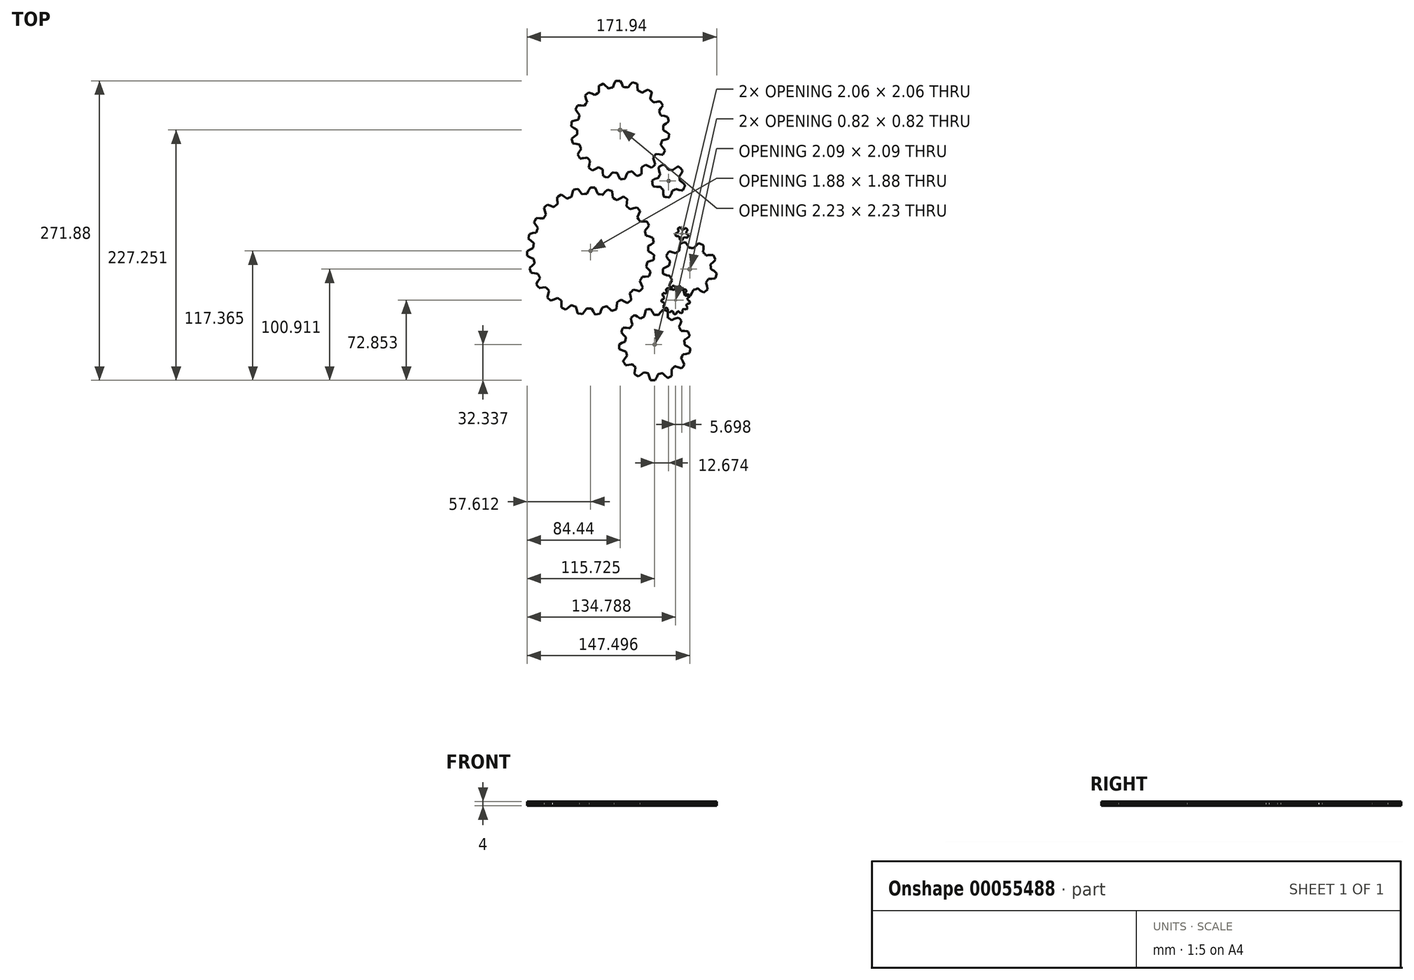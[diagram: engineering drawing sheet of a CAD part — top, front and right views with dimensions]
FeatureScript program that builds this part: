
annotation { "Feature Type Name" : "Feature", "Feature Type Description" : "" }
export const myFeature = defineFeature(function(context is Context, id is Id, definition is map)
    precondition{}
    {
        {
            var Q0;
            Q0=qCreatedBy(makeId("Top.planeOp"),FACE);
            var sketch = newSketch(context, id + "F0", { "sketchPlane" : qUnion([Q0])});
            skLineSegment(sketch, "E0", {"start": v(23.91, -18.64) * mm, "end": v(23.86, -16.49) * mm});
            skLineSegment(sketch, "E1", {"start": v(23.86, -16.49) * mm, "end": v(23.77, -15) * mm});
            skLineSegment(sketch, "E2", {"start": v(23.77, -15) * mm, "end": v(23.72, -14.33) * mm});
            skLineSegment(sketch, "E3", {"start": v(23.72, -14.33) * mm, "end": v(24.54, -13.82) * mm});
            skLineSegment(sketch, "E4", {"start": v(24.54, -13.82) * mm, "end": v(26.32, -12.65) * mm});
            skLineSegment(sketch, "E5", {"start": v(26.32, -12.65) * mm, "end": v(28.84, -10.83) * mm});
            skLineSegment(sketch, "E6", {"start": v(28.84, -10.83) * mm, "end": v(28.51, -8.7) * mm});
            skLineSegment(sketch, "E7", {"start": v(28.51, -8.7) * mm, "end": v(28.25, -7.25) * mm});
            skLineSegment(sketch, "E8", {"start": v(28.25, -7.25) * mm, "end": v(28.15, -6.77) * mm});
            skLineSegment(sketch, "E9", {"start": v(28.15, -6.77) * mm, "end": v(28.11, -6.6) * mm});
            skLineSegment(sketch, "E10", {"start": v(28.11, -6.6) * mm, "end": v(25.07, -5.56) * mm});
            skLineSegment(sketch, "E11", {"start": v(25.07, -5.56) * mm, "end": v(22.97, -4.95) * mm});
            skLineSegment(sketch, "E12", {"start": v(22.97, -4.95) * mm, "end": v(22.02, -4.7) * mm});
            skLineSegment(sketch, "E13", {"start": v(22.02, -4.7) * mm, "end": v(21.8, -3.9) * mm});
            skLineSegment(sketch, "E14", {"start": v(21.8, -3.9) * mm, "end": v(21.36, -2.5) * mm});
            skLineSegment(sketch, "E15", {"start": v(21.36, -2.5) * mm, "end": v(20.88, -1.09) * mm});
            skLineSegment(sketch, "E16", {"start": v(20.88, -1.09) * mm, "end": v(20.65, -0.46) * mm});
            skLineSegment(sketch, "E17", {"start": v(20.65, -0.46) * mm, "end": v(22.68, 1.86) * mm});
            skLineSegment(sketch, "E18", {"start": v(22.68, 1.86) * mm, "end": v(24.04, 3.53) * mm});
            skLineSegment(sketch, "E19", {"start": v(24.04, 3.53) * mm, "end": v(24.62, 4.3) * mm});
            skLineSegment(sketch, "E20", {"start": v(24.62, 4.3) * mm, "end": v(23.74, 6.27) * mm});
            skLineSegment(sketch, "E21", {"start": v(23.74, 6.27) * mm, "end": v(22.76, 8.18) * mm});
            skLineSegment(sketch, "E22", {"start": v(22.76, 8.18) * mm, "end": v(21.77, 8.26) * mm});
            skLineSegment(sketch, "E23", {"start": v(21.77, 8.26) * mm, "end": v(19.56, 8.35) * mm});
            skLineSegment(sketch, "E24", {"start": v(19.56, 8.35) * mm, "end": v(16.4, 8.36) * mm});
            skLineSegment(sketch, "E25", {"start": v(16.4, 8.36) * mm, "end": v(16.32, 8.48) * mm});
            skLineSegment(sketch, "E26", {"start": v(16.32, 8.48) * mm, "end": v(15.16, 10.3) * mm});
            skLineSegment(sketch, "E27", {"start": v(15.16, 10.3) * mm, "end": v(13.92, 12.06) * mm});
            skLineSegment(sketch, "E28", {"start": v(13.92, 12.06) * mm, "end": v(15.25, 14.85) * mm});
            skLineSegment(sketch, "E29", {"start": v(15.25, 14.85) * mm, "end": v(16.46, 17.73) * mm});
            skLineSegment(sketch, "E30", {"start": v(16.46, 17.73) * mm, "end": v(16.35, 17.87) * mm});
            skLineSegment(sketch, "E31", {"start": v(16.35, 17.87) * mm, "end": v(16.04, 18.25) * mm});
            skLineSegment(sketch, "E32", {"start": v(16.04, 18.25) * mm, "end": v(14.09, 20.47) * mm});
            skLineSegment(sketch, "E33", {"start": v(14.09, 20.47) * mm, "end": v(13.63, 20.95) * mm});
            skLineSegment(sketch, "E34", {"start": v(13.63, 20.95) * mm, "end": v(10.5, 20.26) * mm});
            skLineSegment(sketch, "E35", {"start": v(10.5, 20.26) * mm, "end": v(7.44, 19.4) * mm});
            skLineSegment(sketch, "E36", {"start": v(7.44, 19.4) * mm, "end": v(6.84, 19.97) * mm});
            skLineSegment(sketch, "E37", {"start": v(6.84, 19.97) * mm, "end": v(4.6, 21.9) * mm});
            skLineSegment(sketch, "E38", {"start": v(4.6, 21.9) * mm, "end": v(4.06, 22.31) * mm});
            skLineSegment(sketch, "E39", {"start": v(4.06, 22.31) * mm, "end": v(4.6, 25.37) * mm});
            skLineSegment(sketch, "E40", {"start": v(4.6, 25.37) * mm, "end": v(4.99, 28.45) * mm});
            skLineSegment(sketch, "E41", {"start": v(4.99, 28.45) * mm, "end": v(3.88, 29.23) * mm});
            skLineSegment(sketch, "E42", {"start": v(3.88, 29.23) * mm, "end": v(1.97, 30.46) * mm});
            skLineSegment(sketch, "E43", {"start": v(1.97, 30.46) * mm, "end": v(1.4, 30.8) * mm});
            skLineSegment(sketch, "E44", {"start": v(1.4, 30.8) * mm, "end": v(-1.44, 29.29) * mm});
            skLineSegment(sketch, "E45", {"start": v(-1.44, 29.29) * mm, "end": v(-3.31, 28.18) * mm});
            skLineSegment(sketch, "E46", {"start": v(-3.31, 28.18) * mm, "end": v(-4.15, 27.65) * mm});
            skLineSegment(sketch, "E47", {"start": v(-4.15, 27.65) * mm, "end": v(-4.88, 28.02) * mm});
            skLineSegment(sketch, "E48", {"start": v(-4.88, 28.02) * mm, "end": v(-6.21, 28.67) * mm});
            skLineSegment(sketch, "E49", {"start": v(-6.21, 28.67) * mm, "end": v(-8, 29.48) * mm});
            skLineSegment(sketch, "E50", {"start": v(-8, 29.48) * mm, "end": v(-8.18, 29.55) * mm});
            skLineSegment(sketch, "E51", {"start": v(-8.18, 29.55) * mm, "end": v(-8.5, 32.6) * mm});
            skLineSegment(sketch, "E52", {"start": v(-8.5, 32.6) * mm, "end": v(-8.78, 34.74) * mm});
            skLineSegment(sketch, "E53", {"start": v(-8.78, 34.74) * mm, "end": v(-8.95, 35.7) * mm});
            skLineSegment(sketch, "E54", {"start": v(-8.95, 35.7) * mm, "end": v(-10.98, 36.39) * mm});
            skLineSegment(sketch, "E55", {"start": v(-10.98, 36.39) * mm, "end": v(-13.05, 36.98) * mm});
            skLineSegment(sketch, "E56", {"start": v(-13.05, 36.98) * mm, "end": v(-15.36, 34.76) * mm});
            skLineSegment(sketch, "E57", {"start": v(-15.36, 34.76) * mm, "end": v(-17.53, 32.45) * mm});
            skLineSegment(sketch, "E58", {"start": v(-17.53, 32.45) * mm, "end": v(-17.67, 32.48) * mm});
            skLineSegment(sketch, "E59", {"start": v(-17.67, 32.48) * mm, "end": v(-17.85, 32.52) * mm});
            skLineSegment(sketch, "E60", {"start": v(-17.85, 32.52) * mm, "end": v(-19.79, 32.87) * mm});
            skLineSegment(sketch, "E61", {"start": v(-19.79, 32.87) * mm, "end": v(-21.26, 33.08) * mm});
            skLineSegment(sketch, "E62", {"start": v(-21.26, 33.08) * mm, "end": v(-21.92, 33.17) * mm});
            skLineSegment(sketch, "E63", {"start": v(-21.92, 33.17) * mm, "end": v(-22.26, 34.07) * mm});
            skLineSegment(sketch, "E64", {"start": v(-22.26, 34.07) * mm, "end": v(-23.05, 36.05) * mm});
            skLineSegment(sketch, "E65", {"start": v(-23.05, 36.05) * mm, "end": v(-24.33, 38.89) * mm});
            skLineSegment(sketch, "E66", {"start": v(-24.33, 38.89) * mm, "end": v(-26.47, 39) * mm});
            skLineSegment(sketch, "E67", {"start": v(-26.47, 39) * mm, "end": v(-27.95, 39.03) * mm});
            skLineSegment(sketch, "E68", {"start": v(-27.95, 39.03) * mm, "end": v(-28.62, 39.03) * mm});
            skLineSegment(sketch, "E69", {"start": v(-28.62, 39.03) * mm, "end": v(-30.25, 36.25) * mm});
            skLineSegment(sketch, "E70", {"start": v(-30.25, 36.25) * mm, "end": v(-31.72, 33.44) * mm});
            skLineSegment(sketch, "E71", {"start": v(-31.72, 33.44) * mm, "end": v(-34, 33.25) * mm});
            skLineSegment(sketch, "E72", {"start": v(-34, 33.25) * mm, "end": v(-36.15, 32.98) * mm});
            skLineSegment(sketch, "E73", {"start": v(-36.15, 32.98) * mm, "end": v(-36.71, 33.75) * mm});
            skLineSegment(sketch, "E74", {"start": v(-36.71, 33.75) * mm, "end": v(-38, 35.43) * mm});
            skLineSegment(sketch, "E75", {"start": v(-38, 35.43) * mm, "end": v(-39.36, 37.1) * mm});
            skLineSegment(sketch, "E76", {"start": v(-39.36, 37.1) * mm, "end": v(-40, 37.85) * mm});
            skLineSegment(sketch, "E77", {"start": v(-40, 37.85) * mm, "end": v(-42.1, 37.36) * mm});
            skLineSegment(sketch, "E78", {"start": v(-42.1, 37.36) * mm, "end": v(-43.52, 36.99) * mm});
            skLineSegment(sketch, "E79", {"start": v(-43.52, 36.99) * mm, "end": v(-44.17, 36.8) * mm});
            skLineSegment(sketch, "E80", {"start": v(-44.17, 36.8) * mm, "end": v(-44.44, 35.84) * mm});
            skLineSegment(sketch, "E81", {"start": v(-44.44, 35.84) * mm, "end": v(-45, 33.71) * mm});
            skLineSegment(sketch, "E82", {"start": v(-45, 33.71) * mm, "end": v(-45.64, 30.6) * mm});
            skLineSegment(sketch, "E83", {"start": v(-45.64, 30.6) * mm, "end": v(-45.96, 30.5) * mm});
            skLineSegment(sketch, "E84", {"start": v(-45.96, 30.5) * mm, "end": v(-46.42, 30.33) * mm});
            skLineSegment(sketch, "E85", {"start": v(-46.42, 30.33) * mm, "end": v(-48.53, 29.5) * mm});
            skLineSegment(sketch, "E86", {"start": v(-48.53, 29.5) * mm, "end": v(-49.78, 28.94) * mm});
            skLineSegment(sketch, "E87", {"start": v(-49.78, 28.94) * mm, "end": v(-50.53, 29.54) * mm});
            skLineSegment(sketch, "E88", {"start": v(-50.53, 29.54) * mm, "end": v(-52.24, 30.82) * mm});
            skLineSegment(sketch, "E89", {"start": v(-52.24, 30.82) * mm, "end": v(-54.8, 32.58) * mm});
            skLineSegment(sketch, "E90", {"start": v(-54.8, 32.58) * mm, "end": v(-55.4, 32.27) * mm});
            skLineSegment(sketch, "E91", {"start": v(-55.4, 32.27) * mm, "end": v(-57.97, 30.82) * mm});
            skLineSegment(sketch, "E92", {"start": v(-57.97, 30.82) * mm, "end": v(-58.39, 30.57) * mm});
            skLineSegment(sketch, "E93", {"start": v(-58.39, 30.57) * mm, "end": v(-58.54, 30.47) * mm});
            skLineSegment(sketch, "E94", {"start": v(-58.54, 30.47) * mm, "end": v(-58.5, 27.25) * mm});
            skLineSegment(sketch, "E95", {"start": v(-58.5, 27.25) * mm, "end": v(-58.44, 26.1) * mm});
            skLineSegment(sketch, "E96", {"start": v(-58.44, 26.1) * mm, "end": v(-58.28, 24.09) * mm});
            skLineSegment(sketch, "E97", {"start": v(-58.28, 24.09) * mm, "end": v(-59.5, 23.21) * mm});
            skLineSegment(sketch, "E98", {"start": v(-59.5, 23.21) * mm, "end": v(-61.3, 21.8) * mm});
            skLineSegment(sketch, "E99", {"start": v(-61.3, 21.8) * mm, "end": v(-61.67, 21.5) * mm});
            skLineSegment(sketch, "E100", {"start": v(-61.67, 21.5) * mm, "end": v(-61.81, 21.38) * mm});
            skLineSegment(sketch, "E101", {"start": v(-61.81, 21.38) * mm, "end": v(-64.68, 22.51) * mm});
            skLineSegment(sketch, "E102", {"start": v(-64.68, 22.51) * mm, "end": v(-67.63, 23.52) * mm});
            skLineSegment(sketch, "E103", {"start": v(-67.63, 23.52) * mm, "end": v(-69.18, 22.04) * mm});
            skLineSegment(sketch, "E104", {"start": v(-69.18, 22.04) * mm, "end": v(-70.66, 20.48) * mm});
            skLineSegment(sketch, "E105", {"start": v(-70.66, 20.48) * mm, "end": v(-70.4, 19.52) * mm});
            skLineSegment(sketch, "E106", {"start": v(-70.4, 19.52) * mm, "end": v(-69.75, 17.4) * mm});
            skLineSegment(sketch, "E107", {"start": v(-69.75, 17.4) * mm, "end": v(-69.05, 15.34) * mm});
            skLineSegment(sketch, "E108", {"start": v(-69.05, 15.34) * mm, "end": v(-68.7, 14.42) * mm});
            skLineSegment(sketch, "E109", {"start": v(-68.7, 14.42) * mm, "end": v(-70.13, 12.6) * mm});
            skLineSegment(sketch, "E110", {"start": v(-70.13, 12.6) * mm, "end": v(-71.38, 10.85) * mm});
            skLineSegment(sketch, "E111", {"start": v(-71.38, 10.85) * mm, "end": v(-72.34, 10.97) * mm});
            skLineSegment(sketch, "E112", {"start": v(-72.34, 10.97) * mm, "end": v(-74.44, 11.17) * mm});
            skLineSegment(sketch, "E113", {"start": v(-74.44, 11.17) * mm, "end": v(-77.57, 11.36) * mm});
            skLineSegment(sketch, "E114", {"start": v(-77.57, 11.36) * mm, "end": v(-77.66, 11.2) * mm});
            skLineSegment(sketch, "E115", {"start": v(-77.66, 11.2) * mm, "end": v(-79.03, 8.81) * mm});
            skLineSegment(sketch, "E116", {"start": v(-79.03, 8.81) * mm, "end": v(-79.65, 7.6) * mm});
            skLineSegment(sketch, "E117", {"start": v(-79.65, 7.6) * mm, "end": v(-79.13, 6.74) * mm});
            skLineSegment(sketch, "E118", {"start": v(-79.13, 6.74) * mm, "end": v(-77.96, 4.89) * mm});
            skLineSegment(sketch, "E119", {"start": v(-77.96, 4.89) * mm, "end": v(-76.13, 2.29) * mm});
            skLineSegment(sketch, "E120", {"start": v(-76.13, 2.29) * mm, "end": v(-76.46, 1.54) * mm});
            skLineSegment(sketch, "E121", {"start": v(-76.46, 1.54) * mm, "end": v(-77, 0.16) * mm});
            skLineSegment(sketch, "E122", {"start": v(-77, 0.16) * mm, "end": v(-77.52, -1.23) * mm});
            skLineSegment(sketch, "E123", {"start": v(-77.52, -1.23) * mm, "end": v(-77.74, -1.86) * mm});
            skLineSegment(sketch, "E124", {"start": v(-77.74, -1.86) * mm, "end": v(-80.8, -2.38) * mm});
            skLineSegment(sketch, "E125", {"start": v(-80.8, -2.38) * mm, "end": v(-83.83, -3.05) * mm});
            skLineSegment(sketch, "E126", {"start": v(-83.83, -3.05) * mm, "end": v(-84, -3.7) * mm});
            skLineSegment(sketch, "E127", {"start": v(-84, -3.7) * mm, "end": v(-84.37, -5.13) * mm});
            skLineSegment(sketch, "E128", {"start": v(-84.37, -5.13) * mm, "end": v(-84.8, -7.04) * mm});
            skLineSegment(sketch, "E129", {"start": v(-84.8, -7.04) * mm, "end": v(-84.84, -7.23) * mm});
            skLineSegment(sketch, "E130", {"start": v(-84.84, -7.23) * mm, "end": v(-82.45, -9.38) * mm});
            skLineSegment(sketch, "E131", {"start": v(-82.45, -9.38) * mm, "end": v(-80, -11.39) * mm});
            skLineSegment(sketch, "E132", {"start": v(-80, -11.39) * mm, "end": v(-80.27, -13.67) * mm});
            skLineSegment(sketch, "E133", {"start": v(-80.27, -13.67) * mm, "end": v(-80.43, -15.82) * mm});
            skLineSegment(sketch, "E134", {"start": v(-80.43, -15.82) * mm, "end": v(-81.3, -16.22) * mm});
            skLineSegment(sketch, "E135", {"start": v(-81.3, -16.22) * mm, "end": v(-83.2, -17.14) * mm});
            skLineSegment(sketch, "E136", {"start": v(-83.2, -17.14) * mm, "end": v(-85.97, -18.61) * mm});
            skLineSegment(sketch, "E137", {"start": v(-85.97, -18.61) * mm, "end": v(-85.9, -21.54) * mm});
            skLineSegment(sketch, "E138", {"start": v(-85.9, -21.54) * mm, "end": v(-85.8, -22.9) * mm});
            skLineSegment(sketch, "E139", {"start": v(-85.8, -22.9) * mm, "end": v(-82.95, -24.34) * mm});
            skLineSegment(sketch, "E140", {"start": v(-82.95, -24.34) * mm, "end": v(-80.03, -25.61) * mm});
            skLineSegment(sketch, "E141", {"start": v(-80.03, -25.61) * mm, "end": v(-79.93, -26.42) * mm});
            skLineSegment(sketch, "E142", {"start": v(-79.93, -26.42) * mm, "end": v(-79.4, -29.34) * mm});
            skLineSegment(sketch, "E143", {"start": v(-79.4, -29.34) * mm, "end": v(-79.25, -30) * mm});
            skLineSegment(sketch, "E144", {"start": v(-79.25, -30) * mm, "end": v(-81.6, -32.02) * mm});
            skLineSegment(sketch, "E145", {"start": v(-81.6, -32.02) * mm, "end": v(-83.15, -33.49) * mm});
            skLineSegment(sketch, "E146", {"start": v(-83.15, -33.49) * mm, "end": v(-83.84, -34.17) * mm});
            skLineSegment(sketch, "E147", {"start": v(-83.84, -34.17) * mm, "end": v(-83.23, -36.23) * mm});
            skLineSegment(sketch, "E148", {"start": v(-83.23, -36.23) * mm, "end": v(-82.55, -38.27) * mm});
            skLineSegment(sketch, "E149", {"start": v(-82.55, -38.27) * mm, "end": v(-81.56, -38.47) * mm});
            skLineSegment(sketch, "E150", {"start": v(-81.56, -38.47) * mm, "end": v(-79.38, -38.87) * mm});
            skLineSegment(sketch, "E151", {"start": v(-79.38, -38.87) * mm, "end": v(-77.23, -39.2) * mm});
            skLineSegment(sketch, "E152", {"start": v(-77.23, -39.2) * mm, "end": v(-76.25, -39.31) * mm});
            skLineSegment(sketch, "E153", {"start": v(-76.25, -39.31) * mm, "end": v(-75.3, -41.4) * mm});
            skLineSegment(sketch, "E154", {"start": v(-75.3, -41.4) * mm, "end": v(-74.31, -43.32) * mm});
            skLineSegment(sketch, "E155", {"start": v(-74.31, -43.32) * mm, "end": v(-74.85, -44.12) * mm});
            skLineSegment(sketch, "E156", {"start": v(-74.85, -44.12) * mm, "end": v(-76, -45.9) * mm});
            skLineSegment(sketch, "E157", {"start": v(-76, -45.9) * mm, "end": v(-77.6, -48.59) * mm});
            skLineSegment(sketch, "E158", {"start": v(-77.6, -48.59) * mm, "end": v(-76.44, -50.4) * mm});
            skLineSegment(sketch, "E159", {"start": v(-76.44, -50.4) * mm, "end": v(-75.61, -51.62) * mm});
            skLineSegment(sketch, "E160", {"start": v(-75.61, -51.62) * mm, "end": v(-75.22, -52.16) * mm});
            skLineSegment(sketch, "E161", {"start": v(-75.22, -52.16) * mm, "end": v(-74.22, -52.1) * mm});
            skLineSegment(sketch, "E162", {"start": v(-74.22, -52.1) * mm, "end": v(-72.03, -51.9) * mm});
            skLineSegment(sketch, "E163", {"start": v(-72.03, -51.9) * mm, "end": v(-68.88, -51.47) * mm});
            skLineSegment(sketch, "E164", {"start": v(-68.88, -51.47) * mm, "end": v(-68.8, -51.59) * mm});
            skLineSegment(sketch, "E165", {"start": v(-68.8, -51.59) * mm, "end": v(-68.37, -52.1) * mm});
            skLineSegment(sketch, "E166", {"start": v(-68.37, -52.1) * mm, "end": v(-66.87, -53.82) * mm});
            skLineSegment(sketch, "E167", {"start": v(-66.87, -53.82) * mm, "end": v(-65.93, -54.81) * mm});
            skLineSegment(sketch, "E168", {"start": v(-65.93, -54.81) * mm, "end": v(-66.24, -55.72) * mm});
            skLineSegment(sketch, "E169", {"start": v(-66.24, -55.72) * mm, "end": v(-66.88, -57.76) * mm});
            skLineSegment(sketch, "E170", {"start": v(-66.88, -57.76) * mm, "end": v(-67.68, -60.76) * mm});
            skLineSegment(sketch, "E171", {"start": v(-67.68, -60.76) * mm, "end": v(-67.2, -61.23) * mm});
            skLineSegment(sketch, "E172", {"start": v(-67.2, -61.23) * mm, "end": v(-64.97, -63.17) * mm});
            skLineSegment(sketch, "E173", {"start": v(-64.97, -63.17) * mm, "end": v(-64.44, -63.58) * mm});
            skLineSegment(sketch, "E174", {"start": v(-64.44, -63.58) * mm, "end": v(-61.43, -62.47) * mm});
            skLineSegment(sketch, "E175", {"start": v(-61.43, -62.47) * mm, "end": v(-59.41, -61.62) * mm});
            skLineSegment(sketch, "E176", {"start": v(-59.41, -61.62) * mm, "end": v(-58.51, -61.2) * mm});
            skLineSegment(sketch, "E177", {"start": v(-58.51, -61.2) * mm, "end": v(-57.85, -61.68) * mm});
            skLineSegment(sketch, "E178", {"start": v(-57.85, -61.68) * mm, "end": v(-55.36, -63.3) * mm});
            skLineSegment(sketch, "E179", {"start": v(-55.36, -63.3) * mm, "end": v(-54.78, -63.63) * mm});
            skLineSegment(sketch, "E180", {"start": v(-54.78, -63.63) * mm, "end": v(-54.9, -66.72) * mm});
            skLineSegment(sketch, "E181", {"start": v(-54.9, -66.72) * mm, "end": v(-54.89, -68.86) * mm});
            skLineSegment(sketch, "E182", {"start": v(-54.89, -68.86) * mm, "end": v(-54.86, -69.84) * mm});
            skLineSegment(sketch, "E183", {"start": v(-54.86, -69.84) * mm, "end": v(-52.94, -70.8) * mm});
            skLineSegment(sketch, "E184", {"start": v(-52.94, -70.8) * mm, "end": v(-50.98, -71.68) * mm});
            skLineSegment(sketch, "E185", {"start": v(-50.98, -71.68) * mm, "end": v(-50.16, -71.1) * mm});
            skLineSegment(sketch, "E186", {"start": v(-50.16, -71.1) * mm, "end": v(-48.38, -69.78) * mm});
            skLineSegment(sketch, "E187", {"start": v(-48.38, -69.78) * mm, "end": v(-46.68, -68.44) * mm});
            skLineSegment(sketch, "E188", {"start": v(-46.68, -68.44) * mm, "end": v(-45.92, -67.8) * mm});
            skLineSegment(sketch, "E189", {"start": v(-45.92, -67.8) * mm, "end": v(-43.74, -68.53) * mm});
            skLineSegment(sketch, "E190", {"start": v(-43.74, -68.53) * mm, "end": v(-41.67, -69.12) * mm});
            skLineSegment(sketch, "E191", {"start": v(-41.67, -69.12) * mm, "end": v(-41.46, -70.06) * mm});
            skLineSegment(sketch, "E192", {"start": v(-41.46, -70.06) * mm, "end": v(-40.94, -72.11) * mm});
            skLineSegment(sketch, "E193", {"start": v(-40.94, -72.11) * mm, "end": v(-40.06, -75.12) * mm});
            skLineSegment(sketch, "E194", {"start": v(-40.06, -75.12) * mm, "end": v(-39.88, -75.16) * mm});
            skLineSegment(sketch, "E195", {"start": v(-39.88, -75.16) * mm, "end": v(-37.17, -75.64) * mm});
            skLineSegment(sketch, "E196", {"start": v(-37.17, -75.64) * mm, "end": v(-35.83, -75.82) * mm});
            skLineSegment(sketch, "E197", {"start": v(-35.83, -75.82) * mm, "end": v(-33.84, -73.31) * mm});
            skLineSegment(sketch, "E198", {"start": v(-33.84, -73.31) * mm, "end": v(-32, -70.7) * mm});
            skLineSegment(sketch, "E199", {"start": v(-32, -70.7) * mm, "end": v(-31.19, -70.77) * mm});
            skLineSegment(sketch, "E200", {"start": v(-31.19, -70.77) * mm, "end": v(-28.22, -70.85) * mm});
            skLineSegment(sketch, "E201", {"start": v(-28.22, -70.85) * mm, "end": v(-27.55, -70.83) * mm});
            skLineSegment(sketch, "E202", {"start": v(-27.55, -70.83) * mm, "end": v(-26.04, -73.53) * mm});
            skLineSegment(sketch, "E203", {"start": v(-26.04, -73.53) * mm, "end": v(-24.93, -75.36) * mm});
            skLineSegment(sketch, "E204", {"start": v(-24.93, -75.36) * mm, "end": v(-24.4, -76.18) * mm});
            skLineSegment(sketch, "E205", {"start": v(-24.4, -76.18) * mm, "end": v(-22.26, -76) * mm});
            skLineSegment(sketch, "E206", {"start": v(-22.26, -76) * mm, "end": v(-20.13, -75.74) * mm});
            skLineSegment(sketch, "E207", {"start": v(-20.13, -75.74) * mm, "end": v(-19.72, -74.82) * mm});
            skLineSegment(sketch, "E208", {"start": v(-19.72, -74.82) * mm, "end": v(-18.88, -72.77) * mm});
            skLineSegment(sketch, "E209", {"start": v(-18.88, -72.77) * mm, "end": v(-17.81, -69.8) * mm});
            skLineSegment(sketch, "E210", {"start": v(-17.81, -69.8) * mm, "end": v(-15.57, -69.29) * mm});
            skLineSegment(sketch, "E211", {"start": v(-15.57, -69.29) * mm, "end": v(-13.5, -68.71) * mm});
            skLineSegment(sketch, "E212", {"start": v(-13.5, -68.71) * mm, "end": v(-12.82, -69.41) * mm});
            skLineSegment(sketch, "E213", {"start": v(-12.82, -69.41) * mm, "end": v(-11.32, -70.9) * mm});
            skLineSegment(sketch, "E214", {"start": v(-11.32, -70.9) * mm, "end": v(-9.01, -73) * mm});
            skLineSegment(sketch, "E215", {"start": v(-9.01, -73) * mm, "end": v(-8.38, -72.79) * mm});
            skLineSegment(sketch, "E216", {"start": v(-8.38, -72.79) * mm, "end": v(-5.63, -71.7) * mm});
            skLineSegment(sketch, "E217", {"start": v(-5.63, -71.7) * mm, "end": v(-5.02, -71.42) * mm});
            skLineSegment(sketch, "E218", {"start": v(-5.02, -71.42) * mm, "end": v(-4.63, -68.24) * mm});
            skLineSegment(sketch, "E219", {"start": v(-4.63, -68.24) * mm, "end": v(-4.46, -66.05) * mm});
            skLineSegment(sketch, "E220", {"start": v(-4.46, -66.05) * mm, "end": v(-4.4, -65.06) * mm});
            skLineSegment(sketch, "E221", {"start": v(-4.4, -65.06) * mm, "end": v(-4.28, -65) * mm});
            skLineSegment(sketch, "E222", {"start": v(-4.28, -65) * mm, "end": v(-2.39, -63.97) * mm});
            skLineSegment(sketch, "E223", {"start": v(-2.39, -63.97) * mm, "end": v(-1.1, -63.22) * mm});
            skLineSegment(sketch, "E224", {"start": v(-1.1, -63.22) * mm, "end": v(-0.54, -62.86) * mm});
            skLineSegment(sketch, "E225", {"start": v(-0.54, -62.86) * mm, "end": v(2.15, -64.38) * mm});
            skLineSegment(sketch, "E226", {"start": v(2.15, -64.38) * mm, "end": v(4.05, -65.35) * mm});
            skLineSegment(sketch, "E227", {"start": v(4.05, -65.35) * mm, "end": v(4.93, -65.78) * mm});
            skLineSegment(sketch, "E228", {"start": v(4.93, -65.78) * mm, "end": v(5.48, -65.39) * mm});
            skLineSegment(sketch, "E229", {"start": v(5.48, -65.39) * mm, "end": v(6.67, -64.5) * mm});
            skLineSegment(sketch, "E230", {"start": v(6.67, -64.5) * mm, "end": v(8.36, -63.18) * mm});
            skLineSegment(sketch, "E231", {"start": v(8.36, -63.18) * mm, "end": v(8.22, -62.18) * mm});
            skLineSegment(sketch, "E232", {"start": v(8.22, -62.18) * mm, "end": v(7.86, -60) * mm});
            skLineSegment(sketch, "E233", {"start": v(7.86, -60) * mm, "end": v(7.45, -57.86) * mm});
            skLineSegment(sketch, "E234", {"start": v(7.45, -57.86) * mm, "end": v(7.23, -56.9) * mm});
            skLineSegment(sketch, "E235", {"start": v(7.23, -56.9) * mm, "end": v(8.88, -55.3) * mm});
            skLineSegment(sketch, "E236", {"start": v(8.88, -55.3) * mm, "end": v(10.37, -53.73) * mm});
            skLineSegment(sketch, "E237", {"start": v(10.37, -53.73) * mm, "end": v(13.35, -54.46) * mm});
            skLineSegment(sketch, "E238", {"start": v(13.35, -54.46) * mm, "end": v(15.46, -54.9) * mm});
            skLineSegment(sketch, "E239", {"start": v(15.46, -54.9) * mm, "end": v(16.42, -55.07) * mm});
            skLineSegment(sketch, "E240", {"start": v(16.42, -55.07) * mm, "end": v(17.75, -53.38) * mm});
            skLineSegment(sketch, "E241", {"start": v(17.75, -53.38) * mm, "end": v(19, -51.64) * mm});
            skLineSegment(sketch, "E242", {"start": v(19, -51.64) * mm, "end": v(18.61, -50.71) * mm});
            skLineSegment(sketch, "E243", {"start": v(18.61, -50.71) * mm, "end": v(17.68, -48.7) * mm});
            skLineSegment(sketch, "E244", {"start": v(17.68, -48.7) * mm, "end": v(16.24, -45.9) * mm});
            skLineSegment(sketch, "E245", {"start": v(16.24, -45.9) * mm, "end": v(16.32, -45.77) * mm});
            skLineSegment(sketch, "E246", {"start": v(16.32, -45.77) * mm, "end": v(17.4, -43.9) * mm});
            skLineSegment(sketch, "E247", {"start": v(17.4, -43.9) * mm, "end": v(18.4, -42) * mm});
            skLineSegment(sketch, "E248", {"start": v(18.4, -42) * mm, "end": v(19.36, -41.98) * mm});
            skLineSegment(sketch, "E249", {"start": v(19.36, -41.98) * mm, "end": v(21.49, -41.9) * mm});
            skLineSegment(sketch, "E250", {"start": v(21.49, -41.9) * mm, "end": v(24.6, -41.66) * mm});
            skLineSegment(sketch, "E251", {"start": v(24.6, -41.66) * mm, "end": v(24.87, -41.04) * mm});
            skLineSegment(sketch, "E252", {"start": v(24.87, -41.04) * mm, "end": v(25.94, -38.3) * mm});
            skLineSegment(sketch, "E253", {"start": v(25.94, -38.3) * mm, "end": v(26.16, -37.65) * mm});
            skLineSegment(sketch, "E254", {"start": v(26.16, -37.65) * mm, "end": v(24.1, -35.2) * mm});
            skLineSegment(sketch, "E255", {"start": v(24.1, -35.2) * mm, "end": v(22.62, -33.58) * mm});
            skLineSegment(sketch, "E256", {"start": v(22.62, -33.58) * mm, "end": v(21.94, -32.87) * mm});
            skLineSegment(sketch, "E257", {"start": v(21.94, -32.87) * mm, "end": v(22.16, -32.08) * mm});
            skLineSegment(sketch, "E258", {"start": v(22.16, -32.08) * mm, "end": v(22.85, -29.2) * mm});
            skLineSegment(sketch, "E259", {"start": v(22.85, -29.2) * mm, "end": v(22.97, -28.54) * mm});
            skLineSegment(sketch, "E260", {"start": v(22.97, -28.54) * mm, "end": v(25.9, -27.6) * mm});
            skLineSegment(sketch, "E261", {"start": v(25.9, -27.6) * mm, "end": v(27.93, -26.88) * mm});
            skLineSegment(sketch, "E262", {"start": v(27.93, -26.88) * mm, "end": v(28.83, -26.53) * mm});
            skLineSegment(sketch, "E263", {"start": v(28.83, -26.53) * mm, "end": v(29.1, -24.4) * mm});
            skLineSegment(sketch, "E264", {"start": v(29.1, -24.4) * mm, "end": v(29.26, -22.25) * mm});
            skLineSegment(sketch, "E265", {"start": v(29.26, -22.25) * mm, "end": v(28.45, -21.67) * mm});
            skLineSegment(sketch, "E266", {"start": v(28.45, -21.67) * mm, "end": v(26.6, -20.44) * mm});
            skLineSegment(sketch, "E267", {"start": v(26.6, -20.44) * mm, "end": v(23.91, -18.79) * mm});
            skLineSegment(sketch, "E268", {"start": v(23.91, -18.79) * mm, "end": v(23.91, -18.64) * mm});
            skLineSegment(sketch, "E269", {"start": v(-40.68, 91.45) * mm, "end": v(-43.38, 93.06) * mm});
            skLineSegment(sketch, "E270", {"start": v(-43.38, 93.06) * mm, "end": v(-45.2, 94.29) * mm});
            skLineSegment(sketch, "E271", {"start": v(-45.2, 94.29) * mm, "end": v(-46, 94.88) * mm});
            skLineSegment(sketch, "E272", {"start": v(-46, 94.88) * mm, "end": v(-45.78, 96.99) * mm});
            skLineSegment(sketch, "E273", {"start": v(-45.78, 96.99) * mm, "end": v(-45.47, 99.09) * mm});
            skLineSegment(sketch, "E274", {"start": v(-45.47, 99.09) * mm, "end": v(-44.54, 99.4) * mm});
            skLineSegment(sketch, "E275", {"start": v(-44.54, 99.4) * mm, "end": v(-42.5, 100.02) * mm});
            skLineSegment(sketch, "E276", {"start": v(-42.5, 100.02) * mm, "end": v(-39.53, 100.76) * mm});
            skLineSegment(sketch, "E277", {"start": v(-39.53, 100.76) * mm, "end": v(-39.5, 100.93) * mm});
            skLineSegment(sketch, "E278", {"start": v(-39.5, 100.93) * mm, "end": v(-39.37, 101.38) * mm});
            skLineSegment(sketch, "E279", {"start": v(-39.37, 101.38) * mm, "end": v(-38.99, 102.75) * mm});
            skLineSegment(sketch, "E280", {"start": v(-38.99, 102.75) * mm, "end": v(-38.34, 104.7) * mm});
            skLineSegment(sketch, "E281", {"start": v(-38.34, 104.7) * mm, "end": v(-38.29, 104.84) * mm});
            skLineSegment(sketch, "E282", {"start": v(-38.29, 104.84) * mm, "end": v(-40.27, 107.27) * mm});
            skLineSegment(sketch, "E283", {"start": v(-40.27, 107.27) * mm, "end": v(-41.55, 109.05) * mm});
            skLineSegment(sketch, "E284", {"start": v(-41.55, 109.05) * mm, "end": v(-42.1, 109.88) * mm});
            skLineSegment(sketch, "E285", {"start": v(-42.1, 109.88) * mm, "end": v(-41.83, 110.49) * mm});
            skLineSegment(sketch, "E286", {"start": v(-41.83, 110.49) * mm, "end": v(-41.18, 111.79) * mm});
            skLineSegment(sketch, "E287", {"start": v(-41.18, 111.79) * mm, "end": v(-40.49, 113.08) * mm});
            skLineSegment(sketch, "E288", {"start": v(-40.49, 113.08) * mm, "end": v(-40.16, 113.65) * mm});
            skLineSegment(sketch, "E289", {"start": v(-40.16, 113.65) * mm, "end": v(-39.18, 113.63) * mm});
            skLineSegment(sketch, "E290", {"start": v(-39.18, 113.63) * mm, "end": v(-37.05, 113.5) * mm});
            skLineSegment(sketch, "E291", {"start": v(-37.05, 113.5) * mm, "end": v(-34.02, 113.18) * mm});
            skLineSegment(sketch, "E292", {"start": v(-34.02, 113.18) * mm, "end": v(-32.81, 114.86) * mm});
            skLineSegment(sketch, "E293", {"start": v(-32.81, 114.86) * mm, "end": v(-31.64, 116.34) * mm});
            skLineSegment(sketch, "E294", {"start": v(-31.64, 116.34) * mm, "end": v(-31.43, 116.58) * mm});
            skLineSegment(sketch, "E295", {"start": v(-31.43, 116.58) * mm, "end": v(-32.47, 119.56) * mm});
            skLineSegment(sketch, "E296", {"start": v(-32.47, 119.56) * mm, "end": v(-33.3, 122.64) * mm});
            skLineSegment(sketch, "E297", {"start": v(-33.3, 122.64) * mm, "end": v(-32.84, 123.1) * mm});
            skLineSegment(sketch, "E298", {"start": v(-32.84, 123.1) * mm, "end": v(-31.78, 124.11) * mm});
            skLineSegment(sketch, "E299", {"start": v(-31.78, 124.11) * mm, "end": v(-30.19, 125.51) * mm});
            skLineSegment(sketch, "E300", {"start": v(-30.19, 125.51) * mm, "end": v(-29.28, 125.16) * mm});
            skLineSegment(sketch, "E301", {"start": v(-29.28, 125.16) * mm, "end": v(-27.32, 124.31) * mm});
            skLineSegment(sketch, "E302", {"start": v(-27.32, 124.31) * mm, "end": v(-25.42, 123.41) * mm});
            skLineSegment(sketch, "E303", {"start": v(-25.42, 123.41) * mm, "end": v(-24.57, 122.97) * mm});
            skLineSegment(sketch, "E304", {"start": v(-24.57, 122.97) * mm, "end": v(-23.5, 123.73) * mm});
            skLineSegment(sketch, "E305", {"start": v(-23.5, 123.73) * mm, "end": v(-21.66, 124.9) * mm});
            skLineSegment(sketch, "E306", {"start": v(-21.66, 124.9) * mm, "end": v(-20.98, 125.29) * mm});
            skLineSegment(sketch, "E307", {"start": v(-20.98, 125.29) * mm, "end": v(-21, 126.27) * mm});
            skLineSegment(sketch, "E308", {"start": v(-21, 126.27) * mm, "end": v(-20.98, 127.28) * mm});
            skLineSegment(sketch, "E309", {"start": v(-20.98, 127.28) * mm, "end": v(-20.94, 128.43) * mm});
            skLineSegment(sketch, "E310", {"start": v(-20.94, 128.43) * mm, "end": v(-20.79, 130.62) * mm});
            skLineSegment(sketch, "E311", {"start": v(-20.79, 130.62) * mm, "end": v(-20.68, 131.62) * mm});
            skLineSegment(sketch, "E312", {"start": v(-20.68, 131.62) * mm, "end": v(-18.74, 132.5) * mm});
            skLineSegment(sketch, "E313", {"start": v(-18.74, 132.5) * mm, "end": v(-16.94, 133.2) * mm});
            skLineSegment(sketch, "E314", {"start": v(-16.94, 133.2) * mm, "end": v(-16.76, 133.27) * mm});
            skLineSegment(sketch, "E315", {"start": v(-16.76, 133.27) * mm, "end": v(-14.48, 131.15) * mm});
            skLineSegment(sketch, "E316", {"start": v(-14.48, 131.15) * mm, "end": v(-13.68, 130.36) * mm});
            skLineSegment(sketch, "E317", {"start": v(-13.68, 130.36) * mm, "end": v(-12.35, 128.94) * mm});
            skLineSegment(sketch, "E318", {"start": v(-12.35, 128.94) * mm, "end": v(-11.73, 129.12) * mm});
            skLineSegment(sketch, "E319", {"start": v(-11.73, 129.12) * mm, "end": v(-10.36, 129.46) * mm});
            skLineSegment(sketch, "E320", {"start": v(-10.36, 129.46) * mm, "end": v(-8.97, 129.75) * mm});
            skLineSegment(sketch, "E321", {"start": v(-8.97, 129.75) * mm, "end": v(-8.2, 129.9) * mm});
            skLineSegment(sketch, "E322", {"start": v(-8.2, 129.9) * mm, "end": v(-7.07, 132.83) * mm});
            skLineSegment(sketch, "E323", {"start": v(-7.07, 132.83) * mm, "end": v(-6.18, 134.83) * mm});
            skLineSegment(sketch, "E324", {"start": v(-6.18, 134.83) * mm, "end": v(-5.73, 135.73) * mm});
            skLineSegment(sketch, "E325", {"start": v(-5.73, 135.73) * mm, "end": v(-3.62, 135.88) * mm});
            skLineSegment(sketch, "E326", {"start": v(-3.62, 135.88) * mm, "end": v(-1.5, 135.94) * mm});
            skLineSegment(sketch, "E327", {"start": v(-1.5, 135.94) * mm, "end": v(-0.07, 133.17) * mm});
            skLineSegment(sketch, "E328", {"start": v(-0.07, 133.17) * mm, "end": v(0.8, 131.25) * mm});
            skLineSegment(sketch, "E329", {"start": v(0.8, 131.25) * mm, "end": v(1.17, 130.37) * mm});
            skLineSegment(sketch, "E330", {"start": v(1.17, 130.37) * mm, "end": v(2.48, 130.27) * mm});
            skLineSegment(sketch, "E331", {"start": v(2.48, 130.27) * mm, "end": v(4.64, 129.98) * mm});
            skLineSegment(sketch, "E332", {"start": v(4.64, 129.98) * mm, "end": v(5.4, 129.84) * mm});
            skLineSegment(sketch, "E333", {"start": v(5.4, 129.84) * mm, "end": v(6.03, 130.6) * mm});
            skLineSegment(sketch, "E334", {"start": v(6.03, 130.6) * mm, "end": v(6.69, 131.37) * mm});
            skLineSegment(sketch, "E335", {"start": v(6.69, 131.37) * mm, "end": v(7.46, 132.22) * mm});
            skLineSegment(sketch, "E336", {"start": v(7.46, 132.22) * mm, "end": v(8.99, 133.8) * mm});
            skLineSegment(sketch, "E337", {"start": v(8.99, 133.8) * mm, "end": v(9.71, 134.5) * mm});
            skLineSegment(sketch, "E338", {"start": v(9.71, 134.5) * mm, "end": v(11.76, 133.93) * mm});
            skLineSegment(sketch, "E339", {"start": v(11.76, 133.93) * mm, "end": v(13.77, 133.24) * mm});
            skLineSegment(sketch, "E340", {"start": v(13.77, 133.24) * mm, "end": v(13.91, 132.27) * mm});
            skLineSegment(sketch, "E341", {"start": v(13.91, 132.27) * mm, "end": v(14.16, 130.15) * mm});
            skLineSegment(sketch, "E342", {"start": v(14.16, 130.15) * mm, "end": v(14.33, 128.05) * mm});
            skLineSegment(sketch, "E343", {"start": v(14.33, 128.05) * mm, "end": v(14.37, 127.1) * mm});
            skLineSegment(sketch, "E344", {"start": v(14.37, 127.1) * mm, "end": v(14.95, 126.83) * mm});
            skLineSegment(sketch, "E345", {"start": v(14.95, 126.83) * mm, "end": v(16.23, 126.2) * mm});
            skLineSegment(sketch, "E346", {"start": v(16.23, 126.2) * mm, "end": v(17.48, 125.54) * mm});
            skLineSegment(sketch, "E347", {"start": v(17.48, 125.54) * mm, "end": v(18.16, 125.15) * mm});
            skLineSegment(sketch, "E348", {"start": v(18.16, 125.15) * mm, "end": v(20.91, 126.68) * mm});
            skLineSegment(sketch, "E349", {"start": v(20.91, 126.68) * mm, "end": v(22.89, 127.64) * mm});
            skLineSegment(sketch, "E350", {"start": v(22.89, 127.64) * mm, "end": v(23.8, 128.04) * mm});
            skLineSegment(sketch, "E351", {"start": v(23.8, 128.04) * mm, "end": v(25.52, 126.8) * mm});
            skLineSegment(sketch, "E352", {"start": v(25.52, 126.8) * mm, "end": v(26.67, 125.9) * mm});
            skLineSegment(sketch, "E353", {"start": v(26.67, 125.9) * mm, "end": v(27.04, 125.59) * mm});
            skLineSegment(sketch, "E354", {"start": v(27.04, 125.59) * mm, "end": v(27.18, 125.47) * mm});
            skLineSegment(sketch, "E355", {"start": v(27.18, 125.47) * mm, "end": v(26.5, 122.44) * mm});
            skLineSegment(sketch, "E356", {"start": v(26.5, 122.44) * mm, "end": v(25.93, 120.4) * mm});
            skLineSegment(sketch, "E357", {"start": v(25.93, 120.4) * mm, "end": v(25.64, 119.5) * mm});
            skLineSegment(sketch, "E358", {"start": v(25.64, 119.5) * mm, "end": v(26.1, 119.05) * mm});
            skLineSegment(sketch, "E359", {"start": v(26.1, 119.05) * mm, "end": v(27.1, 118.02) * mm});
            skLineSegment(sketch, "E360", {"start": v(27.1, 118.02) * mm, "end": v(28.56, 116.37) * mm});
            skLineSegment(sketch, "E361", {"start": v(28.56, 116.37) * mm, "end": v(29.51, 116.55) * mm});
            skLineSegment(sketch, "E362", {"start": v(29.51, 116.55) * mm, "end": v(31.65, 116.87) * mm});
            skLineSegment(sketch, "E363", {"start": v(31.65, 116.87) * mm, "end": v(32.82, 117) * mm});
            skLineSegment(sketch, "E364", {"start": v(32.82, 117) * mm, "end": v(33.83, 117.1) * mm});
            skLineSegment(sketch, "E365", {"start": v(33.83, 117.1) * mm, "end": v(34.83, 117.16) * mm});
            skLineSegment(sketch, "E366", {"start": v(34.83, 117.16) * mm, "end": v(35.22, 116.62) * mm});
            skLineSegment(sketch, "E367", {"start": v(35.22, 116.62) * mm, "end": v(36.02, 115.4) * mm});
            skLineSegment(sketch, "E368", {"start": v(36.02, 115.4) * mm, "end": v(37.13, 113.6) * mm});
            skLineSegment(sketch, "E369", {"start": v(37.13, 113.6) * mm, "end": v(36.62, 112.76) * mm});
            skLineSegment(sketch, "E370", {"start": v(36.62, 112.76) * mm, "end": v(35.46, 110.98) * mm});
            skLineSegment(sketch, "E371", {"start": v(35.46, 110.98) * mm, "end": v(33.66, 108.5) * mm});
            skLineSegment(sketch, "E372", {"start": v(33.66, 108.5) * mm, "end": v(33.93, 107.92) * mm});
            skLineSegment(sketch, "E373", {"start": v(33.93, 107.92) * mm, "end": v(34.52, 106.63) * mm});
            skLineSegment(sketch, "E374", {"start": v(34.52, 106.63) * mm, "end": v(35.21, 104.87) * mm});
            skLineSegment(sketch, "E375", {"start": v(35.21, 104.87) * mm, "end": v(35.28, 104.7) * mm});
            skLineSegment(sketch, "E376", {"start": v(35.28, 104.7) * mm, "end": v(35.32, 104.57) * mm});
            skLineSegment(sketch, "E377", {"start": v(35.32, 104.57) * mm, "end": v(38.4, 103.98) * mm});
            skLineSegment(sketch, "E378", {"start": v(38.4, 103.98) * mm, "end": v(40.52, 103.45) * mm});
            skLineSegment(sketch, "E379", {"start": v(40.52, 103.45) * mm, "end": v(41.5, 103.17) * mm});
            skLineSegment(sketch, "E380", {"start": v(41.5, 103.17) * mm, "end": v(41.67, 102.53) * mm});
            skLineSegment(sketch, "E381", {"start": v(41.67, 102.53) * mm, "end": v(42.18, 100.35) * mm});
            skLineSegment(sketch, "E382", {"start": v(42.18, 100.35) * mm, "end": v(42.42, 99.02) * mm});
            skLineSegment(sketch, "E383", {"start": v(42.42, 99.02) * mm, "end": v(41.66, 98.42) * mm});
            skLineSegment(sketch, "E384", {"start": v(41.66, 98.42) * mm, "end": v(39.95, 97.14) * mm});
            skLineSegment(sketch, "E385", {"start": v(39.95, 97.14) * mm, "end": v(37.41, 95.44) * mm});
            skLineSegment(sketch, "E386", {"start": v(37.41, 95.44) * mm, "end": v(37.43, 95.26) * mm});
            skLineSegment(sketch, "E387", {"start": v(37.43, 95.26) * mm, "end": v(37.57, 93.38) * mm});
            skLineSegment(sketch, "E388", {"start": v(37.57, 93.38) * mm, "end": v(37.63, 91.31) * mm});
            skLineSegment(sketch, "E389", {"start": v(37.63, 91.31) * mm, "end": v(37.62, 91.17) * mm});
            skLineSegment(sketch, "E390", {"start": v(37.62, 91.17) * mm, "end": v(40.32, 89.56) * mm});
            skLineSegment(sketch, "E391", {"start": v(40.32, 89.56) * mm, "end": v(42.13, 88.33) * mm});
            skLineSegment(sketch, "E392", {"start": v(42.13, 88.33) * mm, "end": v(42.94, 87.74) * mm});
            skLineSegment(sketch, "E393", {"start": v(42.94, 87.74) * mm, "end": v(42.73, 85.63) * mm});
            skLineSegment(sketch, "E394", {"start": v(42.73, 85.63) * mm, "end": v(42.4, 83.53) * mm});
            skLineSegment(sketch, "E395", {"start": v(42.4, 83.53) * mm, "end": v(41.48, 83.22) * mm});
            skLineSegment(sketch, "E396", {"start": v(41.48, 83.22) * mm, "end": v(39.45, 82.6) * mm});
            skLineSegment(sketch, "E397", {"start": v(39.45, 82.6) * mm, "end": v(36.47, 81.86) * mm});
            skLineSegment(sketch, "E398", {"start": v(36.47, 81.86) * mm, "end": v(36.43, 81.7) * mm});
            skLineSegment(sketch, "E399", {"start": v(36.43, 81.7) * mm, "end": v(36.32, 81.24) * mm});
            skLineSegment(sketch, "E400", {"start": v(36.32, 81.24) * mm, "end": v(35.93, 79.87) * mm});
            skLineSegment(sketch, "E401", {"start": v(35.93, 79.87) * mm, "end": v(35.28, 77.91) * mm});
            skLineSegment(sketch, "E402", {"start": v(35.28, 77.91) * mm, "end": v(35.23, 77.78) * mm});
            skLineSegment(sketch, "E403", {"start": v(35.23, 77.78) * mm, "end": v(37.2, 75.35) * mm});
            skLineSegment(sketch, "E404", {"start": v(37.2, 75.35) * mm, "end": v(38.49, 73.57) * mm});
            skLineSegment(sketch, "E405", {"start": v(38.49, 73.57) * mm, "end": v(39.05, 72.74) * mm});
            skLineSegment(sketch, "E406", {"start": v(39.05, 72.74) * mm, "end": v(38.77, 72.14) * mm});
            skLineSegment(sketch, "E407", {"start": v(38.77, 72.14) * mm, "end": v(38.12, 70.83) * mm});
            skLineSegment(sketch, "E408", {"start": v(38.12, 70.83) * mm, "end": v(37.43, 69.55) * mm});
            skLineSegment(sketch, "E409", {"start": v(37.43, 69.55) * mm, "end": v(37.1, 68.97) * mm});
            skLineSegment(sketch, "E410", {"start": v(37.1, 68.97) * mm, "end": v(36.12, 69) * mm});
            skLineSegment(sketch, "E411", {"start": v(36.12, 69) * mm, "end": v(34, 69.12) * mm});
            skLineSegment(sketch, "E412", {"start": v(34, 69.12) * mm, "end": v(30.96, 69.44) * mm});
            skLineSegment(sketch, "E413", {"start": v(30.96, 69.44) * mm, "end": v(29.75, 67.76) * mm});
            skLineSegment(sketch, "E414", {"start": v(29.75, 67.76) * mm, "end": v(28.58, 66.28) * mm});
            skLineSegment(sketch, "E415", {"start": v(28.58, 66.28) * mm, "end": v(28.37, 66.04) * mm});
            skLineSegment(sketch, "E416", {"start": v(28.37, 66.04) * mm, "end": v(29.4, 63.07) * mm});
            skLineSegment(sketch, "E417", {"start": v(29.4, 63.07) * mm, "end": v(30.25, 59.99) * mm});
            skLineSegment(sketch, "E418", {"start": v(30.25, 59.99) * mm, "end": v(29.78, 59.52) * mm});
            skLineSegment(sketch, "E419", {"start": v(29.78, 59.52) * mm, "end": v(28.72, 58.51) * mm});
            skLineSegment(sketch, "E420", {"start": v(28.72, 58.51) * mm, "end": v(27.13, 57.1) * mm});
            skLineSegment(sketch, "E421", {"start": v(27.13, 57.1) * mm, "end": v(26.22, 57.46) * mm});
            skLineSegment(sketch, "E422", {"start": v(26.22, 57.46) * mm, "end": v(24.26, 58.3) * mm});
            skLineSegment(sketch, "E423", {"start": v(24.26, 58.3) * mm, "end": v(22.36, 59.2) * mm});
            skLineSegment(sketch, "E424", {"start": v(22.36, 59.2) * mm, "end": v(21.5, 59.65) * mm});
            skLineSegment(sketch, "E425", {"start": v(21.5, 59.65) * mm, "end": v(20.44, 58.9) * mm});
            skLineSegment(sketch, "E426", {"start": v(20.44, 58.9) * mm, "end": v(18.6, 57.72) * mm});
            skLineSegment(sketch, "E427", {"start": v(18.6, 57.72) * mm, "end": v(17.92, 57.33) * mm});
            skLineSegment(sketch, "E428", {"start": v(17.92, 57.33) * mm, "end": v(17.93, 56.35) * mm});
            skLineSegment(sketch, "E429", {"start": v(17.93, 56.35) * mm, "end": v(17.93, 55.34) * mm});
            skLineSegment(sketch, "E430", {"start": v(17.93, 55.34) * mm, "end": v(17.88, 54.19) * mm});
            skLineSegment(sketch, "E431", {"start": v(17.88, 54.19) * mm, "end": v(17.73, 52) * mm});
            skLineSegment(sketch, "E432", {"start": v(17.73, 52) * mm, "end": v(17.62, 51) * mm});
            skLineSegment(sketch, "E433", {"start": v(17.62, 51) * mm, "end": v(15.68, 50.13) * mm});
            skLineSegment(sketch, "E434", {"start": v(15.68, 50.13) * mm, "end": v(13.88, 49.42) * mm});
            skLineSegment(sketch, "E435", {"start": v(13.88, 49.42) * mm, "end": v(13.7, 49.36) * mm});
            skLineSegment(sketch, "E436", {"start": v(13.7, 49.36) * mm, "end": v(11.42, 51.47) * mm});
            skLineSegment(sketch, "E437", {"start": v(11.42, 51.47) * mm, "end": v(10.62, 52.26) * mm});
            skLineSegment(sketch, "E438", {"start": v(10.62, 52.26) * mm, "end": v(9.3, 53.68) * mm});
            skLineSegment(sketch, "E439", {"start": v(9.3, 53.68) * mm, "end": v(8.67, 53.5) * mm});
            skLineSegment(sketch, "E440", {"start": v(8.67, 53.5) * mm, "end": v(7.3, 53.16) * mm});
            skLineSegment(sketch, "E441", {"start": v(7.3, 53.16) * mm, "end": v(5.9, 52.87) * mm});
            skLineSegment(sketch, "E442", {"start": v(5.9, 52.87) * mm, "end": v(5.14, 52.73) * mm});
            skLineSegment(sketch, "E443", {"start": v(5.14, 52.73) * mm, "end": v(4.01, 49.8) * mm});
            skLineSegment(sketch, "E444", {"start": v(4.01, 49.8) * mm, "end": v(3.12, 47.79) * mm});
            skLineSegment(sketch, "E445", {"start": v(3.12, 47.79) * mm, "end": v(2.68, 46.89) * mm});
            skLineSegment(sketch, "E446", {"start": v(2.68, 46.89) * mm, "end": v(0.56, 46.74) * mm});
            skLineSegment(sketch, "E447", {"start": v(0.56, 46.74) * mm, "end": v(-1.56, 46.69) * mm});
            skLineSegment(sketch, "E448", {"start": v(-1.56, 46.69) * mm, "end": v(-3, 49.46) * mm});
            skLineSegment(sketch, "E449", {"start": v(-3, 49.46) * mm, "end": v(-3.86, 51.37) * mm});
            skLineSegment(sketch, "E450", {"start": v(-3.86, 51.37) * mm, "end": v(-4.23, 52.26) * mm});
            skLineSegment(sketch, "E451", {"start": v(-4.23, 52.26) * mm, "end": v(-5.54, 52.35) * mm});
            skLineSegment(sketch, "E452", {"start": v(-5.54, 52.35) * mm, "end": v(-7.7, 52.64) * mm});
            skLineSegment(sketch, "E453", {"start": v(-7.7, 52.64) * mm, "end": v(-8.47, 52.78) * mm});
            skLineSegment(sketch, "E454", {"start": v(-8.47, 52.78) * mm, "end": v(-9.1, 52.02) * mm});
            skLineSegment(sketch, "E455", {"start": v(-9.1, 52.02) * mm, "end": v(-9.75, 51.25) * mm});
            skLineSegment(sketch, "E456", {"start": v(-9.75, 51.25) * mm, "end": v(-10.52, 50.4) * mm});
            skLineSegment(sketch, "E457", {"start": v(-10.52, 50.4) * mm, "end": v(-12.05, 48.82) * mm});
            skLineSegment(sketch, "E458", {"start": v(-12.05, 48.82) * mm, "end": v(-12.77, 48.12) * mm});
            skLineSegment(sketch, "E459", {"start": v(-12.77, 48.12) * mm, "end": v(-14.81, 48.7) * mm});
            skLineSegment(sketch, "E460", {"start": v(-14.81, 48.7) * mm, "end": v(-16.83, 49.38) * mm});
            skLineSegment(sketch, "E461", {"start": v(-16.83, 49.38) * mm, "end": v(-16.97, 50.35) * mm});
            skLineSegment(sketch, "E462", {"start": v(-16.97, 50.35) * mm, "end": v(-17.22, 52.47) * mm});
            skLineSegment(sketch, "E463", {"start": v(-17.22, 52.47) * mm, "end": v(-17.38, 54.57) * mm});
            skLineSegment(sketch, "E464", {"start": v(-17.38, 54.57) * mm, "end": v(-17.43, 55.53) * mm});
            skLineSegment(sketch, "E465", {"start": v(-17.43, 55.53) * mm, "end": v(-18.01, 55.8) * mm});
            skLineSegment(sketch, "E466", {"start": v(-18.01, 55.8) * mm, "end": v(-19.29, 56.42) * mm});
            skLineSegment(sketch, "E467", {"start": v(-19.29, 56.42) * mm, "end": v(-20.54, 57.08) * mm});
            skLineSegment(sketch, "E468", {"start": v(-20.54, 57.08) * mm, "end": v(-21.22, 57.47) * mm});
            skLineSegment(sketch, "E469", {"start": v(-21.22, 57.47) * mm, "end": v(-23.97, 55.94) * mm});
            skLineSegment(sketch, "E470", {"start": v(-23.97, 55.94) * mm, "end": v(-25.95, 54.98) * mm});
            skLineSegment(sketch, "E471", {"start": v(-25.95, 54.98) * mm, "end": v(-26.86, 54.58) * mm});
            skLineSegment(sketch, "E472", {"start": v(-26.86, 54.58) * mm, "end": v(-28.58, 55.82) * mm});
            skLineSegment(sketch, "E473", {"start": v(-28.58, 55.82) * mm, "end": v(-29.73, 56.73) * mm});
            skLineSegment(sketch, "E474", {"start": v(-29.73, 56.73) * mm, "end": v(-30.1, 57.03) * mm});
            skLineSegment(sketch, "E475", {"start": v(-30.1, 57.03) * mm, "end": v(-30.24, 57.15) * mm});
            skLineSegment(sketch, "E476", {"start": v(-30.24, 57.15) * mm, "end": v(-29.56, 60.18) * mm});
            skLineSegment(sketch, "E477", {"start": v(-29.56, 60.18) * mm, "end": v(-28.98, 62.22) * mm});
            skLineSegment(sketch, "E478", {"start": v(-28.98, 62.22) * mm, "end": v(-28.7, 63.13) * mm});
            skLineSegment(sketch, "E479", {"start": v(-28.7, 63.13) * mm, "end": v(-29.17, 63.57) * mm});
            skLineSegment(sketch, "E480", {"start": v(-29.17, 63.57) * mm, "end": v(-30.15, 64.6) * mm});
            skLineSegment(sketch, "E481", {"start": v(-30.15, 64.6) * mm, "end": v(-31.61, 66.25) * mm});
            skLineSegment(sketch, "E482", {"start": v(-31.61, 66.25) * mm, "end": v(-32.57, 66.07) * mm});
            skLineSegment(sketch, "E483", {"start": v(-32.57, 66.07) * mm, "end": v(-34.71, 65.75) * mm});
            skLineSegment(sketch, "E484", {"start": v(-34.71, 65.75) * mm, "end": v(-35.88, 65.61) * mm});
            skLineSegment(sketch, "E485", {"start": v(-35.88, 65.61) * mm, "end": v(-36.9, 65.53) * mm});
            skLineSegment(sketch, "E486", {"start": v(-36.9, 65.53) * mm, "end": v(-37.9, 65.46) * mm});
            skLineSegment(sketch, "E487", {"start": v(-37.9, 65.46) * mm, "end": v(-38.28, 66) * mm});
            skLineSegment(sketch, "E488", {"start": v(-38.28, 66) * mm, "end": v(-39.08, 67.21) * mm});
            skLineSegment(sketch, "E489", {"start": v(-39.08, 67.21) * mm, "end": v(-40.19, 69.03) * mm});
            skLineSegment(sketch, "E490", {"start": v(-40.19, 69.03) * mm, "end": v(-39.68, 69.86) * mm});
            skLineSegment(sketch, "E491", {"start": v(-39.68, 69.86) * mm, "end": v(-38.52, 71.64) * mm});
            skLineSegment(sketch, "E492", {"start": v(-38.52, 71.64) * mm, "end": v(-36.72, 74.12) * mm});
            skLineSegment(sketch, "E493", {"start": v(-36.72, 74.12) * mm, "end": v(-37, 74.7) * mm});
            skLineSegment(sketch, "E494", {"start": v(-37, 74.7) * mm, "end": v(-37.58, 76) * mm});
            skLineSegment(sketch, "E495", {"start": v(-37.58, 76) * mm, "end": v(-38.27, 77.75) * mm});
            skLineSegment(sketch, "E496", {"start": v(-38.27, 77.75) * mm, "end": v(-38.34, 77.91) * mm});
            skLineSegment(sketch, "E497", {"start": v(-38.34, 77.91) * mm, "end": v(-38.38, 78.05) * mm});
            skLineSegment(sketch, "E498", {"start": v(-38.38, 78.05) * mm, "end": v(-41.47, 78.64) * mm});
            skLineSegment(sketch, "E499", {"start": v(-41.47, 78.64) * mm, "end": v(-43.58, 79.18) * mm});
            skLineSegment(sketch, "E500", {"start": v(-43.58, 79.18) * mm, "end": v(-44.55, 79.45) * mm});
            skLineSegment(sketch, "E501", {"start": v(-44.55, 79.45) * mm, "end": v(-44.73, 80.1) * mm});
            skLineSegment(sketch, "E502", {"start": v(-44.73, 80.1) * mm, "end": v(-45.24, 82.27) * mm});
            skLineSegment(sketch, "E503", {"start": v(-45.24, 82.27) * mm, "end": v(-45.48, 83.6) * mm});
            skLineSegment(sketch, "E504", {"start": v(-45.48, 83.6) * mm, "end": v(-44.72, 84.2) * mm});
            skLineSegment(sketch, "E505", {"start": v(-44.72, 84.2) * mm, "end": v(-43, 85.48) * mm});
            skLineSegment(sketch, "E506", {"start": v(-43, 85.48) * mm, "end": v(-40.47, 87.18) * mm});
            skLineSegment(sketch, "E507", {"start": v(-40.47, 87.18) * mm, "end": v(-40.49, 87.36) * mm});
            skLineSegment(sketch, "E508", {"start": v(-40.49, 87.36) * mm, "end": v(-40.63, 89.24) * mm});
            skLineSegment(sketch, "E509", {"start": v(-40.63, 89.24) * mm, "end": v(-40.69, 91.31) * mm});
            skLineSegment(sketch, "E510", {"start": v(-40.69, 91.31) * mm, "end": v(-40.68, 91.45) * mm});
            skLineSegment(sketch, "E511", {"start": v(56.84, -103.49) * mm, "end": v(56.83, -102.87) * mm});
            skLineSegment(sketch, "E512", {"start": v(56.83, -102.87) * mm, "end": v(56.76, -101.52) * mm});
            skLineSegment(sketch, "E513", {"start": v(56.76, -101.52) * mm, "end": v(56.7, -100.8) * mm});
            skLineSegment(sketch, "E514", {"start": v(56.7, -100.8) * mm, "end": v(56.55, -99.56) * mm});
            skLineSegment(sketch, "E515", {"start": v(56.55, -99.56) * mm, "end": v(57.34, -99.03) * mm});
            skLineSegment(sketch, "E516", {"start": v(57.34, -99.03) * mm, "end": v(59.02, -97.78) * mm});
            skLineSegment(sketch, "E517", {"start": v(59.02, -97.78) * mm, "end": v(60.65, -96.41) * mm});
            skLineSegment(sketch, "E518", {"start": v(60.65, -96.41) * mm, "end": v(61.38, -95.76) * mm});
            skLineSegment(sketch, "E519", {"start": v(61.38, -95.76) * mm, "end": v(61.34, -95.58) * mm});
            skLineSegment(sketch, "E520", {"start": v(61.34, -95.58) * mm, "end": v(61.21, -95.1) * mm});
            skLineSegment(sketch, "E521", {"start": v(61.21, -95.1) * mm, "end": v(60.8, -93.7) * mm});
            skLineSegment(sketch, "E522", {"start": v(60.8, -93.7) * mm, "end": v(60.33, -92.3) * mm});
            skLineSegment(sketch, "E523", {"start": v(60.33, -92.3) * mm, "end": v(60.09, -91.68) * mm});
            skLineSegment(sketch, "E524", {"start": v(60.09, -91.68) * mm, "end": v(59.1, -91.5) * mm});
            skLineSegment(sketch, "E525", {"start": v(59.1, -91.5) * mm, "end": v(56.93, -91.22) * mm});
            skLineSegment(sketch, "E526", {"start": v(56.93, -91.22) * mm, "end": v(54.78, -91.08) * mm});
            skLineSegment(sketch, "E527", {"start": v(54.78, -91.08) * mm, "end": v(53.81, -91.07) * mm});
            skLineSegment(sketch, "E528", {"start": v(53.81, -91.07) * mm, "end": v(53.68, -90.8) * mm});
            skLineSegment(sketch, "E529", {"start": v(53.68, -90.8) * mm, "end": v(53.46, -90.4) * mm});
            skLineSegment(sketch, "E530", {"start": v(53.46, -90.4) * mm, "end": v(52.77, -89.24) * mm});
            skLineSegment(sketch, "E531", {"start": v(52.77, -89.24) * mm, "end": v(52.03, -88.1) * mm});
            skLineSegment(sketch, "E532", {"start": v(52.03, -88.1) * mm, "end": v(51.67, -87.6) * mm});
            skLineSegment(sketch, "E533", {"start": v(51.67, -87.6) * mm, "end": v(52.12, -86.77) * mm});
            skLineSegment(sketch, "E534", {"start": v(52.12, -86.77) * mm, "end": v(53.02, -84.88) * mm});
            skLineSegment(sketch, "E535", {"start": v(53.02, -84.88) * mm, "end": v(53.83, -82.91) * mm});
            skLineSegment(sketch, "E536", {"start": v(53.83, -82.91) * mm, "end": v(54.17, -82) * mm});
            skLineSegment(sketch, "E537", {"start": v(54.17, -82) * mm, "end": v(54.05, -81.86) * mm});
            skLineSegment(sketch, "E538", {"start": v(54.05, -81.86) * mm, "end": v(53.72, -81.5) * mm});
            skLineSegment(sketch, "E539", {"start": v(53.72, -81.5) * mm, "end": v(52.7, -80.44) * mm});
            skLineSegment(sketch, "E540", {"start": v(52.7, -80.44) * mm, "end": v(51.64, -79.43) * mm});
            skLineSegment(sketch, "E541", {"start": v(51.64, -79.43) * mm, "end": v(51.13, -78.99) * mm});
            skLineSegment(sketch, "E542", {"start": v(51.13, -78.99) * mm, "end": v(48.12, -80.05) * mm});
            skLineSegment(sketch, "E543", {"start": v(48.12, -80.05) * mm, "end": v(47.07, -80.5) * mm});
            skLineSegment(sketch, "E544", {"start": v(47.07, -80.5) * mm, "end": v(46.16, -80.92) * mm});
            skLineSegment(sketch, "E545", {"start": v(46.16, -80.92) * mm, "end": v(45.3, -81.36) * mm});
            skLineSegment(sketch, "E546", {"start": v(45.3, -81.36) * mm, "end": v(45.18, -81.28) * mm});
            skLineSegment(sketch, "E547", {"start": v(45.18, -81.28) * mm, "end": v(44.67, -80.93) * mm});
            skLineSegment(sketch, "E548", {"start": v(44.67, -80.93) * mm, "end": v(43.52, -80.22) * mm});
            skLineSegment(sketch, "E549", {"start": v(43.52, -80.22) * mm, "end": v(42.34, -79.56) * mm});
            skLineSegment(sketch, "E550", {"start": v(42.34, -79.56) * mm, "end": v(41.79, -79.28) * mm});
            skLineSegment(sketch, "E551", {"start": v(41.79, -79.28) * mm, "end": v(41.8, -78.33) * mm});
            skLineSegment(sketch, "E552", {"start": v(41.8, -78.33) * mm, "end": v(41.72, -76.24) * mm});
            skLineSegment(sketch, "E553", {"start": v(41.72, -76.24) * mm, "end": v(41.53, -74.12) * mm});
            skLineSegment(sketch, "E554", {"start": v(41.53, -74.12) * mm, "end": v(41.4, -73.15) * mm});
            skLineSegment(sketch, "E555", {"start": v(41.4, -73.15) * mm, "end": v(41.23, -73.09) * mm});
            skLineSegment(sketch, "E556", {"start": v(41.23, -73.09) * mm, "end": v(40.77, -72.92) * mm});
            skLineSegment(sketch, "E557", {"start": v(40.77, -72.92) * mm, "end": v(39.37, -72.45) * mm});
            skLineSegment(sketch, "E558", {"start": v(39.37, -72.45) * mm, "end": v(37.96, -72.05) * mm});
            skLineSegment(sketch, "E559", {"start": v(37.96, -72.05) * mm, "end": v(37.3, -71.9) * mm});
            skLineSegment(sketch, "E560", {"start": v(37.3, -71.9) * mm, "end": v(36.6, -72.62) * mm});
            skLineSegment(sketch, "E561", {"start": v(36.6, -72.62) * mm, "end": v(35.14, -74.24) * mm});
            skLineSegment(sketch, "E562", {"start": v(35.14, -74.24) * mm, "end": v(33.8, -75.93) * mm});
            skLineSegment(sketch, "E563", {"start": v(33.8, -75.93) * mm, "end": v(33.24, -76.72) * mm});
            skLineSegment(sketch, "E564", {"start": v(33.24, -76.72) * mm, "end": v(32.5, -76.63) * mm});
            skLineSegment(sketch, "E565", {"start": v(32.5, -76.63) * mm, "end": v(31.15, -76.53) * mm});
            skLineSegment(sketch, "E566", {"start": v(31.15, -76.53) * mm, "end": v(29.8, -76.5) * mm});
            skLineSegment(sketch, "E567", {"start": v(29.8, -76.5) * mm, "end": v(29.17, -76.52) * mm});
            skLineSegment(sketch, "E568", {"start": v(29.17, -76.52) * mm, "end": v(28.74, -75.68) * mm});
            skLineSegment(sketch, "E569", {"start": v(28.74, -75.68) * mm, "end": v(27.7, -73.85) * mm});
            skLineSegment(sketch, "E570", {"start": v(27.7, -73.85) * mm, "end": v(26.54, -72.06) * mm});
            skLineSegment(sketch, "E571", {"start": v(26.54, -72.06) * mm, "end": v(25.98, -71.27) * mm});
            skLineSegment(sketch, "E572", {"start": v(25.98, -71.27) * mm, "end": v(25.32, -71.35) * mm});
            skLineSegment(sketch, "E573", {"start": v(25.32, -71.35) * mm, "end": v(23.87, -71.6) * mm});
            skLineSegment(sketch, "E574", {"start": v(23.87, -71.6) * mm, "end": v(22.43, -71.9) * mm});
            skLineSegment(sketch, "E575", {"start": v(22.43, -71.9) * mm, "end": v(21.78, -72.05) * mm});
            skLineSegment(sketch, "E576", {"start": v(21.78, -72.05) * mm, "end": v(20.94, -75.13) * mm});
            skLineSegment(sketch, "E577", {"start": v(20.94, -75.13) * mm, "end": v(20.54, -77.25) * mm});
            skLineSegment(sketch, "E578", {"start": v(20.54, -77.25) * mm, "end": v(20.4, -78.2) * mm});
            skLineSegment(sketch, "E579", {"start": v(20.4, -78.2) * mm, "end": v(19.71, -78.48) * mm});
            skLineSegment(sketch, "E580", {"start": v(19.71, -78.48) * mm, "end": v(18.47, -79.02) * mm});
            skLineSegment(sketch, "E581", {"start": v(18.47, -79.02) * mm, "end": v(17.26, -79.62) * mm});
            skLineSegment(sketch, "E582", {"start": v(17.26, -79.62) * mm, "end": v(16.86, -79.83) * mm});
            skLineSegment(sketch, "E583", {"start": v(16.86, -79.83) * mm, "end": v(16.72, -79.92) * mm});
            skLineSegment(sketch, "E584", {"start": v(16.72, -79.92) * mm, "end": v(15.94, -79.38) * mm});
            skLineSegment(sketch, "E585", {"start": v(15.94, -79.38) * mm, "end": v(14.17, -78.24) * mm});
            skLineSegment(sketch, "E586", {"start": v(14.17, -78.24) * mm, "end": v(12.32, -77.2) * mm});
            skLineSegment(sketch, "E587", {"start": v(12.32, -77.2) * mm, "end": v(11.45, -76.76) * mm});
            skLineSegment(sketch, "E588", {"start": v(11.45, -76.76) * mm, "end": v(10.9, -77.15) * mm});
            skLineSegment(sketch, "E589", {"start": v(10.9, -77.15) * mm, "end": v(9.73, -78.04) * mm});
            skLineSegment(sketch, "E590", {"start": v(9.73, -78.04) * mm, "end": v(8.6, -78.97) * mm});
            skLineSegment(sketch, "E591", {"start": v(8.6, -78.97) * mm, "end": v(8.1, -79.41) * mm});
            skLineSegment(sketch, "E592", {"start": v(8.1, -79.41) * mm, "end": v(8.29, -80.4) * mm});
            skLineSegment(sketch, "E593", {"start": v(8.29, -80.4) * mm, "end": v(8.79, -82.53) * mm});
            skLineSegment(sketch, "E594", {"start": v(8.79, -82.53) * mm, "end": v(9.42, -84.59) * mm});
            skLineSegment(sketch, "E595", {"start": v(9.42, -84.59) * mm, "end": v(9.75, -85.5) * mm});
            skLineSegment(sketch, "E596", {"start": v(9.75, -85.5) * mm, "end": v(9.26, -86.06) * mm});
            skLineSegment(sketch, "E597", {"start": v(9.26, -86.06) * mm, "end": v(8.4, -87.12) * mm});
            skLineSegment(sketch, "E598", {"start": v(8.4, -87.12) * mm, "end": v(7.6, -88.22) * mm});
            skLineSegment(sketch, "E599", {"start": v(7.6, -88.22) * mm, "end": v(7.36, -88.59) * mm});
            skLineSegment(sketch, "E600", {"start": v(7.36, -88.59) * mm, "end": v(7.27, -88.73) * mm});
            skLineSegment(sketch, "E601", {"start": v(7.27, -88.73) * mm, "end": v(6.33, -88.6) * mm});
            skLineSegment(sketch, "E602", {"start": v(6.33, -88.6) * mm, "end": v(4.24, -88.42) * mm});
            skLineSegment(sketch, "E603", {"start": v(4.24, -88.42) * mm, "end": v(2.1, -88.36) * mm});
            skLineSegment(sketch, "E604", {"start": v(2.1, -88.36) * mm, "end": v(1.13, -88.37) * mm});
            skLineSegment(sketch, "E605", {"start": v(1.13, -88.37) * mm, "end": v(0.83, -88.97) * mm});
            skLineSegment(sketch, "E606", {"start": v(0.83, -88.97) * mm, "end": v(0.2, -90.3) * mm});
            skLineSegment(sketch, "E607", {"start": v(0.2, -90.3) * mm, "end": v(-0.37, -91.66) * mm});
            skLineSegment(sketch, "E608", {"start": v(-0.37, -91.66) * mm, "end": v(-0.6, -92.28) * mm});
            skLineSegment(sketch, "E609", {"start": v(-0.6, -92.28) * mm, "end": v(0.02, -93.07) * mm});
            skLineSegment(sketch, "E610", {"start": v(0.02, -93.07) * mm, "end": v(1.45, -94.72) * mm});
            skLineSegment(sketch, "E611", {"start": v(1.45, -94.72) * mm, "end": v(2.97, -96.24) * mm});
            skLineSegment(sketch, "E612", {"start": v(2.97, -96.24) * mm, "end": v(3.68, -96.9) * mm});
            skLineSegment(sketch, "E613", {"start": v(3.68, -96.9) * mm, "end": v(3.51, -97.63) * mm});
            skLineSegment(sketch, "E614", {"start": v(3.51, -97.63) * mm, "end": v(3.26, -98.96) * mm});
            skLineSegment(sketch, "E615", {"start": v(3.26, -98.96) * mm, "end": v(3, -100.74) * mm});
            skLineSegment(sketch, "E616", {"start": v(3, -100.74) * mm, "end": v(3, -100.9) * mm});
            skLineSegment(sketch, "E617", {"start": v(3, -100.9) * mm, "end": v(0.17, -102.05) * mm});
            skLineSegment(sketch, "E618", {"start": v(0.17, -102.05) * mm, "end": v(-2.6, -103.46) * mm});
            skLineSegment(sketch, "E619", {"start": v(-2.6, -103.46) * mm, "end": v(-2.58, -104.12) * mm});
            skLineSegment(sketch, "E620", {"start": v(-2.58, -104.12) * mm, "end": v(-2.53, -105.59) * mm});
            skLineSegment(sketch, "E621", {"start": v(-2.53, -105.59) * mm, "end": v(-2.4, -107.05) * mm});
            skLineSegment(sketch, "E622", {"start": v(-2.4, -107.05) * mm, "end": v(-2.32, -107.72) * mm});
            skLineSegment(sketch, "E623", {"start": v(-2.32, -107.72) * mm, "end": v(-1.4, -108.12) * mm});
            skLineSegment(sketch, "E624", {"start": v(-1.4, -108.12) * mm, "end": v(0.64, -108.92) * mm});
            skLineSegment(sketch, "E625", {"start": v(0.64, -108.92) * mm, "end": v(1.72, -109.29) * mm});
            skLineSegment(sketch, "E626", {"start": v(1.72, -109.29) * mm, "end": v(2.69, -109.57) * mm});
            skLineSegment(sketch, "E627", {"start": v(2.69, -109.57) * mm, "end": v(3.62, -109.82) * mm});
            skLineSegment(sketch, "E628", {"start": v(3.62, -109.82) * mm, "end": v(3.65, -109.95) * mm});
            skLineSegment(sketch, "E629", {"start": v(3.65, -109.95) * mm, "end": v(3.8, -110.55) * mm});
            skLineSegment(sketch, "E630", {"start": v(3.8, -110.55) * mm, "end": v(4.2, -111.84) * mm});
            skLineSegment(sketch, "E631", {"start": v(4.2, -111.84) * mm, "end": v(4.64, -113.12) * mm});
            skLineSegment(sketch, "E632", {"start": v(4.64, -113.12) * mm, "end": v(4.87, -113.7) * mm});
            skLineSegment(sketch, "E633", {"start": v(4.87, -113.7) * mm, "end": v(4.23, -114.4) * mm});
            skLineSegment(sketch, "E634", {"start": v(4.23, -114.4) * mm, "end": v(2.9, -116.01) * mm});
            skLineSegment(sketch, "E635", {"start": v(2.9, -116.01) * mm, "end": v(1.65, -117.73) * mm});
            skLineSegment(sketch, "E636", {"start": v(1.65, -117.73) * mm, "end": v(1.1, -118.54) * mm});
            skLineSegment(sketch, "E637", {"start": v(1.1, -118.54) * mm, "end": v(1.19, -118.7) * mm});
            skLineSegment(sketch, "E638", {"start": v(1.19, -118.7) * mm, "end": v(1.42, -119.13) * mm});
            skLineSegment(sketch, "E639", {"start": v(1.42, -119.13) * mm, "end": v(2.16, -120.4) * mm});
            skLineSegment(sketch, "E640", {"start": v(2.16, -120.4) * mm, "end": v(2.95, -121.64) * mm});
            skLineSegment(sketch, "E641", {"start": v(2.95, -121.64) * mm, "end": v(3.34, -122.19) * mm});
            skLineSegment(sketch, "E642", {"start": v(3.34, -122.19) * mm, "end": v(4.34, -122.12) * mm});
            skLineSegment(sketch, "E643", {"start": v(4.34, -122.12) * mm, "end": v(6.51, -121.87) * mm});
            skLineSegment(sketch, "E644", {"start": v(6.51, -121.87) * mm, "end": v(8.63, -121.5) * mm});
            skLineSegment(sketch, "E645", {"start": v(8.63, -121.5) * mm, "end": v(9.57, -121.28) * mm});
            skLineSegment(sketch, "E646", {"start": v(9.57, -121.28) * mm, "end": v(9.77, -121.5) * mm});
            skLineSegment(sketch, "E647", {"start": v(9.77, -121.5) * mm, "end": v(10.07, -121.84) * mm});
            skLineSegment(sketch, "E648", {"start": v(10.07, -121.84) * mm, "end": v(11.02, -122.8) * mm});
            skLineSegment(sketch, "E649", {"start": v(11.02, -122.8) * mm, "end": v(12.01, -123.73) * mm});
            skLineSegment(sketch, "E650", {"start": v(12.01, -123.73) * mm, "end": v(12.48, -124.13) * mm});
            skLineSegment(sketch, "E651", {"start": v(12.48, -124.13) * mm, "end": v(12.24, -125.05) * mm});
            skLineSegment(sketch, "E652", {"start": v(12.24, -125.05) * mm, "end": v(11.81, -127.1) * mm});
            skLineSegment(sketch, "E653", {"start": v(11.81, -127.1) * mm, "end": v(11.5, -129.2) * mm});
            skLineSegment(sketch, "E654", {"start": v(11.5, -129.2) * mm, "end": v(11.4, -130.18) * mm});
            skLineSegment(sketch, "E655", {"start": v(11.4, -130.18) * mm, "end": v(11.54, -130.28) * mm});
            skLineSegment(sketch, "E656", {"start": v(11.54, -130.28) * mm, "end": v(11.94, -130.55) * mm});
            skLineSegment(sketch, "E657", {"start": v(11.94, -130.55) * mm, "end": v(13.19, -131.34) * mm});
            skLineSegment(sketch, "E658", {"start": v(13.19, -131.34) * mm, "end": v(14.46, -132.07) * mm});
            skLineSegment(sketch, "E659", {"start": v(14.46, -132.07) * mm, "end": v(15.06, -132.37) * mm});
            skLineSegment(sketch, "E660", {"start": v(15.06, -132.37) * mm, "end": v(17.73, -130.62) * mm});
            skLineSegment(sketch, "E661", {"start": v(17.73, -130.62) * mm, "end": v(18.65, -129.93) * mm});
            skLineSegment(sketch, "E662", {"start": v(18.65, -129.93) * mm, "end": v(19.43, -129.3) * mm});
            skLineSegment(sketch, "E663", {"start": v(19.43, -129.3) * mm, "end": v(20.16, -128.67) * mm});
            skLineSegment(sketch, "E664", {"start": v(20.16, -128.67) * mm, "end": v(20.44, -128.79) * mm});
            skLineSegment(sketch, "E665", {"start": v(20.44, -128.79) * mm, "end": v(20.86, -128.94) * mm});
            skLineSegment(sketch, "E666", {"start": v(20.86, -128.94) * mm, "end": v(22.15, -129.35) * mm});
            skLineSegment(sketch, "E667", {"start": v(22.15, -129.35) * mm, "end": v(23.46, -129.7) * mm});
            skLineSegment(sketch, "E668", {"start": v(23.46, -129.7) * mm, "end": v(24.06, -129.84) * mm});
            skLineSegment(sketch, "E669", {"start": v(24.06, -129.84) * mm, "end": v(24.28, -130.77) * mm});
            skLineSegment(sketch, "E670", {"start": v(24.28, -130.77) * mm, "end": v(24.85, -132.78) * mm});
            skLineSegment(sketch, "E671", {"start": v(24.85, -132.78) * mm, "end": v(25.55, -134.8) * mm});
            skLineSegment(sketch, "E672", {"start": v(25.55, -134.8) * mm, "end": v(25.91, -135.7) * mm});
            skLineSegment(sketch, "E673", {"start": v(25.91, -135.7) * mm, "end": v(26.58, -135.78) * mm});
            skLineSegment(sketch, "E674", {"start": v(26.58, -135.78) * mm, "end": v(28.04, -135.9) * mm});
            skLineSegment(sketch, "E675", {"start": v(28.04, -135.9) * mm, "end": v(29.51, -135.94) * mm});
            skLineSegment(sketch, "E676", {"start": v(29.51, -135.94) * mm, "end": v(30.18, -135.94) * mm});
            skLineSegment(sketch, "E677", {"start": v(30.18, -135.94) * mm, "end": v(30.7, -135.07) * mm});
            skLineSegment(sketch, "E678", {"start": v(30.7, -135.07) * mm, "end": v(31.72, -133.15) * mm});
            skLineSegment(sketch, "E679", {"start": v(31.72, -133.15) * mm, "end": v(32.62, -131.2) * mm});
            skLineSegment(sketch, "E680", {"start": v(32.62, -131.2) * mm, "end": v(32.98, -130.29) * mm});
            skLineSegment(sketch, "E681", {"start": v(32.98, -130.29) * mm, "end": v(33.72, -130.2) * mm});
            skLineSegment(sketch, "E682", {"start": v(33.72, -130.2) * mm, "end": v(35.06, -129.97) * mm});
            skLineSegment(sketch, "E683", {"start": v(35.06, -129.97) * mm, "end": v(36.38, -129.68) * mm});
            skLineSegment(sketch, "E684", {"start": v(36.38, -129.68) * mm, "end": v(36.81, -129.57) * mm});
            skLineSegment(sketch, "E685", {"start": v(36.81, -129.57) * mm, "end": v(36.98, -129.52) * mm});
            skLineSegment(sketch, "E686", {"start": v(36.98, -129.52) * mm, "end": v(37.6, -130.23) * mm});
            skLineSegment(sketch, "E687", {"start": v(37.6, -130.23) * mm, "end": v(39.04, -131.76) * mm});
            skLineSegment(sketch, "E688", {"start": v(39.04, -131.76) * mm, "end": v(40.6, -133.21) * mm});
            skLineSegment(sketch, "E689", {"start": v(40.6, -133.21) * mm, "end": v(41.33, -133.85) * mm});
            skLineSegment(sketch, "E690", {"start": v(41.33, -133.85) * mm, "end": v(41.96, -133.6) * mm});
            skLineSegment(sketch, "E691", {"start": v(41.96, -133.6) * mm, "end": v(43.3, -133.02) * mm});
            skLineSegment(sketch, "E692", {"start": v(43.3, -133.02) * mm, "end": v(44.63, -132.38) * mm});
            skLineSegment(sketch, "E693", {"start": v(44.63, -132.38) * mm, "end": v(45.23, -132.08) * mm});
            skLineSegment(sketch, "E694", {"start": v(45.23, -132.08) * mm, "end": v(45.24, -131.8) * mm});
            skLineSegment(sketch, "E695", {"start": v(45.24, -131.8) * mm, "end": v(45.28, -131.07) * mm});
            skLineSegment(sketch, "E696", {"start": v(45.28, -131.07) * mm, "end": v(45.3, -128.89) * mm});
            skLineSegment(sketch, "E697", {"start": v(45.3, -128.89) * mm, "end": v(45.17, -126.74) * mm});
            skLineSegment(sketch, "E698", {"start": v(45.17, -126.74) * mm, "end": v(45.07, -125.77) * mm});
            skLineSegment(sketch, "E699", {"start": v(45.07, -125.77) * mm, "end": v(45.68, -125.34) * mm});
            skLineSegment(sketch, "E700", {"start": v(45.68, -125.34) * mm, "end": v(46.76, -124.52) * mm});
            skLineSegment(sketch, "E701", {"start": v(46.76, -124.52) * mm, "end": v(47.8, -123.64) * mm});
            skLineSegment(sketch, "E702", {"start": v(47.8, -123.64) * mm, "end": v(48.13, -123.34) * mm});
            skLineSegment(sketch, "E703", {"start": v(48.13, -123.34) * mm, "end": v(48.25, -123.23) * mm});
            skLineSegment(sketch, "E704", {"start": v(48.25, -123.23) * mm, "end": v(49.13, -123.57) * mm});
            skLineSegment(sketch, "E705", {"start": v(49.13, -123.57) * mm, "end": v(51.12, -124.24) * mm});
            skLineSegment(sketch, "E706", {"start": v(51.12, -124.24) * mm, "end": v(53.17, -124.81) * mm});
            skLineSegment(sketch, "E707", {"start": v(53.17, -124.81) * mm, "end": v(54.12, -125.03) * mm});
            skLineSegment(sketch, "E708", {"start": v(54.12, -125.03) * mm, "end": v(54.56, -124.53) * mm});
            skLineSegment(sketch, "E709", {"start": v(54.56, -124.53) * mm, "end": v(55.49, -123.39) * mm});
            skLineSegment(sketch, "E710", {"start": v(55.49, -123.39) * mm, "end": v(56.36, -122.2) * mm});
            skLineSegment(sketch, "E711", {"start": v(56.36, -122.2) * mm, "end": v(56.75, -121.66) * mm});
            skLineSegment(sketch, "E712", {"start": v(56.75, -121.66) * mm, "end": v(55.33, -118.8) * mm});
            skLineSegment(sketch, "E713", {"start": v(55.33, -118.8) * mm, "end": v(54.23, -116.95) * mm});
            skLineSegment(sketch, "E714", {"start": v(54.23, -116.95) * mm, "end": v(53.7, -116.15) * mm});
            skLineSegment(sketch, "E715", {"start": v(53.7, -116.15) * mm, "end": v(53.75, -116.03) * mm});
            skLineSegment(sketch, "E716", {"start": v(53.75, -116.03) * mm, "end": v(54.6, -114.25) * mm});
            skLineSegment(sketch, "E717", {"start": v(54.6, -114.25) * mm, "end": v(55.12, -113) * mm});
            skLineSegment(sketch, "E718", {"start": v(55.12, -113) * mm, "end": v(55.27, -112.58) * mm});
            skLineSegment(sketch, "E719", {"start": v(55.27, -112.58) * mm, "end": v(55.32, -112.42) * mm});
            skLineSegment(sketch, "E720", {"start": v(55.32, -112.42) * mm, "end": v(56.26, -112.31) * mm});
            skLineSegment(sketch, "E721", {"start": v(56.26, -112.31) * mm, "end": v(58.34, -111.99) * mm});
            skLineSegment(sketch, "E722", {"start": v(58.34, -111.99) * mm, "end": v(60.42, -111.53) * mm});
            skLineSegment(sketch, "E723", {"start": v(60.42, -111.53) * mm, "end": v(61.36, -111.29) * mm});
            skLineSegment(sketch, "E724", {"start": v(61.36, -111.29) * mm, "end": v(61.66, -109.97) * mm});
            skLineSegment(sketch, "E725", {"start": v(61.66, -109.97) * mm, "end": v(61.94, -108.42) * mm});
            skLineSegment(sketch, "E726", {"start": v(61.94, -108.42) * mm, "end": v(62.1, -107.08) * mm});
            skLineSegment(sketch, "E727", {"start": v(62.1, -107.08) * mm, "end": v(61.31, -106.46) * mm});
            skLineSegment(sketch, "E728", {"start": v(61.31, -106.46) * mm, "end": v(59.52, -105.2) * mm});
            skLineSegment(sketch, "E729", {"start": v(59.52, -105.2) * mm, "end": v(57.68, -104.09) * mm});
            skLineSegment(sketch, "E730", {"start": v(57.68, -104.09) * mm, "end": v(56.84, -103.62) * mm});
            skLineSegment(sketch, "E731", {"start": v(56.84, -103.62) * mm, "end": v(56.84, -103.49) * mm});
            skLineSegment(sketch, "E732", {"start": v(43.7, -41.4) * mm, "end": v(44.49, -43.25) * mm});
            skLineSegment(sketch, "E733", {"start": v(44.49, -43.25) * mm, "end": v(44.82, -43.9) * mm});
            skLineSegment(sketch, "E734", {"start": v(44.82, -43.9) * mm, "end": v(45.14, -44.47) * mm});
            skLineSegment(sketch, "E735", {"start": v(45.14, -44.47) * mm, "end": v(45.47, -45.01) * mm});
            skLineSegment(sketch, "E736", {"start": v(45.47, -45.01) * mm, "end": v(44, -47.7) * mm});
            skLineSegment(sketch, "E737", {"start": v(44, -47.7) * mm, "end": v(43.15, -49.7) * mm});
            skLineSegment(sketch, "E738", {"start": v(43.15, -49.7) * mm, "end": v(42.81, -50.64) * mm});
            skLineSegment(sketch, "E739", {"start": v(42.81, -50.64) * mm, "end": v(44.4, -52.36) * mm});
            skLineSegment(sketch, "E740", {"start": v(44.4, -52.36) * mm, "end": v(45.58, -53.45) * mm});
            skLineSegment(sketch, "E741", {"start": v(45.58, -53.45) * mm, "end": v(45.98, -53.8) * mm});
            skLineSegment(sketch, "E742", {"start": v(45.98, -53.8) * mm, "end": v(46.14, -53.92) * mm});
            skLineSegment(sketch, "E743", {"start": v(46.14, -53.92) * mm, "end": v(47.13, -53.6) * mm});
            skLineSegment(sketch, "E744", {"start": v(47.13, -53.6) * mm, "end": v(49.2, -52.8) * mm});
            skLineSegment(sketch, "E745", {"start": v(49.2, -52.8) * mm, "end": v(51.16, -51.84) * mm});
            skLineSegment(sketch, "E746", {"start": v(51.16, -51.84) * mm, "end": v(51.77, -51.5) * mm});
            skLineSegment(sketch, "E747", {"start": v(51.77, -51.5) * mm, "end": v(52, -51.35) * mm});
            skLineSegment(sketch, "E748", {"start": v(52, -51.35) * mm, "end": v(52.12, -51.42) * mm});
            skLineSegment(sketch, "E749", {"start": v(52.12, -51.42) * mm, "end": v(53.91, -52.34) * mm});
            skLineSegment(sketch, "E750", {"start": v(53.91, -52.34) * mm, "end": v(54.6, -52.63) * mm});
            skLineSegment(sketch, "E751", {"start": v(54.6, -52.63) * mm, "end": v(55.2, -52.86) * mm});
            skLineSegment(sketch, "E752", {"start": v(55.2, -52.86) * mm, "end": v(55.8, -53.06) * mm});
            skLineSegment(sketch, "E753", {"start": v(55.8, -53.06) * mm, "end": v(55.94, -54) * mm});
            skLineSegment(sketch, "E754", {"start": v(55.94, -54) * mm, "end": v(56.4, -56.07) * mm});
            skLineSegment(sketch, "E755", {"start": v(56.4, -56.07) * mm, "end": v(57.03, -58.14) * mm});
            skLineSegment(sketch, "E756", {"start": v(57.03, -58.14) * mm, "end": v(57.38, -59.07) * mm});
            skLineSegment(sketch, "E757", {"start": v(57.38, -59.07) * mm, "end": v(58.1, -59.2) * mm});
            skLineSegment(sketch, "E758", {"start": v(58.1, -59.2) * mm, "end": v(59.7, -59.37) * mm});
            skLineSegment(sketch, "E759", {"start": v(59.7, -59.37) * mm, "end": v(61.3, -59.45) * mm});
            skLineSegment(sketch, "E760", {"start": v(61.3, -59.45) * mm, "end": v(62.04, -59.45) * mm});
            skLineSegment(sketch, "E761", {"start": v(62.04, -59.45) * mm, "end": v(63.67, -56.63) * mm});
            skLineSegment(sketch, "E762", {"start": v(63.67, -56.63) * mm, "end": v(64.54, -54.63) * mm});
            skLineSegment(sketch, "E763", {"start": v(64.54, -54.63) * mm, "end": v(64.79, -53.97) * mm});
            skLineSegment(sketch, "E764", {"start": v(64.79, -53.97) * mm, "end": v(64.88, -53.72) * mm});
            skLineSegment(sketch, "E765", {"start": v(64.88, -53.72) * mm, "end": v(65.63, -53.58) * mm});
            skLineSegment(sketch, "E766", {"start": v(65.63, -53.58) * mm, "end": v(66.97, -53.24) * mm});
            skLineSegment(sketch, "E767", {"start": v(66.97, -53.24) * mm, "end": v(68.3, -52.81) * mm});
            skLineSegment(sketch, "E768", {"start": v(68.3, -52.81) * mm, "end": v(68.88, -52.58) * mm});
            skLineSegment(sketch, "E769", {"start": v(68.88, -52.58) * mm, "end": v(69.07, -52.76) * mm});
            skLineSegment(sketch, "E770", {"start": v(69.07, -52.76) * mm, "end": v(69.6, -53.21) * mm});
            skLineSegment(sketch, "E771", {"start": v(69.6, -53.21) * mm, "end": v(71.27, -54.5) * mm});
            skLineSegment(sketch, "E772", {"start": v(71.27, -54.5) * mm, "end": v(73.09, -55.68) * mm});
            skLineSegment(sketch, "E773", {"start": v(73.09, -55.68) * mm, "end": v(73.96, -56.17) * mm});
            skLineSegment(sketch, "E774", {"start": v(73.96, -56.17) * mm, "end": v(74.59, -55.8) * mm});
            skLineSegment(sketch, "E775", {"start": v(74.59, -55.8) * mm, "end": v(75.92, -54.9) * mm});
            skLineSegment(sketch, "E776", {"start": v(75.92, -54.9) * mm, "end": v(77.2, -53.94) * mm});
            skLineSegment(sketch, "E777", {"start": v(77.2, -53.94) * mm, "end": v(77.77, -53.46) * mm});
            skLineSegment(sketch, "E778", {"start": v(77.77, -53.46) * mm, "end": v(77.64, -52.45) * mm});
            skLineSegment(sketch, "E779", {"start": v(77.64, -52.45) * mm, "end": v(77.2, -50.26) * mm});
            skLineSegment(sketch, "E780", {"start": v(77.2, -50.26) * mm, "end": v(76.6, -48.16) * mm});
            skLineSegment(sketch, "E781", {"start": v(76.6, -48.16) * mm, "end": v(76.25, -47.25) * mm});
            skLineSegment(sketch, "E782", {"start": v(76.25, -47.25) * mm, "end": v(76.46, -47.02) * mm});
            skLineSegment(sketch, "E783", {"start": v(76.46, -47.02) * mm, "end": v(76.74, -46.65) * mm});
            skLineSegment(sketch, "E784", {"start": v(76.74, -46.65) * mm, "end": v(77.56, -45.54) * mm});
            skLineSegment(sketch, "E785", {"start": v(77.56, -45.54) * mm, "end": v(78.3, -44.35) * mm});
            skLineSegment(sketch, "E786", {"start": v(78.3, -44.35) * mm, "end": v(78.52, -43.96) * mm});
            skLineSegment(sketch, "E787", {"start": v(78.52, -43.96) * mm, "end": v(78.6, -43.8) * mm});
            skLineSegment(sketch, "E788", {"start": v(78.6, -43.8) * mm, "end": v(79.55, -43.82) * mm});
            skLineSegment(sketch, "E789", {"start": v(79.55, -43.82) * mm, "end": v(81.66, -43.74) * mm});
            skLineSegment(sketch, "E790", {"start": v(81.66, -43.74) * mm, "end": v(83.81, -43.48) * mm});
            skLineSegment(sketch, "E791", {"start": v(83.81, -43.48) * mm, "end": v(84.8, -43.3) * mm});
            skLineSegment(sketch, "E792", {"start": v(84.8, -43.3) * mm, "end": v(85.03, -42.6) * mm});
            skLineSegment(sketch, "E793", {"start": v(85.03, -42.6) * mm, "end": v(85.5, -41.06) * mm});
            skLineSegment(sketch, "E794", {"start": v(85.5, -41.06) * mm, "end": v(85.97, -38.77) * mm});
            skLineSegment(sketch, "E795", {"start": v(85.97, -38.77) * mm, "end": v(85.21, -38.07) * mm});
            skLineSegment(sketch, "E796", {"start": v(85.21, -38.07) * mm, "end": v(83.47, -36.68) * mm});
            skLineSegment(sketch, "E797", {"start": v(83.47, -36.68) * mm, "end": v(81.66, -35.47) * mm});
            skLineSegment(sketch, "E798", {"start": v(81.66, -35.47) * mm, "end": v(80.82, -34.98) * mm});
            skLineSegment(sketch, "E799", {"start": v(80.82, -34.98) * mm, "end": v(80.82, -34.85) * mm});
            skLineSegment(sketch, "E800", {"start": v(80.82, -34.85) * mm, "end": v(80.8, -34.22) * mm});
            skLineSegment(sketch, "E801", {"start": v(80.8, -34.22) * mm, "end": v(80.71, -32.83) * mm});
            skLineSegment(sketch, "E802", {"start": v(80.71, -32.83) * mm, "end": v(80.52, -31.46) * mm});
            skLineSegment(sketch, "E803", {"start": v(80.52, -31.46) * mm, "end": v(80.44, -31) * mm});
            skLineSegment(sketch, "E804", {"start": v(80.44, -31) * mm, "end": v(80.4, -30.84) * mm});
            skLineSegment(sketch, "E805", {"start": v(80.4, -30.84) * mm, "end": v(81.14, -30.24) * mm});
            skLineSegment(sketch, "E806", {"start": v(81.14, -30.24) * mm, "end": v(82.7, -28.82) * mm});
            skLineSegment(sketch, "E807", {"start": v(82.7, -28.82) * mm, "end": v(84.18, -27.24) * mm});
            skLineSegment(sketch, "E808", {"start": v(84.18, -27.24) * mm, "end": v(84.82, -26.46) * mm});
            skLineSegment(sketch, "E809", {"start": v(84.82, -26.46) * mm, "end": v(84.56, -25.78) * mm});
            skLineSegment(sketch, "E810", {"start": v(84.56, -25.78) * mm, "end": v(83.92, -24.3) * mm});
            skLineSegment(sketch, "E811", {"start": v(83.92, -24.3) * mm, "end": v(82.81, -22.24) * mm});
            skLineSegment(sketch, "E812", {"start": v(82.81, -22.24) * mm, "end": v(82.53, -22.22) * mm});
            skLineSegment(sketch, "E813", {"start": v(82.53, -22.22) * mm, "end": v(81.78, -22.2) * mm});
            skLineSegment(sketch, "E814", {"start": v(81.78, -22.2) * mm, "end": v(79.55, -22.24) * mm});
            skLineSegment(sketch, "E815", {"start": v(79.55, -22.24) * mm, "end": v(78.4, -22.34) * mm});
            skLineSegment(sketch, "E816", {"start": v(78.4, -22.34) * mm, "end": v(77.39, -22.48) * mm});
            skLineSegment(sketch, "E817", {"start": v(77.39, -22.48) * mm, "end": v(76.43, -22.65) * mm});
            skLineSegment(sketch, "E818", {"start": v(76.43, -22.65) * mm, "end": v(75.93, -22.07) * mm});
            skLineSegment(sketch, "E819", {"start": v(75.93, -22.07) * mm, "end": v(75.49, -21.6) * mm});
            skLineSegment(sketch, "E820", {"start": v(75.49, -21.6) * mm, "end": v(74.96, -21.07) * mm});
            skLineSegment(sketch, "E821", {"start": v(74.96, -21.07) * mm, "end": v(73.93, -20.14) * mm});
            skLineSegment(sketch, "E822", {"start": v(73.93, -20.14) * mm, "end": v(73.44, -19.75) * mm});
            skLineSegment(sketch, "E823", {"start": v(73.44, -19.75) * mm, "end": v(73.63, -18.81) * mm});
            skLineSegment(sketch, "E824", {"start": v(73.63, -18.81) * mm, "end": v(73.91, -16.71) * mm});
            skLineSegment(sketch, "E825", {"start": v(73.91, -16.71) * mm, "end": v(74.03, -14.55) * mm});
            skLineSegment(sketch, "E826", {"start": v(74.03, -14.55) * mm, "end": v(74.02, -13.56) * mm});
            skLineSegment(sketch, "E827", {"start": v(74.02, -13.56) * mm, "end": v(73.38, -13.2) * mm});
            skLineSegment(sketch, "E828", {"start": v(73.38, -13.2) * mm, "end": v(71.94, -12.48) * mm});
            skLineSegment(sketch, "E829", {"start": v(71.94, -12.48) * mm, "end": v(69.77, -11.6) * mm});
            skLineSegment(sketch, "E830", {"start": v(69.77, -11.6) * mm, "end": v(68.95, -12.23) * mm});
            skLineSegment(sketch, "E831", {"start": v(68.95, -12.23) * mm, "end": v(67.27, -13.7) * mm});
            skLineSegment(sketch, "E832", {"start": v(67.27, -13.7) * mm, "end": v(65.77, -15.27) * mm});
            skLineSegment(sketch, "E833", {"start": v(65.77, -15.27) * mm, "end": v(65.14, -16.03) * mm});
            skLineSegment(sketch, "E834", {"start": v(65.14, -16.03) * mm, "end": v(65, -16) * mm});
            skLineSegment(sketch, "E835", {"start": v(65, -16) * mm, "end": v(63, -15.76) * mm});
            skLineSegment(sketch, "E836", {"start": v(63, -15.76) * mm, "end": v(62.26, -15.73) * mm});
            skLineSegment(sketch, "E837", {"start": v(62.26, -15.73) * mm, "end": v(61.62, -15.71) * mm});
            skLineSegment(sketch, "E838", {"start": v(61.62, -15.71) * mm, "end": v(60.98, -15.73) * mm});
            skLineSegment(sketch, "E839", {"start": v(60.98, -15.73) * mm, "end": v(60.86, -15.5) * mm});
            skLineSegment(sketch, "E840", {"start": v(60.86, -15.5) * mm, "end": v(60.53, -14.9) * mm});
            skLineSegment(sketch, "E841", {"start": v(60.53, -14.9) * mm, "end": v(59.4, -13.1) * mm});
            skLineSegment(sketch, "E842", {"start": v(59.4, -13.1) * mm, "end": v(58.1, -11.37) * mm});
            skLineSegment(sketch, "E843", {"start": v(58.1, -11.37) * mm, "end": v(57.45, -10.61) * mm});
            skLineSegment(sketch, "E844", {"start": v(57.45, -10.61) * mm, "end": v(56.73, -10.74) * mm});
            skLineSegment(sketch, "E845", {"start": v(56.73, -10.74) * mm, "end": v(55.16, -11.12) * mm});
            skLineSegment(sketch, "E846", {"start": v(55.16, -11.12) * mm, "end": v(54.34, -11.36) * mm});
            skLineSegment(sketch, "E847", {"start": v(54.34, -11.36) * mm, "end": v(53.62, -11.6) * mm});
            skLineSegment(sketch, "E848", {"start": v(53.62, -11.6) * mm, "end": v(52.94, -11.85) * mm});
            skLineSegment(sketch, "E849", {"start": v(52.94, -11.85) * mm, "end": v(52.37, -15.06) * mm});
            skLineSegment(sketch, "E850", {"start": v(52.37, -15.06) * mm, "end": v(52.23, -17.23) * mm});
            skLineSegment(sketch, "E851", {"start": v(52.23, -17.23) * mm, "end": v(52.24, -18.2) * mm});
            skLineSegment(sketch, "E852", {"start": v(52.24, -18.2) * mm, "end": v(52.12, -18.27) * mm});
            skLineSegment(sketch, "E853", {"start": v(52.12, -18.27) * mm, "end": v(50.43, -19.37) * mm});
            skLineSegment(sketch, "E854", {"start": v(50.43, -19.37) * mm, "end": v(49.84, -19.82) * mm});
            skLineSegment(sketch, "E855", {"start": v(49.84, -19.82) * mm, "end": v(49.33, -20.23) * mm});
            skLineSegment(sketch, "E856", {"start": v(49.33, -20.23) * mm, "end": v(48.86, -20.65) * mm});
            skLineSegment(sketch, "E857", {"start": v(48.86, -20.65) * mm, "end": v(47.97, -20.3) * mm});
            skLineSegment(sketch, "E858", {"start": v(47.97, -20.3) * mm, "end": v(45.95, -19.66) * mm});
            skLineSegment(sketch, "E859", {"start": v(45.95, -19.66) * mm, "end": v(43.85, -19.17) * mm});
            skLineSegment(sketch, "E860", {"start": v(43.85, -19.17) * mm, "end": v(42.86, -19) * mm});
            skLineSegment(sketch, "E861", {"start": v(42.86, -19) * mm, "end": v(42.4, -19.57) * mm});
            skLineSegment(sketch, "E862", {"start": v(42.4, -19.57) * mm, "end": v(41.94, -20.16) * mm});
            skLineSegment(sketch, "E863", {"start": v(41.94, -20.16) * mm, "end": v(41.44, -20.86) * mm});
            skLineSegment(sketch, "E864", {"start": v(41.44, -20.86) * mm, "end": v(40.57, -22.22) * mm});
            skLineSegment(sketch, "E865", {"start": v(40.57, -22.22) * mm, "end": v(40.2, -22.85) * mm});
            skLineSegment(sketch, "E866", {"start": v(40.2, -22.85) * mm, "end": v(40.68, -23.77) * mm});
            skLineSegment(sketch, "E867", {"start": v(40.68, -23.77) * mm, "end": v(41.83, -25.68) * mm});
            skLineSegment(sketch, "E868", {"start": v(41.83, -25.68) * mm, "end": v(43.12, -27.43) * mm});
            skLineSegment(sketch, "E869", {"start": v(43.12, -27.43) * mm, "end": v(43.74, -28.17) * mm});
            skLineSegment(sketch, "E870", {"start": v(43.74, -28.17) * mm, "end": v(43.7, -28.3) * mm});
            skLineSegment(sketch, "E871", {"start": v(43.7, -28.3) * mm, "end": v(43.5, -28.9) * mm});
            skLineSegment(sketch, "E872", {"start": v(43.5, -28.9) * mm, "end": v(43.3, -29.52) * mm});
            skLineSegment(sketch, "E873", {"start": v(43.3, -29.52) * mm, "end": v(43.1, -30.23) * mm});
            skLineSegment(sketch, "E874", {"start": v(43.1, -30.23) * mm, "end": v(42.94, -30.95) * mm});
            skLineSegment(sketch, "E875", {"start": v(42.94, -30.95) * mm, "end": v(42.83, -31.59) * mm});
            skLineSegment(sketch, "E876", {"start": v(42.83, -31.59) * mm, "end": v(42.73, -32.21) * mm});
            skLineSegment(sketch, "E877", {"start": v(42.73, -32.21) * mm, "end": v(41.83, -32.52) * mm});
            skLineSegment(sketch, "E878", {"start": v(41.83, -32.52) * mm, "end": v(39.87, -33.32) * mm});
            skLineSegment(sketch, "E879", {"start": v(39.87, -33.32) * mm, "end": v(37.94, -34.3) * mm});
            skLineSegment(sketch, "E880", {"start": v(37.94, -34.3) * mm, "end": v(37.08, -34.81) * mm});
            skLineSegment(sketch, "E881", {"start": v(37.08, -34.81) * mm, "end": v(37.1, -35.54) * mm});
            skLineSegment(sketch, "E882", {"start": v(37.1, -35.54) * mm, "end": v(37.19, -37.15) * mm});
            skLineSegment(sketch, "E883", {"start": v(37.19, -37.15) * mm, "end": v(37.39, -38.74) * mm});
            skLineSegment(sketch, "E884", {"start": v(37.39, -38.74) * mm, "end": v(37.52, -39.46) * mm});
            skLineSegment(sketch, "E885", {"start": v(37.52, -39.46) * mm, "end": v(37.77, -39.58) * mm});
            skLineSegment(sketch, "E886", {"start": v(37.77, -39.58) * mm, "end": v(38.47, -39.86) * mm});
            skLineSegment(sketch, "E887", {"start": v(38.47, -39.86) * mm, "end": v(40.58, -40.59) * mm});
            skLineSegment(sketch, "E888", {"start": v(40.58, -40.59) * mm, "end": v(42.7, -41.1) * mm});
            skLineSegment(sketch, "E889", {"start": v(42.7, -41.1) * mm, "end": v(43.65, -41.27) * mm});
            skLineSegment(sketch, "E890", {"start": v(43.65, -41.27) * mm, "end": v(43.7, -41.4) * mm});
            skLineSegment(sketch, "E891", {"start": v(52.54, 45.44) * mm, "end": v(52.5, 46.02) * mm});
            skLineSegment(sketch, "E892", {"start": v(52.5, 46.02) * mm, "end": v(52.35, 47.29) * mm});
            skLineSegment(sketch, "E893", {"start": v(52.35, 47.29) * mm, "end": v(52.2, 47.95) * mm});
            skLineSegment(sketch, "E894", {"start": v(52.2, 47.95) * mm, "end": v(52.03, 48.52) * mm});
            skLineSegment(sketch, "E895", {"start": v(52.03, 48.52) * mm, "end": v(51.83, 49.06) * mm});
            skLineSegment(sketch, "E896", {"start": v(51.83, 49.06) * mm, "end": v(52.01, 49.25) * mm});
            skLineSegment(sketch, "E897", {"start": v(52.01, 49.25) * mm, "end": v(52.47, 49.76) * mm});
            skLineSegment(sketch, "E898", {"start": v(52.47, 49.76) * mm, "end": v(53.72, 51.47) * mm});
            skLineSegment(sketch, "E899", {"start": v(53.72, 51.47) * mm, "end": v(54.73, 53.42) * mm});
            skLineSegment(sketch, "E900", {"start": v(54.73, 53.42) * mm, "end": v(55, 54.1) * mm});
            skLineSegment(sketch, "E901", {"start": v(55, 54.1) * mm, "end": v(55.1, 54.37) * mm});
            skLineSegment(sketch, "E902", {"start": v(55.1, 54.37) * mm, "end": v(54.61, 55.02) * mm});
            skLineSegment(sketch, "E903", {"start": v(54.61, 55.02) * mm, "end": v(54.06, 55.65) * mm});
            skLineSegment(sketch, "E904", {"start": v(54.06, 55.65) * mm, "end": v(53.4, 56.34) * mm});
            skLineSegment(sketch, "E905", {"start": v(53.4, 56.34) * mm, "end": v(52.05, 57.51) * mm});
            skLineSegment(sketch, "E906", {"start": v(52.05, 57.51) * mm, "end": v(51.4, 58) * mm});
            skLineSegment(sketch, "E907", {"start": v(51.4, 58) * mm, "end": v(51.11, 57.91) * mm});
            skLineSegment(sketch, "E908", {"start": v(51.11, 57.91) * mm, "end": v(50.39, 57.63) * mm});
            skLineSegment(sketch, "E909", {"start": v(50.39, 57.63) * mm, "end": v(48.35, 56.62) * mm});
            skLineSegment(sketch, "E910", {"start": v(48.35, 56.62) * mm, "end": v(46.6, 55.35) * mm});
            skLineSegment(sketch, "E911", {"start": v(46.6, 55.35) * mm, "end": v(45.89, 54.7) * mm});
            skLineSegment(sketch, "E912", {"start": v(45.89, 54.7) * mm, "end": v(45.77, 54.74) * mm});
            skLineSegment(sketch, "E913", {"start": v(45.77, 54.74) * mm, "end": v(45.62, 54.8) * mm});
            skLineSegment(sketch, "E914", {"start": v(45.62, 54.8) * mm, "end": v(44.64, 55.04) * mm});
            skLineSegment(sketch, "E915", {"start": v(44.64, 55.04) * mm, "end": v(43.96, 55.14) * mm});
            skLineSegment(sketch, "E916", {"start": v(43.96, 55.14) * mm, "end": v(43.28, 55.2) * mm});
            skLineSegment(sketch, "E917", {"start": v(43.28, 55.2) * mm, "end": v(42.68, 55.22) * mm});
            skLineSegment(sketch, "E918", {"start": v(42.68, 55.22) * mm, "end": v(42.1, 55.19) * mm});
            skLineSegment(sketch, "E919", {"start": v(42.1, 55.19) * mm, "end": v(41.64, 56.02) * mm});
            skLineSegment(sketch, "E920", {"start": v(41.64, 56.02) * mm, "end": v(40.4, 57.73) * mm});
            skLineSegment(sketch, "E921", {"start": v(40.4, 57.73) * mm, "end": v(38.86, 59.3) * mm});
            skLineSegment(sketch, "E922", {"start": v(38.86, 59.3) * mm, "end": v(38.3, 59.79) * mm});
            skLineSegment(sketch, "E923", {"start": v(38.3, 59.79) * mm, "end": v(38.07, 59.96) * mm});
            skLineSegment(sketch, "E924", {"start": v(38.07, 59.96) * mm, "end": v(37.3, 59.68) * mm});
            skLineSegment(sketch, "E925", {"start": v(37.3, 59.68) * mm, "end": v(35.66, 58.94) * mm});
            skLineSegment(sketch, "E926", {"start": v(35.66, 58.94) * mm, "end": v(34.83, 58.47) * mm});
            skLineSegment(sketch, "E927", {"start": v(34.83, 58.47) * mm, "end": v(34.12, 58.02) * mm});
            skLineSegment(sketch, "E928", {"start": v(34.12, 58.02) * mm, "end": v(33.47, 57.53) * mm});
            skLineSegment(sketch, "E929", {"start": v(33.47, 57.53) * mm, "end": v(33.47, 57.24) * mm});
            skLineSegment(sketch, "E930", {"start": v(33.47, 57.24) * mm, "end": v(33.5, 56.47) * mm});
            skLineSegment(sketch, "E931", {"start": v(33.5, 56.47) * mm, "end": v(33.84, 54.23) * mm});
            skLineSegment(sketch, "E932", {"start": v(33.84, 54.23) * mm, "end": v(34.5, 52.16) * mm});
            skLineSegment(sketch, "E933", {"start": v(34.5, 52.16) * mm, "end": v(34.9, 51.28) * mm});
            skLineSegment(sketch, "E934", {"start": v(34.9, 51.28) * mm, "end": v(34.63, 50.9) * mm});
            skLineSegment(sketch, "E935", {"start": v(34.63, 50.9) * mm, "end": v(34.2, 50.2) * mm});
            skLineSegment(sketch, "E936", {"start": v(34.2, 50.2) * mm, "end": v(33.74, 49.27) * mm});
            skLineSegment(sketch, "E937", {"start": v(33.74, 49.27) * mm, "end": v(33.42, 48.4) * mm});
            skLineSegment(sketch, "E938", {"start": v(33.42, 48.4) * mm, "end": v(33.27, 47.84) * mm});
            skLineSegment(sketch, "E939", {"start": v(33.27, 47.84) * mm, "end": v(32.34, 47.66) * mm});
            skLineSegment(sketch, "E940", {"start": v(32.34, 47.66) * mm, "end": v(30.33, 47) * mm});
            skLineSegment(sketch, "E941", {"start": v(30.33, 47) * mm, "end": v(29.78, 46.77) * mm});
            skLineSegment(sketch, "E942", {"start": v(29.78, 46.77) * mm, "end": v(29.27, 46.52) * mm});
            skLineSegment(sketch, "E943", {"start": v(29.27, 46.52) * mm, "end": v(28.37, 46.03) * mm});
            skLineSegment(sketch, "E944", {"start": v(28.37, 46.03) * mm, "end": v(27.49, 45.48) * mm});
            skLineSegment(sketch, "E945", {"start": v(27.49, 45.48) * mm, "end": v(27.5, 45.25) * mm});
            skLineSegment(sketch, "E946", {"start": v(27.5, 45.25) * mm, "end": v(27.57, 43.83) * mm});
            skLineSegment(sketch, "E947", {"start": v(27.57, 43.83) * mm, "end": v(27.8, 42.4) * mm});
            skLineSegment(sketch, "E948", {"start": v(27.8, 42.4) * mm, "end": v(28.11, 41.13) * mm});
            skLineSegment(sketch, "E949", {"start": v(28.11, 41.13) * mm, "end": v(28.3, 40.56) * mm});
            skLineSegment(sketch, "E950", {"start": v(28.3, 40.56) * mm, "end": v(28.37, 40.35) * mm});
            skLineSegment(sketch, "E951", {"start": v(28.37, 40.35) * mm, "end": v(29.4, 40.05) * mm});
            skLineSegment(sketch, "E952", {"start": v(29.4, 40.05) * mm, "end": v(31.63, 39.68) * mm});
            skLineSegment(sketch, "E953", {"start": v(31.63, 39.68) * mm, "end": v(32.8, 39.64) * mm});
            skLineSegment(sketch, "E954", {"start": v(32.8, 39.64) * mm, "end": v(33.8, 39.68) * mm});
            skLineSegment(sketch, "E955", {"start": v(33.8, 39.68) * mm, "end": v(34.5, 39.75) * mm});
            skLineSegment(sketch, "E956", {"start": v(34.5, 39.75) * mm, "end": v(34.76, 39.8) * mm});
            skLineSegment(sketch, "E957", {"start": v(34.76, 39.8) * mm, "end": v(35.18, 39.22) * mm});
            skLineSegment(sketch, "E958", {"start": v(35.18, 39.22) * mm, "end": v(35.8, 38.53) * mm});
            skLineSegment(sketch, "E959", {"start": v(35.8, 38.53) * mm, "end": v(36.57, 37.84) * mm});
            skLineSegment(sketch, "E960", {"start": v(36.57, 37.84) * mm, "end": v(37.05, 37.49) * mm});
            skLineSegment(sketch, "E961", {"start": v(37.05, 37.49) * mm, "end": v(37.4, 37.25) * mm});
            skLineSegment(sketch, "E962", {"start": v(37.4, 37.25) * mm, "end": v(37.53, 37.16) * mm});
            skLineSegment(sketch, "E963", {"start": v(37.53, 37.16) * mm, "end": v(37.42, 36.23) * mm});
            skLineSegment(sketch, "E964", {"start": v(37.42, 36.23) * mm, "end": v(37.42, 34.11) * mm});
            skLineSegment(sketch, "E965", {"start": v(37.42, 34.11) * mm, "end": v(37.54, 32.95) * mm});
            skLineSegment(sketch, "E966", {"start": v(37.54, 32.95) * mm, "end": v(37.74, 31.94) * mm});
            skLineSegment(sketch, "E967", {"start": v(37.74, 31.94) * mm, "end": v(38, 30.94) * mm});
            skLineSegment(sketch, "E968", {"start": v(38, 30.94) * mm, "end": v(38.2, 30.87) * mm});
            skLineSegment(sketch, "E969", {"start": v(38.2, 30.87) * mm, "end": v(39.6, 30.5) * mm});
            skLineSegment(sketch, "E970", {"start": v(39.6, 30.5) * mm, "end": v(40.54, 30.35) * mm});
            skLineSegment(sketch, "E971", {"start": v(40.54, 30.35) * mm, "end": v(42.32, 30.2) * mm});
            skLineSegment(sketch, "E972", {"start": v(42.32, 30.2) * mm, "end": v(42.91, 30.19) * mm});
            skLineSegment(sketch, "E973", {"start": v(42.91, 30.19) * mm, "end": v(43.14, 30.2) * mm});
            skLineSegment(sketch, "E974", {"start": v(43.14, 30.2) * mm, "end": v(43.73, 31.08) * mm});
            skLineSegment(sketch, "E975", {"start": v(43.73, 31.08) * mm, "end": v(44.27, 32) * mm});
            skLineSegment(sketch, "E976", {"start": v(44.27, 32) * mm, "end": v(44.78, 33.1) * mm});
            skLineSegment(sketch, "E977", {"start": v(44.78, 33.1) * mm, "end": v(45.46, 35.16) * mm});
            skLineSegment(sketch, "E978", {"start": v(45.46, 35.16) * mm, "end": v(45.65, 36.08) * mm});
            skLineSegment(sketch, "E979", {"start": v(45.65, 36.08) * mm, "end": v(46.58, 36.43) * mm});
            skLineSegment(sketch, "E980", {"start": v(46.58, 36.43) * mm, "end": v(47.47, 36.86) * mm});
            skLineSegment(sketch, "E981", {"start": v(47.47, 36.86) * mm, "end": v(48.54, 37.56) * mm});
            skLineSegment(sketch, "E982", {"start": v(48.54, 37.56) * mm, "end": v(48.88, 37.81) * mm});
            skLineSegment(sketch, "E983", {"start": v(48.88, 37.81) * mm, "end": v(49, 37.91) * mm});
            skLineSegment(sketch, "E984", {"start": v(49, 37.91) * mm, "end": v(49.85, 37.53) * mm});
            skLineSegment(sketch, "E985", {"start": v(49.85, 37.53) * mm, "end": v(51.87, 36.87) * mm});
            skLineSegment(sketch, "E986", {"start": v(51.87, 36.87) * mm, "end": v(54.03, 36.5) * mm});
            skLineSegment(sketch, "E987", {"start": v(54.03, 36.5) * mm, "end": v(55.05, 36.44) * mm});
            skLineSegment(sketch, "E988", {"start": v(55.05, 36.44) * mm, "end": v(55.19, 36.62) * mm});
            skLineSegment(sketch, "E989", {"start": v(55.19, 36.62) * mm, "end": v(55.52, 37.1) * mm});
            skLineSegment(sketch, "E990", {"start": v(55.52, 37.1) * mm, "end": v(56.4, 38.67) * mm});
            skLineSegment(sketch, "E991", {"start": v(56.4, 38.67) * mm, "end": v(56.82, 39.54) * mm});
            skLineSegment(sketch, "E992", {"start": v(56.82, 39.54) * mm, "end": v(57.31, 40.88) * mm});
            skLineSegment(sketch, "E993", {"start": v(57.31, 40.88) * mm, "end": v(57.37, 41.1) * mm});
            skLineSegment(sketch, "E994", {"start": v(57.37, 41.1) * mm, "end": v(56.7, 41.94) * mm});
            skLineSegment(sketch, "E995", {"start": v(56.7, 41.94) * mm, "end": v(56, 42.73) * mm});
            skLineSegment(sketch, "E996", {"start": v(56, 42.73) * mm, "end": v(55.11, 43.56) * mm});
            skLineSegment(sketch, "E997", {"start": v(55.11, 43.56) * mm, "end": v(54.2, 44.28) * mm});
            skLineSegment(sketch, "E998", {"start": v(54.2, 44.28) * mm, "end": v(53.36, 44.84) * mm});
            skLineSegment(sketch, "E999", {"start": v(53.36, 44.84) * mm, "end": v(52.53, 45.31) * mm});
            skLineSegment(sketch, "E1000", {"start": v(52.53, 45.31) * mm, "end": v(52.54, 45.44) * mm});
            skSolve(sketch);
        }
        {
            var Q0;
            Q0=makeQuery(id+"F0.imprint","IMPRINT",FACE,{"disambiguationData":[TD([[makeQuery(id+"F0.imprint","IMPRINT",EDGE,{"derivedFrom":sQuery(id+"F0.wireOp",EDGE,"E0")}),1.0]])]});
            extrude(context, id + "F1", {"entities" : qUnion([Q0]), "depth" : 4 * mm});
        }
        {
            var Q0;
            Q0=qCreatedBy(makeId("Top.planeOp"),FACE);
            var sketch = newSketch(context, id + "F2", { "sketchPlane" : qUnion([Q0])});
            skLineSegment(sketch, "E1001", {"start": v(23.91, -18.79) * mm, "end": v(26.6, -20.44) * mm});
            skLineSegment(sketch, "E1002", {"start": v(26.6, -20.44) * mm, "end": v(28.45, -21.67) * mm});
            skLineSegment(sketch, "E1003", {"start": v(28.45, -21.67) * mm, "end": v(29.26, -22.25) * mm});
            skLineSegment(sketch, "E1004", {"start": v(29.26, -22.25) * mm, "end": v(29.1, -24.4) * mm});
            skLineSegment(sketch, "E1005", {"start": v(29.1, -24.4) * mm, "end": v(28.83, -26.53) * mm});
            skLineSegment(sketch, "E1006", {"start": v(28.83, -26.53) * mm, "end": v(27.93, -26.88) * mm});
            skLineSegment(sketch, "E1007", {"start": v(27.93, -26.88) * mm, "end": v(25.9, -27.6) * mm});
            skLineSegment(sketch, "E1008", {"start": v(25.9, -27.6) * mm, "end": v(22.97, -28.54) * mm});
            skLineSegment(sketch, "E1009", {"start": v(22.97, -28.54) * mm, "end": v(22.85, -29.2) * mm});
            skLineSegment(sketch, "E1010", {"start": v(22.85, -29.2) * mm, "end": v(22.16, -32.08) * mm});
            skLineSegment(sketch, "E1011", {"start": v(22.16, -32.08) * mm, "end": v(21.94, -32.87) * mm});
            skLineSegment(sketch, "E1012", {"start": v(21.94, -32.87) * mm, "end": v(22.62, -33.58) * mm});
            skLineSegment(sketch, "E1013", {"start": v(22.62, -33.58) * mm, "end": v(24.1, -35.2) * mm});
            skLineSegment(sketch, "E1014", {"start": v(24.1, -35.2) * mm, "end": v(26.16, -37.65) * mm});
            skLineSegment(sketch, "E1015", {"start": v(26.16, -37.65) * mm, "end": v(25.94, -38.3) * mm});
            skLineSegment(sketch, "E1016", {"start": v(25.94, -38.3) * mm, "end": v(24.87, -41.04) * mm});
            skLineSegment(sketch, "E1017", {"start": v(24.87, -41.04) * mm, "end": v(24.6, -41.66) * mm});
            skLineSegment(sketch, "E1018", {"start": v(24.6, -41.66) * mm, "end": v(21.49, -41.9) * mm});
            skLineSegment(sketch, "E1019", {"start": v(21.49, -41.9) * mm, "end": v(19.36, -41.98) * mm});
            skLineSegment(sketch, "E1020", {"start": v(19.36, -41.98) * mm, "end": v(18.4, -42) * mm});
            skLineSegment(sketch, "E1021", {"start": v(18.4, -42) * mm, "end": v(17.4, -43.9) * mm});
            skLineSegment(sketch, "E1022", {"start": v(17.4, -43.9) * mm, "end": v(16.32, -45.77) * mm});
            skLineSegment(sketch, "E1023", {"start": v(16.32, -45.77) * mm, "end": v(16.24, -45.9) * mm});
            skLineSegment(sketch, "E1024", {"start": v(16.24, -45.9) * mm, "end": v(17.68, -48.7) * mm});
            skLineSegment(sketch, "E1025", {"start": v(17.68, -48.7) * mm, "end": v(18.61, -50.71) * mm});
            skLineSegment(sketch, "E1026", {"start": v(18.61, -50.71) * mm, "end": v(19, -51.64) * mm});
            skLineSegment(sketch, "E1027", {"start": v(19, -51.64) * mm, "end": v(17.75, -53.38) * mm});
            skLineSegment(sketch, "E1028", {"start": v(17.75, -53.38) * mm, "end": v(16.42, -55.07) * mm});
            skLineSegment(sketch, "E1029", {"start": v(16.42, -55.07) * mm, "end": v(15.46, -54.9) * mm});
            skLineSegment(sketch, "E1030", {"start": v(15.46, -54.9) * mm, "end": v(13.35, -54.46) * mm});
            skLineSegment(sketch, "E1031", {"start": v(13.35, -54.46) * mm, "end": v(10.37, -53.73) * mm});
            skLineSegment(sketch, "E1032", {"start": v(10.37, -53.73) * mm, "end": v(8.88, -55.3) * mm});
            skLineSegment(sketch, "E1033", {"start": v(8.88, -55.3) * mm, "end": v(7.23, -56.9) * mm});
            skLineSegment(sketch, "E1034", {"start": v(7.23, -56.9) * mm, "end": v(7.45, -57.86) * mm});
            skLineSegment(sketch, "E1035", {"start": v(7.45, -57.86) * mm, "end": v(7.86, -60) * mm});
            skLineSegment(sketch, "E1036", {"start": v(7.86, -60) * mm, "end": v(8.22, -62.18) * mm});
            skLineSegment(sketch, "E1037", {"start": v(8.22, -62.18) * mm, "end": v(8.36, -63.18) * mm});
            skLineSegment(sketch, "E1038", {"start": v(8.36, -63.18) * mm, "end": v(6.67, -64.5) * mm});
            skLineSegment(sketch, "E1039", {"start": v(6.67, -64.5) * mm, "end": v(5.48, -65.39) * mm});
            skLineSegment(sketch, "E1040", {"start": v(5.48, -65.39) * mm, "end": v(4.93, -65.78) * mm});
            skLineSegment(sketch, "E1041", {"start": v(4.93, -65.78) * mm, "end": v(4.05, -65.35) * mm});
            skLineSegment(sketch, "E1042", {"start": v(4.05, -65.35) * mm, "end": v(2.15, -64.38) * mm});
            skLineSegment(sketch, "E1043", {"start": v(2.15, -64.38) * mm, "end": v(-0.54, -62.86) * mm});
            skLineSegment(sketch, "E1044", {"start": v(-0.54, -62.86) * mm, "end": v(-1.1, -63.22) * mm});
            skLineSegment(sketch, "E1045", {"start": v(-1.1, -63.22) * mm, "end": v(-2.39, -63.97) * mm});
            skLineSegment(sketch, "E1046", {"start": v(-2.39, -63.97) * mm, "end": v(-4.28, -65) * mm});
            skLineSegment(sketch, "E1047", {"start": v(-4.28, -65) * mm, "end": v(-4.4, -65.06) * mm});
            skLineSegment(sketch, "E1048", {"start": v(-4.4, -65.06) * mm, "end": v(-4.46, -66.05) * mm});
            skLineSegment(sketch, "E1049", {"start": v(-4.46, -66.05) * mm, "end": v(-4.63, -68.24) * mm});
            skLineSegment(sketch, "E1050", {"start": v(-4.63, -68.24) * mm, "end": v(-5.02, -71.42) * mm});
            skLineSegment(sketch, "E1051", {"start": v(-5.02, -71.42) * mm, "end": v(-5.63, -71.7) * mm});
            skLineSegment(sketch, "E1052", {"start": v(-5.63, -71.7) * mm, "end": v(-8.38, -72.79) * mm});
            skLineSegment(sketch, "E1053", {"start": v(-8.38, -72.79) * mm, "end": v(-9.01, -73) * mm});
            skLineSegment(sketch, "E1054", {"start": v(-9.01, -73) * mm, "end": v(-11.32, -70.9) * mm});
            skLineSegment(sketch, "E1055", {"start": v(-11.32, -70.9) * mm, "end": v(-12.82, -69.41) * mm});
            skLineSegment(sketch, "E1056", {"start": v(-12.82, -69.41) * mm, "end": v(-13.5, -68.71) * mm});
            skLineSegment(sketch, "E1057", {"start": v(-13.5, -68.71) * mm, "end": v(-15.57, -69.29) * mm});
            skLineSegment(sketch, "E1058", {"start": v(-15.57, -69.29) * mm, "end": v(-17.81, -69.8) * mm});
            skLineSegment(sketch, "E1059", {"start": v(-17.81, -69.8) * mm, "end": v(-18.88, -72.77) * mm});
            skLineSegment(sketch, "E1060", {"start": v(-18.88, -72.77) * mm, "end": v(-19.72, -74.82) * mm});
            skLineSegment(sketch, "E1061", {"start": v(-19.72, -74.82) * mm, "end": v(-20.13, -75.74) * mm});
            skLineSegment(sketch, "E1062", {"start": v(-20.13, -75.74) * mm, "end": v(-22.26, -76) * mm});
            skLineSegment(sketch, "E1063", {"start": v(-22.26, -76) * mm, "end": v(-24.4, -76.18) * mm});
            skLineSegment(sketch, "E1064", {"start": v(-24.4, -76.18) * mm, "end": v(-24.93, -75.36) * mm});
            skLineSegment(sketch, "E1065", {"start": v(-24.93, -75.36) * mm, "end": v(-26.04, -73.53) * mm});
            skLineSegment(sketch, "E1066", {"start": v(-26.04, -73.53) * mm, "end": v(-27.55, -70.83) * mm});
            skLineSegment(sketch, "E1067", {"start": v(-27.55, -70.83) * mm, "end": v(-28.22, -70.85) * mm});
            skLineSegment(sketch, "E1068", {"start": v(-28.22, -70.85) * mm, "end": v(-31.19, -70.77) * mm});
            skLineSegment(sketch, "E1069", {"start": v(-31.19, -70.77) * mm, "end": v(-32, -70.7) * mm});
            skLineSegment(sketch, "E1070", {"start": v(-32, -70.7) * mm, "end": v(-33.84, -73.31) * mm});
            skLineSegment(sketch, "E1071", {"start": v(-33.84, -73.31) * mm, "end": v(-35.83, -75.82) * mm});
            skLineSegment(sketch, "E1072", {"start": v(-35.83, -75.82) * mm, "end": v(-37.17, -75.64) * mm});
            skLineSegment(sketch, "E1073", {"start": v(-37.17, -75.64) * mm, "end": v(-39.88, -75.16) * mm});
            skLineSegment(sketch, "E1074", {"start": v(-39.88, -75.16) * mm, "end": v(-40.06, -75.12) * mm});
            skLineSegment(sketch, "E1075", {"start": v(-40.06, -75.12) * mm, "end": v(-40.94, -72.11) * mm});
            skLineSegment(sketch, "E1076", {"start": v(-40.94, -72.11) * mm, "end": v(-41.46, -70.06) * mm});
            skLineSegment(sketch, "E1077", {"start": v(-41.46, -70.06) * mm, "end": v(-41.67, -69.12) * mm});
            skLineSegment(sketch, "E1078", {"start": v(-41.67, -69.12) * mm, "end": v(-43.74, -68.53) * mm});
            skLineSegment(sketch, "E1079", {"start": v(-43.74, -68.53) * mm, "end": v(-45.92, -67.8) * mm});
            skLineSegment(sketch, "E1080", {"start": v(-45.92, -67.8) * mm, "end": v(-46.68, -68.44) * mm});
            skLineSegment(sketch, "E1081", {"start": v(-46.68, -68.44) * mm, "end": v(-48.38, -69.78) * mm});
            skLineSegment(sketch, "E1082", {"start": v(-48.38, -69.78) * mm, "end": v(-50.16, -71.1) * mm});
            skLineSegment(sketch, "E1083", {"start": v(-50.16, -71.1) * mm, "end": v(-50.98, -71.68) * mm});
            skLineSegment(sketch, "E1084", {"start": v(-50.98, -71.68) * mm, "end": v(-52.94, -70.8) * mm});
            skLineSegment(sketch, "E1085", {"start": v(-52.94, -70.8) * mm, "end": v(-54.86, -69.84) * mm});
            skLineSegment(sketch, "E1086", {"start": v(-54.86, -69.84) * mm, "end": v(-54.89, -68.86) * mm});
            skLineSegment(sketch, "E1087", {"start": v(-54.89, -68.86) * mm, "end": v(-54.9, -66.72) * mm});
            skLineSegment(sketch, "E1088", {"start": v(-54.9, -66.72) * mm, "end": v(-54.78, -63.63) * mm});
            skLineSegment(sketch, "E1089", {"start": v(-54.78, -63.63) * mm, "end": v(-55.36, -63.3) * mm});
            skLineSegment(sketch, "E1090", {"start": v(-55.36, -63.3) * mm, "end": v(-57.85, -61.68) * mm});
            skLineSegment(sketch, "E1091", {"start": v(-57.85, -61.68) * mm, "end": v(-58.51, -61.2) * mm});
            skLineSegment(sketch, "E1092", {"start": v(-58.51, -61.2) * mm, "end": v(-59.41, -61.62) * mm});
            skLineSegment(sketch, "E1093", {"start": v(-59.41, -61.62) * mm, "end": v(-61.43, -62.47) * mm});
            skLineSegment(sketch, "E1094", {"start": v(-61.43, -62.47) * mm, "end": v(-64.44, -63.58) * mm});
            skLineSegment(sketch, "E1095", {"start": v(-64.44, -63.58) * mm, "end": v(-64.97, -63.17) * mm});
            skLineSegment(sketch, "E1096", {"start": v(-64.97, -63.17) * mm, "end": v(-67.2, -61.23) * mm});
            skLineSegment(sketch, "E1097", {"start": v(-67.2, -61.23) * mm, "end": v(-67.68, -60.76) * mm});
            skLineSegment(sketch, "E1098", {"start": v(-67.68, -60.76) * mm, "end": v(-66.88, -57.76) * mm});
            skLineSegment(sketch, "E1099", {"start": v(-66.88, -57.76) * mm, "end": v(-66.24, -55.72) * mm});
            skLineSegment(sketch, "E1100", {"start": v(-66.24, -55.72) * mm, "end": v(-65.93, -54.81) * mm});
            skLineSegment(sketch, "E1101", {"start": v(-65.93, -54.81) * mm, "end": v(-66.87, -53.82) * mm});
            skLineSegment(sketch, "E1102", {"start": v(-66.87, -53.82) * mm, "end": v(-68.37, -52.1) * mm});
            skLineSegment(sketch, "E1103", {"start": v(-68.37, -52.1) * mm, "end": v(-68.8, -51.59) * mm});
            skLineSegment(sketch, "E1104", {"start": v(-68.8, -51.59) * mm, "end": v(-68.88, -51.47) * mm});
            skLineSegment(sketch, "E1105", {"start": v(-68.88, -51.47) * mm, "end": v(-72.03, -51.9) * mm});
            skLineSegment(sketch, "E1106", {"start": v(-72.03, -51.9) * mm, "end": v(-74.22, -52.1) * mm});
            skLineSegment(sketch, "E1107", {"start": v(-74.22, -52.1) * mm, "end": v(-75.22, -52.16) * mm});
            skLineSegment(sketch, "E1108", {"start": v(-75.22, -52.16) * mm, "end": v(-75.61, -51.62) * mm});
            skLineSegment(sketch, "E1109", {"start": v(-75.61, -51.62) * mm, "end": v(-76.44, -50.4) * mm});
            skLineSegment(sketch, "E1110", {"start": v(-76.44, -50.4) * mm, "end": v(-77.6, -48.59) * mm});
            skLineSegment(sketch, "E1111", {"start": v(-77.6, -48.59) * mm, "end": v(-76, -45.9) * mm});
            skLineSegment(sketch, "E1112", {"start": v(-76, -45.9) * mm, "end": v(-74.85, -44.12) * mm});
            skLineSegment(sketch, "E1113", {"start": v(-74.85, -44.12) * mm, "end": v(-74.31, -43.32) * mm});
            skLineSegment(sketch, "E1114", {"start": v(-74.31, -43.32) * mm, "end": v(-75.3, -41.4) * mm});
            skLineSegment(sketch, "E1115", {"start": v(-75.3, -41.4) * mm, "end": v(-76.25, -39.31) * mm});
            skLineSegment(sketch, "E1116", {"start": v(-76.25, -39.31) * mm, "end": v(-77.23, -39.2) * mm});
            skLineSegment(sketch, "E1117", {"start": v(-77.23, -39.2) * mm, "end": v(-79.38, -38.87) * mm});
            skLineSegment(sketch, "E1118", {"start": v(-79.38, -38.87) * mm, "end": v(-81.56, -38.47) * mm});
            skLineSegment(sketch, "E1119", {"start": v(-81.56, -38.47) * mm, "end": v(-82.55, -38.27) * mm});
            skLineSegment(sketch, "E1120", {"start": v(-82.55, -38.27) * mm, "end": v(-83.23, -36.23) * mm});
            skLineSegment(sketch, "E1121", {"start": v(-83.23, -36.23) * mm, "end": v(-83.84, -34.17) * mm});
            skLineSegment(sketch, "E1122", {"start": v(-83.84, -34.17) * mm, "end": v(-83.15, -33.49) * mm});
            skLineSegment(sketch, "E1123", {"start": v(-83.15, -33.49) * mm, "end": v(-81.6, -32.02) * mm});
            skLineSegment(sketch, "E1124", {"start": v(-81.6, -32.02) * mm, "end": v(-79.25, -30) * mm});
            skLineSegment(sketch, "E1125", {"start": v(-79.25, -30) * mm, "end": v(-79.4, -29.34) * mm});
            skLineSegment(sketch, "E1126", {"start": v(-79.4, -29.34) * mm, "end": v(-79.93, -26.42) * mm});
            skLineSegment(sketch, "E1127", {"start": v(-79.93, -26.42) * mm, "end": v(-80.03, -25.61) * mm});
            skLineSegment(sketch, "E1128", {"start": v(-80.03, -25.61) * mm, "end": v(-82.95, -24.34) * mm});
            skLineSegment(sketch, "E1129", {"start": v(-82.95, -24.34) * mm, "end": v(-85.8, -22.9) * mm});
            skLineSegment(sketch, "E1130", {"start": v(-85.8, -22.9) * mm, "end": v(-85.9, -21.54) * mm});
            skLineSegment(sketch, "E1131", {"start": v(-85.9, -21.54) * mm, "end": v(-85.97, -18.61) * mm});
            skLineSegment(sketch, "E1132", {"start": v(-85.97, -18.61) * mm, "end": v(-83.2, -17.14) * mm});
            skLineSegment(sketch, "E1133", {"start": v(-83.2, -17.14) * mm, "end": v(-81.3, -16.22) * mm});
            skLineSegment(sketch, "E1134", {"start": v(-81.3, -16.22) * mm, "end": v(-80.43, -15.82) * mm});
            skLineSegment(sketch, "E1135", {"start": v(-80.43, -15.82) * mm, "end": v(-80.27, -13.67) * mm});
            skLineSegment(sketch, "E1136", {"start": v(-80.27, -13.67) * mm, "end": v(-80, -11.39) * mm});
            skLineSegment(sketch, "E1137", {"start": v(-80, -11.39) * mm, "end": v(-82.45, -9.38) * mm});
            skLineSegment(sketch, "E1138", {"start": v(-82.45, -9.38) * mm, "end": v(-84.84, -7.23) * mm});
            skLineSegment(sketch, "E1139", {"start": v(-84.84, -7.23) * mm, "end": v(-84.8, -7.04) * mm});
            skLineSegment(sketch, "E1140", {"start": v(-84.8, -7.04) * mm, "end": v(-84.37, -5.13) * mm});
            skLineSegment(sketch, "E1141", {"start": v(-84.37, -5.13) * mm, "end": v(-84, -3.7) * mm});
            skLineSegment(sketch, "E1142", {"start": v(-84, -3.7) * mm, "end": v(-83.83, -3.05) * mm});
            skLineSegment(sketch, "E1143", {"start": v(-83.83, -3.05) * mm, "end": v(-80.8, -2.38) * mm});
            skLineSegment(sketch, "E1144", {"start": v(-80.8, -2.38) * mm, "end": v(-77.74, -1.86) * mm});
            skLineSegment(sketch, "E1145", {"start": v(-77.74, -1.86) * mm, "end": v(-77.52, -1.23) * mm});
            skLineSegment(sketch, "E1146", {"start": v(-77.52, -1.23) * mm, "end": v(-77, 0.16) * mm});
            skLineSegment(sketch, "E1147", {"start": v(-77, 0.16) * mm, "end": v(-76.46, 1.54) * mm});
            skLineSegment(sketch, "E1148", {"start": v(-76.46, 1.54) * mm, "end": v(-76.13, 2.29) * mm});
            skLineSegment(sketch, "E1149", {"start": v(-76.13, 2.29) * mm, "end": v(-77.96, 4.89) * mm});
            skLineSegment(sketch, "E1150", {"start": v(-77.96, 4.89) * mm, "end": v(-79.13, 6.74) * mm});
            skLineSegment(sketch, "E1151", {"start": v(-79.13, 6.74) * mm, "end": v(-79.65, 7.6) * mm});
            skLineSegment(sketch, "E1152", {"start": v(-79.65, 7.6) * mm, "end": v(-79.03, 8.81) * mm});
            skLineSegment(sketch, "E1153", {"start": v(-79.03, 8.81) * mm, "end": v(-77.66, 11.2) * mm});
            skLineSegment(sketch, "E1154", {"start": v(-77.66, 11.2) * mm, "end": v(-77.57, 11.36) * mm});
            skLineSegment(sketch, "E1155", {"start": v(-77.57, 11.36) * mm, "end": v(-74.44, 11.17) * mm});
            skLineSegment(sketch, "E1156", {"start": v(-74.44, 11.17) * mm, "end": v(-72.34, 10.97) * mm});
            skLineSegment(sketch, "E1157", {"start": v(-72.34, 10.97) * mm, "end": v(-71.38, 10.85) * mm});
            skLineSegment(sketch, "E1158", {"start": v(-71.38, 10.85) * mm, "end": v(-70.13, 12.6) * mm});
            skLineSegment(sketch, "E1159", {"start": v(-70.13, 12.6) * mm, "end": v(-68.7, 14.42) * mm});
            skLineSegment(sketch, "E1160", {"start": v(-68.7, 14.42) * mm, "end": v(-69.05, 15.34) * mm});
            skLineSegment(sketch, "E1161", {"start": v(-69.05, 15.34) * mm, "end": v(-69.75, 17.4) * mm});
            skLineSegment(sketch, "E1162", {"start": v(-69.75, 17.4) * mm, "end": v(-70.4, 19.52) * mm});
            skLineSegment(sketch, "E1163", {"start": v(-70.4, 19.52) * mm, "end": v(-70.66, 20.48) * mm});
            skLineSegment(sketch, "E1164", {"start": v(-70.66, 20.48) * mm, "end": v(-69.18, 22.04) * mm});
            skLineSegment(sketch, "E1165", {"start": v(-69.18, 22.04) * mm, "end": v(-67.63, 23.52) * mm});
            skLineSegment(sketch, "E1166", {"start": v(-67.63, 23.52) * mm, "end": v(-64.68, 22.51) * mm});
            skLineSegment(sketch, "E1167", {"start": v(-64.68, 22.51) * mm, "end": v(-61.81, 21.38) * mm});
            skLineSegment(sketch, "E1168", {"start": v(-61.81, 21.38) * mm, "end": v(-61.67, 21.5) * mm});
            skLineSegment(sketch, "E1169", {"start": v(-61.67, 21.5) * mm, "end": v(-61.3, 21.8) * mm});
            skLineSegment(sketch, "E1170", {"start": v(-61.3, 21.8) * mm, "end": v(-59.5, 23.21) * mm});
            skLineSegment(sketch, "E1171", {"start": v(-59.5, 23.21) * mm, "end": v(-58.28, 24.09) * mm});
            skLineSegment(sketch, "E1172", {"start": v(-58.28, 24.09) * mm, "end": v(-58.44, 26.1) * mm});
            skLineSegment(sketch, "E1173", {"start": v(-58.44, 26.1) * mm, "end": v(-58.5, 27.25) * mm});
            skLineSegment(sketch, "E1174", {"start": v(-58.5, 27.25) * mm, "end": v(-58.54, 30.47) * mm});
            skLineSegment(sketch, "E1175", {"start": v(-58.54, 30.47) * mm, "end": v(-58.39, 30.57) * mm});
            skLineSegment(sketch, "E1176", {"start": v(-58.39, 30.57) * mm, "end": v(-57.97, 30.82) * mm});
            skLineSegment(sketch, "E1177", {"start": v(-57.97, 30.82) * mm, "end": v(-55.4, 32.27) * mm});
            skLineSegment(sketch, "E1178", {"start": v(-55.4, 32.27) * mm, "end": v(-54.8, 32.58) * mm});
            skLineSegment(sketch, "E1179", {"start": v(-54.8, 32.58) * mm, "end": v(-52.24, 30.82) * mm});
            skLineSegment(sketch, "E1180", {"start": v(-52.24, 30.82) * mm, "end": v(-50.53, 29.54) * mm});
            skLineSegment(sketch, "E1181", {"start": v(-50.53, 29.54) * mm, "end": v(-49.78, 28.94) * mm});
            skLineSegment(sketch, "E1182", {"start": v(-49.78, 28.94) * mm, "end": v(-48.53, 29.5) * mm});
            skLineSegment(sketch, "E1183", {"start": v(-48.53, 29.5) * mm, "end": v(-46.42, 30.33) * mm});
            skLineSegment(sketch, "E1184", {"start": v(-46.42, 30.33) * mm, "end": v(-45.96, 30.5) * mm});
            skLineSegment(sketch, "E1185", {"start": v(-45.96, 30.5) * mm, "end": v(-45.64, 30.6) * mm});
            skLineSegment(sketch, "E1186", {"start": v(-45.64, 30.6) * mm, "end": v(-45, 33.71) * mm});
            skLineSegment(sketch, "E1187", {"start": v(-45, 33.71) * mm, "end": v(-44.44, 35.84) * mm});
            skLineSegment(sketch, "E1188", {"start": v(-44.44, 35.84) * mm, "end": v(-44.17, 36.8) * mm});
            skLineSegment(sketch, "E1189", {"start": v(-44.17, 36.8) * mm, "end": v(-43.52, 36.99) * mm});
            skLineSegment(sketch, "E1190", {"start": v(-43.52, 36.99) * mm, "end": v(-42.1, 37.36) * mm});
            skLineSegment(sketch, "E1191", {"start": v(-42.1, 37.36) * mm, "end": v(-40, 37.85) * mm});
            skLineSegment(sketch, "E1192", {"start": v(-40, 37.85) * mm, "end": v(-39.36, 37.1) * mm});
            skLineSegment(sketch, "E1193", {"start": v(-39.36, 37.1) * mm, "end": v(-38, 35.43) * mm});
            skLineSegment(sketch, "E1194", {"start": v(-38, 35.43) * mm, "end": v(-36.71, 33.75) * mm});
            skLineSegment(sketch, "E1195", {"start": v(-36.71, 33.75) * mm, "end": v(-36.15, 32.98) * mm});
            skLineSegment(sketch, "E1196", {"start": v(-36.15, 32.98) * mm, "end": v(-34, 33.25) * mm});
            skLineSegment(sketch, "E1197", {"start": v(-34, 33.25) * mm, "end": v(-31.72, 33.44) * mm});
            skLineSegment(sketch, "E1198", {"start": v(-31.72, 33.44) * mm, "end": v(-30.25, 36.25) * mm});
            skLineSegment(sketch, "E1199", {"start": v(-30.25, 36.25) * mm, "end": v(-28.62, 39.03) * mm});
            skLineSegment(sketch, "E1200", {"start": v(-28.62, 39.03) * mm, "end": v(-27.95, 39.03) * mm});
            skLineSegment(sketch, "E1201", {"start": v(-27.95, 39.03) * mm, "end": v(-26.47, 39) * mm});
            skLineSegment(sketch, "E1202", {"start": v(-26.47, 39) * mm, "end": v(-24.33, 38.89) * mm});
            skLineSegment(sketch, "E1203", {"start": v(-24.33, 38.89) * mm, "end": v(-23.05, 36.05) * mm});
            skLineSegment(sketch, "E1204", {"start": v(-23.05, 36.05) * mm, "end": v(-22.26, 34.07) * mm});
            skLineSegment(sketch, "E1205", {"start": v(-22.26, 34.07) * mm, "end": v(-21.92, 33.17) * mm});
            skLineSegment(sketch, "E1206", {"start": v(-21.92, 33.17) * mm, "end": v(-21.26, 33.08) * mm});
            skLineSegment(sketch, "E1207", {"start": v(-21.26, 33.08) * mm, "end": v(-19.79, 32.87) * mm});
            skLineSegment(sketch, "E1208", {"start": v(-19.79, 32.87) * mm, "end": v(-17.85, 32.52) * mm});
            skLineSegment(sketch, "E1209", {"start": v(-17.85, 32.52) * mm, "end": v(-17.67, 32.48) * mm});
            skLineSegment(sketch, "E1210", {"start": v(-17.67, 32.48) * mm, "end": v(-17.53, 32.45) * mm});
            skLineSegment(sketch, "E1211", {"start": v(-17.53, 32.45) * mm, "end": v(-15.36, 34.76) * mm});
            skLineSegment(sketch, "E1212", {"start": v(-15.36, 34.76) * mm, "end": v(-13.05, 36.98) * mm});
            skLineSegment(sketch, "E1213", {"start": v(-13.05, 36.98) * mm, "end": v(-10.98, 36.39) * mm});
            skLineSegment(sketch, "E1214", {"start": v(-10.98, 36.39) * mm, "end": v(-8.95, 35.7) * mm});
            skLineSegment(sketch, "E1215", {"start": v(-8.95, 35.7) * mm, "end": v(-8.78, 34.74) * mm});
            skLineSegment(sketch, "E1216", {"start": v(-8.78, 34.74) * mm, "end": v(-8.5, 32.6) * mm});
            skLineSegment(sketch, "E1217", {"start": v(-8.5, 32.6) * mm, "end": v(-8.18, 29.55) * mm});
            skLineSegment(sketch, "E1218", {"start": v(-8.18, 29.55) * mm, "end": v(-8, 29.48) * mm});
            skLineSegment(sketch, "E1219", {"start": v(-8, 29.48) * mm, "end": v(-6.21, 28.67) * mm});
            skLineSegment(sketch, "E1220", {"start": v(-6.21, 28.67) * mm, "end": v(-4.88, 28.02) * mm});
            skLineSegment(sketch, "E1221", {"start": v(-4.88, 28.02) * mm, "end": v(-4.15, 27.65) * mm});
            skLineSegment(sketch, "E1222", {"start": v(-4.15, 27.65) * mm, "end": v(-3.31, 28.18) * mm});
            skLineSegment(sketch, "E1223", {"start": v(-3.31, 28.18) * mm, "end": v(-1.44, 29.29) * mm});
            skLineSegment(sketch, "E1224", {"start": v(-1.44, 29.29) * mm, "end": v(1.4, 30.8) * mm});
            skLineSegment(sketch, "E1225", {"start": v(1.4, 30.8) * mm, "end": v(1.97, 30.46) * mm});
            skLineSegment(sketch, "E1226", {"start": v(1.97, 30.46) * mm, "end": v(3.88, 29.23) * mm});
            skLineSegment(sketch, "E1227", {"start": v(3.88, 29.23) * mm, "end": v(4.99, 28.45) * mm});
            skLineSegment(sketch, "E1228", {"start": v(4.99, 28.45) * mm, "end": v(4.6, 25.37) * mm});
            skLineSegment(sketch, "E1229", {"start": v(4.6, 25.37) * mm, "end": v(4.06, 22.31) * mm});
            skLineSegment(sketch, "E1230", {"start": v(4.06, 22.31) * mm, "end": v(4.6, 21.9) * mm});
            skLineSegment(sketch, "E1231", {"start": v(4.6, 21.9) * mm, "end": v(6.84, 19.97) * mm});
            skLineSegment(sketch, "E1232", {"start": v(6.84, 19.97) * mm, "end": v(7.44, 19.4) * mm});
            skLineSegment(sketch, "E1233", {"start": v(7.44, 19.4) * mm, "end": v(10.5, 20.26) * mm});
            skLineSegment(sketch, "E1234", {"start": v(10.5, 20.26) * mm, "end": v(13.63, 20.95) * mm});
            skLineSegment(sketch, "E1235", {"start": v(13.63, 20.95) * mm, "end": v(14.09, 20.47) * mm});
            skLineSegment(sketch, "E1236", {"start": v(14.09, 20.47) * mm, "end": v(16.04, 18.25) * mm});
            skLineSegment(sketch, "E1237", {"start": v(16.04, 18.25) * mm, "end": v(16.35, 17.87) * mm});
            skLineSegment(sketch, "E1238", {"start": v(16.35, 17.87) * mm, "end": v(16.46, 17.73) * mm});
            skLineSegment(sketch, "E1239", {"start": v(16.46, 17.73) * mm, "end": v(15.25, 14.85) * mm});
            skLineSegment(sketch, "E1240", {"start": v(15.25, 14.85) * mm, "end": v(13.92, 12.06) * mm});
            skLineSegment(sketch, "E1241", {"start": v(13.92, 12.06) * mm, "end": v(15.16, 10.3) * mm});
            skLineSegment(sketch, "E1242", {"start": v(15.16, 10.3) * mm, "end": v(16.32, 8.48) * mm});
            skLineSegment(sketch, "E1243", {"start": v(16.32, 8.48) * mm, "end": v(16.4, 8.36) * mm});
            skLineSegment(sketch, "E1244", {"start": v(16.4, 8.36) * mm, "end": v(19.56, 8.35) * mm});
            skLineSegment(sketch, "E1245", {"start": v(19.56, 8.35) * mm, "end": v(21.77, 8.26) * mm});
            skLineSegment(sketch, "E1246", {"start": v(21.77, 8.26) * mm, "end": v(22.76, 8.18) * mm});
            skLineSegment(sketch, "E1247", {"start": v(22.76, 8.18) * mm, "end": v(23.74, 6.27) * mm});
            skLineSegment(sketch, "E1248", {"start": v(23.74, 6.27) * mm, "end": v(24.62, 4.3) * mm});
            skLineSegment(sketch, "E1249", {"start": v(24.62, 4.3) * mm, "end": v(24.04, 3.53) * mm});
            skLineSegment(sketch, "E1250", {"start": v(24.04, 3.53) * mm, "end": v(22.68, 1.86) * mm});
            skLineSegment(sketch, "E1251", {"start": v(22.68, 1.86) * mm, "end": v(20.65, -0.46) * mm});
            skLineSegment(sketch, "E1252", {"start": v(20.65, -0.46) * mm, "end": v(20.88, -1.09) * mm});
            skLineSegment(sketch, "E1253", {"start": v(20.88, -1.09) * mm, "end": v(21.36, -2.5) * mm});
            skLineSegment(sketch, "E1254", {"start": v(21.36, -2.5) * mm, "end": v(21.8, -3.9) * mm});
            skLineSegment(sketch, "E1255", {"start": v(21.8, -3.9) * mm, "end": v(22.02, -4.7) * mm});
            skLineSegment(sketch, "E1256", {"start": v(22.02, -4.7) * mm, "end": v(22.97, -4.95) * mm});
            skLineSegment(sketch, "E1257", {"start": v(22.97, -4.95) * mm, "end": v(25.07, -5.56) * mm});
            skLineSegment(sketch, "E1258", {"start": v(25.07, -5.56) * mm, "end": v(28.11, -6.6) * mm});
            skLineSegment(sketch, "E1259", {"start": v(28.11, -6.6) * mm, "end": v(28.15, -6.77) * mm});
            skLineSegment(sketch, "E1260", {"start": v(28.15, -6.77) * mm, "end": v(28.25, -7.25) * mm});
            skLineSegment(sketch, "E1261", {"start": v(28.25, -7.25) * mm, "end": v(28.51, -8.7) * mm});
            skLineSegment(sketch, "E1262", {"start": v(28.51, -8.7) * mm, "end": v(28.84, -10.83) * mm});
            skLineSegment(sketch, "E1263", {"start": v(28.84, -10.83) * mm, "end": v(26.32, -12.65) * mm});
            skLineSegment(sketch, "E1264", {"start": v(26.32, -12.65) * mm, "end": v(24.54, -13.82) * mm});
            skLineSegment(sketch, "E1265", {"start": v(24.54, -13.82) * mm, "end": v(23.72, -14.33) * mm});
            skLineSegment(sketch, "E1266", {"start": v(23.72, -14.33) * mm, "end": v(23.77, -15) * mm});
            skLineSegment(sketch, "E1267", {"start": v(23.77, -15) * mm, "end": v(23.86, -16.49) * mm});
            skLineSegment(sketch, "E1268", {"start": v(23.86, -16.49) * mm, "end": v(23.91, -18.64) * mm});
            skLineSegment(sketch, "E1269", {"start": v(23.91, -18.64) * mm, "end": v(23.91, -18.79) * mm});
            skLineSegment(sketch, "E1270", {"start": v(-28.36, -17.63) * mm, "end": v(-29.02, -17.9) * mm});
            skLineSegment(sketch, "E1271", {"start": v(-29.02, -17.9) * mm, "end": v(-29.3, -18.57) * mm});
            skLineSegment(sketch, "E1272", {"start": v(-29.3, -18.57) * mm, "end": v(-29.02, -19.24) * mm});
            skLineSegment(sketch, "E1273", {"start": v(-29.02, -19.24) * mm, "end": v(-28.36, -19.52) * mm});
            skLineSegment(sketch, "E1274", {"start": v(-28.36, -19.52) * mm, "end": v(-27.7, -19.24) * mm});
            skLineSegment(sketch, "E1275", {"start": v(-27.7, -19.24) * mm, "end": v(-27.42, -18.57) * mm});
            skLineSegment(sketch, "E1276", {"start": v(-27.42, -18.57) * mm, "end": v(-27.7, -17.9) * mm});
            skLineSegment(sketch, "E1277", {"start": v(-27.7, -17.9) * mm, "end": v(-28.36, -17.63) * mm});
            skLineSegment(sketch, "E1278", {"start": v(-40.68, 91.45) * mm, "end": v(-43.38, 93.06) * mm});
            skLineSegment(sketch, "E1279", {"start": v(-43.38, 93.06) * mm, "end": v(-45.2, 94.29) * mm});
            skLineSegment(sketch, "E1280", {"start": v(-45.2, 94.29) * mm, "end": v(-46, 94.88) * mm});
            skLineSegment(sketch, "E1281", {"start": v(-46, 94.88) * mm, "end": v(-45.78, 96.99) * mm});
            skLineSegment(sketch, "E1282", {"start": v(-45.78, 96.99) * mm, "end": v(-45.47, 99.09) * mm});
            skLineSegment(sketch, "E1283", {"start": v(-45.47, 99.09) * mm, "end": v(-44.54, 99.4) * mm});
            skLineSegment(sketch, "E1284", {"start": v(-44.54, 99.4) * mm, "end": v(-42.5, 100.02) * mm});
            skLineSegment(sketch, "E1285", {"start": v(-42.5, 100.02) * mm, "end": v(-39.53, 100.76) * mm});
            skLineSegment(sketch, "E1286", {"start": v(-39.53, 100.76) * mm, "end": v(-39.5, 100.93) * mm});
            skLineSegment(sketch, "E1287", {"start": v(-39.5, 100.93) * mm, "end": v(-39.37, 101.38) * mm});
            skLineSegment(sketch, "E1288", {"start": v(-39.37, 101.38) * mm, "end": v(-38.99, 102.75) * mm});
            skLineSegment(sketch, "E1289", {"start": v(-38.99, 102.75) * mm, "end": v(-38.34, 104.7) * mm});
            skLineSegment(sketch, "E1290", {"start": v(-38.34, 104.7) * mm, "end": v(-38.29, 104.84) * mm});
            skLineSegment(sketch, "E1291", {"start": v(-38.29, 104.84) * mm, "end": v(-40.27, 107.27) * mm});
            skLineSegment(sketch, "E1292", {"start": v(-40.27, 107.27) * mm, "end": v(-41.55, 109.05) * mm});
            skLineSegment(sketch, "E1293", {"start": v(-41.55, 109.05) * mm, "end": v(-42.1, 109.88) * mm});
            skLineSegment(sketch, "E1294", {"start": v(-42.1, 109.88) * mm, "end": v(-41.83, 110.49) * mm});
            skLineSegment(sketch, "E1295", {"start": v(-41.83, 110.49) * mm, "end": v(-41.18, 111.79) * mm});
            skLineSegment(sketch, "E1296", {"start": v(-41.18, 111.79) * mm, "end": v(-40.49, 113.08) * mm});
            skLineSegment(sketch, "E1297", {"start": v(-40.49, 113.08) * mm, "end": v(-40.16, 113.65) * mm});
            skLineSegment(sketch, "E1298", {"start": v(-40.16, 113.65) * mm, "end": v(-39.18, 113.63) * mm});
            skLineSegment(sketch, "E1299", {"start": v(-39.18, 113.63) * mm, "end": v(-37.05, 113.5) * mm});
            skLineSegment(sketch, "E1300", {"start": v(-37.05, 113.5) * mm, "end": v(-34.02, 113.18) * mm});
            skLineSegment(sketch, "E1301", {"start": v(-34.02, 113.18) * mm, "end": v(-32.81, 114.86) * mm});
            skLineSegment(sketch, "E1302", {"start": v(-32.81, 114.86) * mm, "end": v(-31.64, 116.34) * mm});
            skLineSegment(sketch, "E1303", {"start": v(-31.64, 116.34) * mm, "end": v(-31.43, 116.58) * mm});
            skLineSegment(sketch, "E1304", {"start": v(-31.43, 116.58) * mm, "end": v(-32.47, 119.56) * mm});
            skLineSegment(sketch, "E1305", {"start": v(-32.47, 119.56) * mm, "end": v(-33.3, 122.64) * mm});
            skLineSegment(sketch, "E1306", {"start": v(-33.3, 122.64) * mm, "end": v(-32.84, 123.1) * mm});
            skLineSegment(sketch, "E1307", {"start": v(-32.84, 123.1) * mm, "end": v(-31.78, 124.11) * mm});
            skLineSegment(sketch, "E1308", {"start": v(-31.78, 124.11) * mm, "end": v(-30.19, 125.51) * mm});
            skLineSegment(sketch, "E1309", {"start": v(-30.19, 125.51) * mm, "end": v(-29.28, 125.16) * mm});
            skLineSegment(sketch, "E1310", {"start": v(-29.28, 125.16) * mm, "end": v(-27.32, 124.31) * mm});
            skLineSegment(sketch, "E1311", {"start": v(-27.32, 124.31) * mm, "end": v(-25.42, 123.41) * mm});
            skLineSegment(sketch, "E1312", {"start": v(-25.42, 123.41) * mm, "end": v(-24.57, 122.97) * mm});
            skLineSegment(sketch, "E1313", {"start": v(-24.57, 122.97) * mm, "end": v(-23.5, 123.73) * mm});
            skLineSegment(sketch, "E1314", {"start": v(-23.5, 123.73) * mm, "end": v(-21.66, 124.9) * mm});
            skLineSegment(sketch, "E1315", {"start": v(-21.66, 124.9) * mm, "end": v(-20.98, 125.29) * mm});
            skLineSegment(sketch, "E1316", {"start": v(-20.98, 125.29) * mm, "end": v(-21, 126.27) * mm});
            skLineSegment(sketch, "E1317", {"start": v(-21, 126.27) * mm, "end": v(-20.98, 127.28) * mm});
            skLineSegment(sketch, "E1318", {"start": v(-20.98, 127.28) * mm, "end": v(-20.94, 128.43) * mm});
            skLineSegment(sketch, "E1319", {"start": v(-20.94, 128.43) * mm, "end": v(-20.79, 130.62) * mm});
            skLineSegment(sketch, "E1320", {"start": v(-20.79, 130.62) * mm, "end": v(-20.68, 131.62) * mm});
            skLineSegment(sketch, "E1321", {"start": v(-20.68, 131.62) * mm, "end": v(-18.74, 132.5) * mm});
            skLineSegment(sketch, "E1322", {"start": v(-18.74, 132.5) * mm, "end": v(-16.94, 133.2) * mm});
            skLineSegment(sketch, "E1323", {"start": v(-16.94, 133.2) * mm, "end": v(-16.76, 133.27) * mm});
            skLineSegment(sketch, "E1324", {"start": v(-16.76, 133.27) * mm, "end": v(-14.48, 131.15) * mm});
            skLineSegment(sketch, "E1325", {"start": v(-14.48, 131.15) * mm, "end": v(-13.68, 130.36) * mm});
            skLineSegment(sketch, "E1326", {"start": v(-13.68, 130.36) * mm, "end": v(-12.35, 128.94) * mm});
            skLineSegment(sketch, "E1327", {"start": v(-12.35, 128.94) * mm, "end": v(-11.73, 129.12) * mm});
            skLineSegment(sketch, "E1328", {"start": v(-11.73, 129.12) * mm, "end": v(-10.36, 129.46) * mm});
            skLineSegment(sketch, "E1329", {"start": v(-10.36, 129.46) * mm, "end": v(-8.97, 129.75) * mm});
            skLineSegment(sketch, "E1330", {"start": v(-8.97, 129.75) * mm, "end": v(-8.2, 129.9) * mm});
            skLineSegment(sketch, "E1331", {"start": v(-8.2, 129.9) * mm, "end": v(-7.07, 132.83) * mm});
            skLineSegment(sketch, "E1332", {"start": v(-7.07, 132.83) * mm, "end": v(-6.18, 134.83) * mm});
            skLineSegment(sketch, "E1333", {"start": v(-6.18, 134.83) * mm, "end": v(-5.73, 135.73) * mm});
            skLineSegment(sketch, "E1334", {"start": v(-5.73, 135.73) * mm, "end": v(-3.62, 135.88) * mm});
            skLineSegment(sketch, "E1335", {"start": v(-3.62, 135.88) * mm, "end": v(-1.5, 135.94) * mm});
            skLineSegment(sketch, "E1336", {"start": v(-1.5, 135.94) * mm, "end": v(-0.07, 133.17) * mm});
            skLineSegment(sketch, "E1337", {"start": v(-0.07, 133.17) * mm, "end": v(0.8, 131.25) * mm});
            skLineSegment(sketch, "E1338", {"start": v(0.8, 131.25) * mm, "end": v(1.17, 130.37) * mm});
            skLineSegment(sketch, "E1339", {"start": v(1.17, 130.37) * mm, "end": v(2.48, 130.27) * mm});
            skLineSegment(sketch, "E1340", {"start": v(2.48, 130.27) * mm, "end": v(4.64, 129.98) * mm});
            skLineSegment(sketch, "E1341", {"start": v(4.64, 129.98) * mm, "end": v(5.4, 129.84) * mm});
            skLineSegment(sketch, "E1342", {"start": v(5.4, 129.84) * mm, "end": v(6.03, 130.6) * mm});
            skLineSegment(sketch, "E1343", {"start": v(6.03, 130.6) * mm, "end": v(6.69, 131.37) * mm});
            skLineSegment(sketch, "E1344", {"start": v(6.69, 131.37) * mm, "end": v(7.46, 132.22) * mm});
            skLineSegment(sketch, "E1345", {"start": v(7.46, 132.22) * mm, "end": v(8.99, 133.8) * mm});
            skLineSegment(sketch, "E1346", {"start": v(8.99, 133.8) * mm, "end": v(9.71, 134.5) * mm});
            skLineSegment(sketch, "E1347", {"start": v(9.71, 134.5) * mm, "end": v(11.76, 133.93) * mm});
            skLineSegment(sketch, "E1348", {"start": v(11.76, 133.93) * mm, "end": v(13.77, 133.24) * mm});
            skLineSegment(sketch, "E1349", {"start": v(13.77, 133.24) * mm, "end": v(13.91, 132.27) * mm});
            skLineSegment(sketch, "E1350", {"start": v(13.91, 132.27) * mm, "end": v(14.16, 130.15) * mm});
            skLineSegment(sketch, "E1351", {"start": v(14.16, 130.15) * mm, "end": v(14.33, 128.05) * mm});
            skLineSegment(sketch, "E1352", {"start": v(14.33, 128.05) * mm, "end": v(14.37, 127.1) * mm});
            skLineSegment(sketch, "E1353", {"start": v(14.37, 127.1) * mm, "end": v(14.95, 126.83) * mm});
            skLineSegment(sketch, "E1354", {"start": v(14.95, 126.83) * mm, "end": v(16.23, 126.2) * mm});
            skLineSegment(sketch, "E1355", {"start": v(16.23, 126.2) * mm, "end": v(17.48, 125.54) * mm});
            skLineSegment(sketch, "E1356", {"start": v(17.48, 125.54) * mm, "end": v(18.16, 125.15) * mm});
            skLineSegment(sketch, "E1357", {"start": v(18.16, 125.15) * mm, "end": v(20.91, 126.68) * mm});
            skLineSegment(sketch, "E1358", {"start": v(20.91, 126.68) * mm, "end": v(22.89, 127.64) * mm});
            skLineSegment(sketch, "E1359", {"start": v(22.89, 127.64) * mm, "end": v(23.8, 128.04) * mm});
            skLineSegment(sketch, "E1360", {"start": v(23.8, 128.04) * mm, "end": v(25.52, 126.8) * mm});
            skLineSegment(sketch, "E1361", {"start": v(25.52, 126.8) * mm, "end": v(26.67, 125.9) * mm});
            skLineSegment(sketch, "E1362", {"start": v(26.67, 125.9) * mm, "end": v(27.04, 125.59) * mm});
            skLineSegment(sketch, "E1363", {"start": v(27.04, 125.59) * mm, "end": v(27.18, 125.47) * mm});
            skLineSegment(sketch, "E1364", {"start": v(27.18, 125.47) * mm, "end": v(26.5, 122.44) * mm});
            skLineSegment(sketch, "E1365", {"start": v(26.5, 122.44) * mm, "end": v(25.93, 120.4) * mm});
            skLineSegment(sketch, "E1366", {"start": v(25.93, 120.4) * mm, "end": v(25.64, 119.5) * mm});
            skLineSegment(sketch, "E1367", {"start": v(25.64, 119.5) * mm, "end": v(26.1, 119.05) * mm});
            skLineSegment(sketch, "E1368", {"start": v(26.1, 119.05) * mm, "end": v(27.1, 118.02) * mm});
            skLineSegment(sketch, "E1369", {"start": v(27.1, 118.02) * mm, "end": v(28.56, 116.37) * mm});
            skLineSegment(sketch, "E1370", {"start": v(28.56, 116.37) * mm, "end": v(29.51, 116.55) * mm});
            skLineSegment(sketch, "E1371", {"start": v(29.51, 116.55) * mm, "end": v(31.65, 116.87) * mm});
            skLineSegment(sketch, "E1372", {"start": v(31.65, 116.87) * mm, "end": v(32.82, 117) * mm});
            skLineSegment(sketch, "E1373", {"start": v(32.82, 117) * mm, "end": v(33.83, 117.1) * mm});
            skLineSegment(sketch, "E1374", {"start": v(33.83, 117.1) * mm, "end": v(34.83, 117.16) * mm});
            skLineSegment(sketch, "E1375", {"start": v(34.83, 117.16) * mm, "end": v(35.22, 116.62) * mm});
            skLineSegment(sketch, "E1376", {"start": v(35.22, 116.62) * mm, "end": v(36.02, 115.4) * mm});
            skLineSegment(sketch, "E1377", {"start": v(36.02, 115.4) * mm, "end": v(37.13, 113.6) * mm});
            skLineSegment(sketch, "E1378", {"start": v(37.13, 113.6) * mm, "end": v(36.62, 112.76) * mm});
            skLineSegment(sketch, "E1379", {"start": v(36.62, 112.76) * mm, "end": v(35.46, 110.98) * mm});
            skLineSegment(sketch, "E1380", {"start": v(35.46, 110.98) * mm, "end": v(33.66, 108.5) * mm});
            skLineSegment(sketch, "E1381", {"start": v(33.66, 108.5) * mm, "end": v(33.93, 107.92) * mm});
            skLineSegment(sketch, "E1382", {"start": v(33.93, 107.92) * mm, "end": v(34.52, 106.63) * mm});
            skLineSegment(sketch, "E1383", {"start": v(34.52, 106.63) * mm, "end": v(35.21, 104.87) * mm});
            skLineSegment(sketch, "E1384", {"start": v(35.21, 104.87) * mm, "end": v(35.28, 104.7) * mm});
            skLineSegment(sketch, "E1385", {"start": v(35.28, 104.7) * mm, "end": v(35.32, 104.57) * mm});
            skLineSegment(sketch, "E1386", {"start": v(35.32, 104.57) * mm, "end": v(38.4, 103.98) * mm});
            skLineSegment(sketch, "E1387", {"start": v(38.4, 103.98) * mm, "end": v(40.52, 103.45) * mm});
            skLineSegment(sketch, "E1388", {"start": v(40.52, 103.45) * mm, "end": v(41.5, 103.17) * mm});
            skLineSegment(sketch, "E1389", {"start": v(41.5, 103.17) * mm, "end": v(41.67, 102.53) * mm});
            skLineSegment(sketch, "E1390", {"start": v(41.67, 102.53) * mm, "end": v(42.18, 100.35) * mm});
            skLineSegment(sketch, "E1391", {"start": v(42.18, 100.35) * mm, "end": v(42.42, 99.02) * mm});
            skLineSegment(sketch, "E1392", {"start": v(42.42, 99.02) * mm, "end": v(41.66, 98.42) * mm});
            skLineSegment(sketch, "E1393", {"start": v(41.66, 98.42) * mm, "end": v(39.95, 97.14) * mm});
            skLineSegment(sketch, "E1394", {"start": v(39.95, 97.14) * mm, "end": v(37.41, 95.44) * mm});
            skLineSegment(sketch, "E1395", {"start": v(37.41, 95.44) * mm, "end": v(37.43, 95.26) * mm});
            skLineSegment(sketch, "E1396", {"start": v(37.43, 95.26) * mm, "end": v(37.57, 93.38) * mm});
            skLineSegment(sketch, "E1397", {"start": v(37.57, 93.38) * mm, "end": v(37.63, 91.31) * mm});
            skLineSegment(sketch, "E1398", {"start": v(37.63, 91.31) * mm, "end": v(37.62, 91.17) * mm});
            skLineSegment(sketch, "E1399", {"start": v(37.62, 91.17) * mm, "end": v(40.32, 89.56) * mm});
            skLineSegment(sketch, "E1400", {"start": v(40.32, 89.56) * mm, "end": v(42.13, 88.33) * mm});
            skLineSegment(sketch, "E1401", {"start": v(42.13, 88.33) * mm, "end": v(42.94, 87.74) * mm});
            skLineSegment(sketch, "E1402", {"start": v(42.94, 87.74) * mm, "end": v(42.73, 85.63) * mm});
            skLineSegment(sketch, "E1403", {"start": v(42.73, 85.63) * mm, "end": v(42.4, 83.53) * mm});
            skLineSegment(sketch, "E1404", {"start": v(42.4, 83.53) * mm, "end": v(41.48, 83.22) * mm});
            skLineSegment(sketch, "E1405", {"start": v(41.48, 83.22) * mm, "end": v(39.45, 82.6) * mm});
            skLineSegment(sketch, "E1406", {"start": v(39.45, 82.6) * mm, "end": v(36.47, 81.86) * mm});
            skLineSegment(sketch, "E1407", {"start": v(36.47, 81.86) * mm, "end": v(36.43, 81.7) * mm});
            skLineSegment(sketch, "E1408", {"start": v(36.43, 81.7) * mm, "end": v(36.32, 81.24) * mm});
            skLineSegment(sketch, "E1409", {"start": v(36.32, 81.24) * mm, "end": v(35.93, 79.87) * mm});
            skLineSegment(sketch, "E1410", {"start": v(35.93, 79.87) * mm, "end": v(35.28, 77.91) * mm});
            skLineSegment(sketch, "E1411", {"start": v(35.28, 77.91) * mm, "end": v(35.23, 77.78) * mm});
            skLineSegment(sketch, "E1412", {"start": v(35.23, 77.78) * mm, "end": v(37.2, 75.35) * mm});
            skLineSegment(sketch, "E1413", {"start": v(37.2, 75.35) * mm, "end": v(38.49, 73.57) * mm});
            skLineSegment(sketch, "E1414", {"start": v(38.49, 73.57) * mm, "end": v(39.05, 72.74) * mm});
            skLineSegment(sketch, "E1415", {"start": v(39.05, 72.74) * mm, "end": v(38.77, 72.14) * mm});
            skLineSegment(sketch, "E1416", {"start": v(38.77, 72.14) * mm, "end": v(38.12, 70.83) * mm});
            skLineSegment(sketch, "E1417", {"start": v(38.12, 70.83) * mm, "end": v(37.43, 69.55) * mm});
            skLineSegment(sketch, "E1418", {"start": v(37.43, 69.55) * mm, "end": v(37.1, 68.97) * mm});
            skLineSegment(sketch, "E1419", {"start": v(37.1, 68.97) * mm, "end": v(36.12, 69) * mm});
            skLineSegment(sketch, "E1420", {"start": v(36.12, 69) * mm, "end": v(34, 69.12) * mm});
            skLineSegment(sketch, "E1421", {"start": v(34, 69.12) * mm, "end": v(30.96, 69.44) * mm});
            skLineSegment(sketch, "E1422", {"start": v(30.96, 69.44) * mm, "end": v(29.75, 67.76) * mm});
            skLineSegment(sketch, "E1423", {"start": v(29.75, 67.76) * mm, "end": v(28.58, 66.28) * mm});
            skLineSegment(sketch, "E1424", {"start": v(28.58, 66.28) * mm, "end": v(28.37, 66.04) * mm});
            skLineSegment(sketch, "E1425", {"start": v(28.37, 66.04) * mm, "end": v(29.4, 63.07) * mm});
            skLineSegment(sketch, "E1426", {"start": v(29.4, 63.07) * mm, "end": v(30.25, 59.99) * mm});
            skLineSegment(sketch, "E1427", {"start": v(30.25, 59.99) * mm, "end": v(29.78, 59.52) * mm});
            skLineSegment(sketch, "E1428", {"start": v(29.78, 59.52) * mm, "end": v(28.72, 58.51) * mm});
            skLineSegment(sketch, "E1429", {"start": v(28.72, 58.51) * mm, "end": v(27.13, 57.1) * mm});
            skLineSegment(sketch, "E1430", {"start": v(27.13, 57.1) * mm, "end": v(26.22, 57.46) * mm});
            skLineSegment(sketch, "E1431", {"start": v(26.22, 57.46) * mm, "end": v(24.26, 58.3) * mm});
            skLineSegment(sketch, "E1432", {"start": v(24.26, 58.3) * mm, "end": v(22.36, 59.2) * mm});
            skLineSegment(sketch, "E1433", {"start": v(22.36, 59.2) * mm, "end": v(21.5, 59.65) * mm});
            skLineSegment(sketch, "E1434", {"start": v(21.5, 59.65) * mm, "end": v(20.44, 58.9) * mm});
            skLineSegment(sketch, "E1435", {"start": v(20.44, 58.9) * mm, "end": v(18.6, 57.72) * mm});
            skLineSegment(sketch, "E1436", {"start": v(18.6, 57.72) * mm, "end": v(17.92, 57.33) * mm});
            skLineSegment(sketch, "E1437", {"start": v(17.92, 57.33) * mm, "end": v(17.93, 56.35) * mm});
            skLineSegment(sketch, "E1438", {"start": v(17.93, 56.35) * mm, "end": v(17.93, 55.34) * mm});
            skLineSegment(sketch, "E1439", {"start": v(17.93, 55.34) * mm, "end": v(17.88, 54.19) * mm});
            skLineSegment(sketch, "E1440", {"start": v(17.88, 54.19) * mm, "end": v(17.73, 52) * mm});
            skLineSegment(sketch, "E1441", {"start": v(17.73, 52) * mm, "end": v(17.62, 51) * mm});
            skLineSegment(sketch, "E1442", {"start": v(17.62, 51) * mm, "end": v(15.68, 50.13) * mm});
            skLineSegment(sketch, "E1443", {"start": v(15.68, 50.13) * mm, "end": v(13.88, 49.42) * mm});
            skLineSegment(sketch, "E1444", {"start": v(13.88, 49.42) * mm, "end": v(13.7, 49.36) * mm});
            skLineSegment(sketch, "E1445", {"start": v(13.7, 49.36) * mm, "end": v(11.42, 51.47) * mm});
            skLineSegment(sketch, "E1446", {"start": v(11.42, 51.47) * mm, "end": v(10.62, 52.26) * mm});
            skLineSegment(sketch, "E1447", {"start": v(10.62, 52.26) * mm, "end": v(9.3, 53.68) * mm});
            skLineSegment(sketch, "E1448", {"start": v(9.3, 53.68) * mm, "end": v(8.67, 53.5) * mm});
            skLineSegment(sketch, "E1449", {"start": v(8.67, 53.5) * mm, "end": v(7.3, 53.16) * mm});
            skLineSegment(sketch, "E1450", {"start": v(7.3, 53.16) * mm, "end": v(5.9, 52.87) * mm});
            skLineSegment(sketch, "E1451", {"start": v(5.9, 52.87) * mm, "end": v(5.14, 52.73) * mm});
            skLineSegment(sketch, "E1452", {"start": v(5.14, 52.73) * mm, "end": v(4.01, 49.8) * mm});
            skLineSegment(sketch, "E1453", {"start": v(4.01, 49.8) * mm, "end": v(3.12, 47.79) * mm});
            skLineSegment(sketch, "E1454", {"start": v(3.12, 47.79) * mm, "end": v(2.68, 46.89) * mm});
            skLineSegment(sketch, "E1455", {"start": v(2.68, 46.89) * mm, "end": v(0.56, 46.74) * mm});
            skLineSegment(sketch, "E1456", {"start": v(0.56, 46.74) * mm, "end": v(-1.56, 46.69) * mm});
            skLineSegment(sketch, "E1457", {"start": v(-1.56, 46.69) * mm, "end": v(-3, 49.46) * mm});
            skLineSegment(sketch, "E1458", {"start": v(-3, 49.46) * mm, "end": v(-3.86, 51.37) * mm});
            skLineSegment(sketch, "E1459", {"start": v(-3.86, 51.37) * mm, "end": v(-4.23, 52.26) * mm});
            skLineSegment(sketch, "E1460", {"start": v(-4.23, 52.26) * mm, "end": v(-5.54, 52.35) * mm});
            skLineSegment(sketch, "E1461", {"start": v(-5.54, 52.35) * mm, "end": v(-7.7, 52.64) * mm});
            skLineSegment(sketch, "E1462", {"start": v(-7.7, 52.64) * mm, "end": v(-8.47, 52.78) * mm});
            skLineSegment(sketch, "E1463", {"start": v(-8.47, 52.78) * mm, "end": v(-9.1, 52.02) * mm});
            skLineSegment(sketch, "E1464", {"start": v(-9.1, 52.02) * mm, "end": v(-9.75, 51.25) * mm});
            skLineSegment(sketch, "E1465", {"start": v(-9.75, 51.25) * mm, "end": v(-10.52, 50.4) * mm});
            skLineSegment(sketch, "E1466", {"start": v(-10.52, 50.4) * mm, "end": v(-12.05, 48.82) * mm});
            skLineSegment(sketch, "E1467", {"start": v(-12.05, 48.82) * mm, "end": v(-12.77, 48.12) * mm});
            skLineSegment(sketch, "E1468", {"start": v(-12.77, 48.12) * mm, "end": v(-14.81, 48.7) * mm});
            skLineSegment(sketch, "E1469", {"start": v(-14.81, 48.7) * mm, "end": v(-16.83, 49.38) * mm});
            skLineSegment(sketch, "E1470", {"start": v(-16.83, 49.38) * mm, "end": v(-16.97, 50.35) * mm});
            skLineSegment(sketch, "E1471", {"start": v(-16.97, 50.35) * mm, "end": v(-17.22, 52.47) * mm});
            skLineSegment(sketch, "E1472", {"start": v(-17.22, 52.47) * mm, "end": v(-17.38, 54.57) * mm});
            skLineSegment(sketch, "E1473", {"start": v(-17.38, 54.57) * mm, "end": v(-17.43, 55.53) * mm});
            skLineSegment(sketch, "E1474", {"start": v(-17.43, 55.53) * mm, "end": v(-18.01, 55.8) * mm});
            skLineSegment(sketch, "E1475", {"start": v(-18.01, 55.8) * mm, "end": v(-19.29, 56.42) * mm});
            skLineSegment(sketch, "E1476", {"start": v(-19.29, 56.42) * mm, "end": v(-20.54, 57.08) * mm});
            skLineSegment(sketch, "E1477", {"start": v(-20.54, 57.08) * mm, "end": v(-21.22, 57.47) * mm});
            skLineSegment(sketch, "E1478", {"start": v(-21.22, 57.47) * mm, "end": v(-23.97, 55.94) * mm});
            skLineSegment(sketch, "E1479", {"start": v(-23.97, 55.94) * mm, "end": v(-25.95, 54.98) * mm});
            skLineSegment(sketch, "E1480", {"start": v(-25.95, 54.98) * mm, "end": v(-26.86, 54.58) * mm});
            skLineSegment(sketch, "E1481", {"start": v(-26.86, 54.58) * mm, "end": v(-28.58, 55.82) * mm});
            skLineSegment(sketch, "E1482", {"start": v(-28.58, 55.82) * mm, "end": v(-29.73, 56.73) * mm});
            skLineSegment(sketch, "E1483", {"start": v(-29.73, 56.73) * mm, "end": v(-30.1, 57.03) * mm});
            skLineSegment(sketch, "E1484", {"start": v(-30.1, 57.03) * mm, "end": v(-30.24, 57.15) * mm});
            skLineSegment(sketch, "E1485", {"start": v(-30.24, 57.15) * mm, "end": v(-29.56, 60.18) * mm});
            skLineSegment(sketch, "E1486", {"start": v(-29.56, 60.18) * mm, "end": v(-28.98, 62.22) * mm});
            skLineSegment(sketch, "E1487", {"start": v(-28.98, 62.22) * mm, "end": v(-28.7, 63.13) * mm});
            skLineSegment(sketch, "E1488", {"start": v(-28.7, 63.13) * mm, "end": v(-29.17, 63.57) * mm});
            skLineSegment(sketch, "E1489", {"start": v(-29.17, 63.57) * mm, "end": v(-30.15, 64.6) * mm});
            skLineSegment(sketch, "E1490", {"start": v(-30.15, 64.6) * mm, "end": v(-31.61, 66.25) * mm});
            skLineSegment(sketch, "E1491", {"start": v(-31.61, 66.25) * mm, "end": v(-32.57, 66.07) * mm});
            skLineSegment(sketch, "E1492", {"start": v(-32.57, 66.07) * mm, "end": v(-34.71, 65.75) * mm});
            skLineSegment(sketch, "E1493", {"start": v(-34.71, 65.75) * mm, "end": v(-35.88, 65.61) * mm});
            skLineSegment(sketch, "E1494", {"start": v(-35.88, 65.61) * mm, "end": v(-36.9, 65.53) * mm});
            skLineSegment(sketch, "E1495", {"start": v(-36.9, 65.53) * mm, "end": v(-37.9, 65.46) * mm});
            skLineSegment(sketch, "E1496", {"start": v(-37.9, 65.46) * mm, "end": v(-38.28, 66) * mm});
            skLineSegment(sketch, "E1497", {"start": v(-38.28, 66) * mm, "end": v(-39.08, 67.21) * mm});
            skLineSegment(sketch, "E1498", {"start": v(-39.08, 67.21) * mm, "end": v(-40.19, 69.03) * mm});
            skLineSegment(sketch, "E1499", {"start": v(-40.19, 69.03) * mm, "end": v(-39.68, 69.86) * mm});
            skLineSegment(sketch, "E1500", {"start": v(-39.68, 69.86) * mm, "end": v(-38.52, 71.64) * mm});
            skLineSegment(sketch, "E1501", {"start": v(-38.52, 71.64) * mm, "end": v(-36.72, 74.12) * mm});
            skLineSegment(sketch, "E1502", {"start": v(-36.72, 74.12) * mm, "end": v(-37, 74.7) * mm});
            skLineSegment(sketch, "E1503", {"start": v(-37, 74.7) * mm, "end": v(-37.58, 76) * mm});
            skLineSegment(sketch, "E1504", {"start": v(-37.58, 76) * mm, "end": v(-38.27, 77.75) * mm});
            skLineSegment(sketch, "E1505", {"start": v(-38.27, 77.75) * mm, "end": v(-38.34, 77.91) * mm});
            skLineSegment(sketch, "E1506", {"start": v(-38.34, 77.91) * mm, "end": v(-38.38, 78.05) * mm});
            skLineSegment(sketch, "E1507", {"start": v(-38.38, 78.05) * mm, "end": v(-41.47, 78.64) * mm});
            skLineSegment(sketch, "E1508", {"start": v(-41.47, 78.64) * mm, "end": v(-43.58, 79.18) * mm});
            skLineSegment(sketch, "E1509", {"start": v(-43.58, 79.18) * mm, "end": v(-44.55, 79.45) * mm});
            skLineSegment(sketch, "E1510", {"start": v(-44.55, 79.45) * mm, "end": v(-44.73, 80.1) * mm});
            skLineSegment(sketch, "E1511", {"start": v(-44.73, 80.1) * mm, "end": v(-45.24, 82.27) * mm});
            skLineSegment(sketch, "E1512", {"start": v(-45.24, 82.27) * mm, "end": v(-45.48, 83.6) * mm});
            skLineSegment(sketch, "E1513", {"start": v(-45.48, 83.6) * mm, "end": v(-44.72, 84.2) * mm});
            skLineSegment(sketch, "E1514", {"start": v(-44.72, 84.2) * mm, "end": v(-43, 85.48) * mm});
            skLineSegment(sketch, "E1515", {"start": v(-43, 85.48) * mm, "end": v(-40.47, 87.18) * mm});
            skLineSegment(sketch, "E1516", {"start": v(-40.47, 87.18) * mm, "end": v(-40.49, 87.36) * mm});
            skLineSegment(sketch, "E1517", {"start": v(-40.49, 87.36) * mm, "end": v(-40.63, 89.24) * mm});
            skLineSegment(sketch, "E1518", {"start": v(-40.63, 89.24) * mm, "end": v(-40.69, 91.31) * mm});
            skLineSegment(sketch, "E1519", {"start": v(-40.69, 91.31) * mm, "end": v(-40.68, 91.45) * mm});
            skLineSegment(sketch, "E1520", {"start": v(-1.53, 92.43) * mm, "end": v(-2.32, 92.1) * mm});
            skLineSegment(sketch, "E1521", {"start": v(-2.32, 92.1) * mm, "end": v(-2.65, 91.31) * mm});
            skLineSegment(sketch, "E1522", {"start": v(-2.65, 91.31) * mm, "end": v(-2.32, 90.52) * mm});
            skLineSegment(sketch, "E1523", {"start": v(-2.32, 90.52) * mm, "end": v(-1.53, 90.2) * mm});
            skLineSegment(sketch, "E1524", {"start": v(-1.53, 90.2) * mm, "end": v(-0.74, 90.52) * mm});
            skLineSegment(sketch, "E1525", {"start": v(-0.74, 90.52) * mm, "end": v(-0.41, 91.31) * mm});
            skLineSegment(sketch, "E1526", {"start": v(-0.41, 91.31) * mm, "end": v(-0.74, 92.1) * mm});
            skLineSegment(sketch, "E1527", {"start": v(-0.74, 92.1) * mm, "end": v(-1.53, 92.43) * mm});
            skLineSegment(sketch, "E1528", {"start": v(56.84, -103.62) * mm, "end": v(57.68, -104.09) * mm});
            skLineSegment(sketch, "E1529", {"start": v(57.68, -104.09) * mm, "end": v(59.52, -105.2) * mm});
            skLineSegment(sketch, "E1530", {"start": v(59.52, -105.2) * mm, "end": v(61.31, -106.46) * mm});
            skLineSegment(sketch, "E1531", {"start": v(61.31, -106.46) * mm, "end": v(62.1, -107.08) * mm});
            skLineSegment(sketch, "E1532", {"start": v(62.1, -107.08) * mm, "end": v(61.94, -108.42) * mm});
            skLineSegment(sketch, "E1533", {"start": v(61.94, -108.42) * mm, "end": v(61.66, -109.97) * mm});
            skLineSegment(sketch, "E1534", {"start": v(61.66, -109.97) * mm, "end": v(61.36, -111.29) * mm});
            skLineSegment(sketch, "E1535", {"start": v(61.36, -111.29) * mm, "end": v(60.42, -111.53) * mm});
            skLineSegment(sketch, "E1536", {"start": v(60.42, -111.53) * mm, "end": v(58.34, -111.99) * mm});
            skLineSegment(sketch, "E1537", {"start": v(58.34, -111.99) * mm, "end": v(56.26, -112.31) * mm});
            skLineSegment(sketch, "E1538", {"start": v(56.26, -112.31) * mm, "end": v(55.32, -112.42) * mm});
            skLineSegment(sketch, "E1539", {"start": v(55.32, -112.42) * mm, "end": v(55.27, -112.58) * mm});
            skLineSegment(sketch, "E1540", {"start": v(55.27, -112.58) * mm, "end": v(55.12, -113) * mm});
            skLineSegment(sketch, "E1541", {"start": v(55.12, -113) * mm, "end": v(54.6, -114.25) * mm});
            skLineSegment(sketch, "E1542", {"start": v(54.6, -114.25) * mm, "end": v(53.75, -116.03) * mm});
            skLineSegment(sketch, "E1543", {"start": v(53.75, -116.03) * mm, "end": v(53.7, -116.15) * mm});
            skLineSegment(sketch, "E1544", {"start": v(53.7, -116.15) * mm, "end": v(54.23, -116.95) * mm});
            skLineSegment(sketch, "E1545", {"start": v(54.23, -116.95) * mm, "end": v(55.33, -118.8) * mm});
            skLineSegment(sketch, "E1546", {"start": v(55.33, -118.8) * mm, "end": v(56.75, -121.66) * mm});
            skLineSegment(sketch, "E1547", {"start": v(56.75, -121.66) * mm, "end": v(56.36, -122.2) * mm});
            skLineSegment(sketch, "E1548", {"start": v(56.36, -122.2) * mm, "end": v(55.49, -123.39) * mm});
            skLineSegment(sketch, "E1549", {"start": v(55.49, -123.39) * mm, "end": v(54.56, -124.53) * mm});
            skLineSegment(sketch, "E1550", {"start": v(54.56, -124.53) * mm, "end": v(54.12, -125.03) * mm});
            skLineSegment(sketch, "E1551", {"start": v(54.12, -125.03) * mm, "end": v(53.17, -124.81) * mm});
            skLineSegment(sketch, "E1552", {"start": v(53.17, -124.81) * mm, "end": v(51.12, -124.24) * mm});
            skLineSegment(sketch, "E1553", {"start": v(51.12, -124.24) * mm, "end": v(49.13, -123.57) * mm});
            skLineSegment(sketch, "E1554", {"start": v(49.13, -123.57) * mm, "end": v(48.25, -123.23) * mm});
            skLineSegment(sketch, "E1555", {"start": v(48.25, -123.23) * mm, "end": v(48.13, -123.34) * mm});
            skLineSegment(sketch, "E1556", {"start": v(48.13, -123.34) * mm, "end": v(47.8, -123.64) * mm});
            skLineSegment(sketch, "E1557", {"start": v(47.8, -123.64) * mm, "end": v(46.76, -124.52) * mm});
            skLineSegment(sketch, "E1558", {"start": v(46.76, -124.52) * mm, "end": v(45.68, -125.34) * mm});
            skLineSegment(sketch, "E1559", {"start": v(45.68, -125.34) * mm, "end": v(45.07, -125.77) * mm});
            skLineSegment(sketch, "E1560", {"start": v(45.07, -125.77) * mm, "end": v(45.17, -126.74) * mm});
            skLineSegment(sketch, "E1561", {"start": v(45.17, -126.74) * mm, "end": v(45.3, -128.89) * mm});
            skLineSegment(sketch, "E1562", {"start": v(45.3, -128.89) * mm, "end": v(45.28, -131.07) * mm});
            skLineSegment(sketch, "E1563", {"start": v(45.28, -131.07) * mm, "end": v(45.24, -131.8) * mm});
            skLineSegment(sketch, "E1564", {"start": v(45.24, -131.8) * mm, "end": v(45.23, -132.08) * mm});
            skLineSegment(sketch, "E1565", {"start": v(45.23, -132.08) * mm, "end": v(44.63, -132.38) * mm});
            skLineSegment(sketch, "E1566", {"start": v(44.63, -132.38) * mm, "end": v(43.3, -133.02) * mm});
            skLineSegment(sketch, "E1567", {"start": v(43.3, -133.02) * mm, "end": v(41.96, -133.6) * mm});
            skLineSegment(sketch, "E1568", {"start": v(41.96, -133.6) * mm, "end": v(41.33, -133.85) * mm});
            skLineSegment(sketch, "E1569", {"start": v(41.33, -133.85) * mm, "end": v(40.6, -133.21) * mm});
            skLineSegment(sketch, "E1570", {"start": v(40.6, -133.21) * mm, "end": v(39.04, -131.76) * mm});
            skLineSegment(sketch, "E1571", {"start": v(39.04, -131.76) * mm, "end": v(37.6, -130.23) * mm});
            skLineSegment(sketch, "E1572", {"start": v(37.6, -130.23) * mm, "end": v(36.98, -129.52) * mm});
            skLineSegment(sketch, "E1573", {"start": v(36.98, -129.52) * mm, "end": v(36.81, -129.57) * mm});
            skLineSegment(sketch, "E1574", {"start": v(36.81, -129.57) * mm, "end": v(36.38, -129.68) * mm});
            skLineSegment(sketch, "E1575", {"start": v(36.38, -129.68) * mm, "end": v(35.06, -129.97) * mm});
            skLineSegment(sketch, "E1576", {"start": v(35.06, -129.97) * mm, "end": v(33.72, -130.2) * mm});
            skLineSegment(sketch, "E1577", {"start": v(33.72, -130.2) * mm, "end": v(32.98, -130.29) * mm});
            skLineSegment(sketch, "E1578", {"start": v(32.98, -130.29) * mm, "end": v(32.62, -131.2) * mm});
            skLineSegment(sketch, "E1579", {"start": v(32.62, -131.2) * mm, "end": v(31.72, -133.15) * mm});
            skLineSegment(sketch, "E1580", {"start": v(31.72, -133.15) * mm, "end": v(30.7, -135.07) * mm});
            skLineSegment(sketch, "E1581", {"start": v(30.7, -135.07) * mm, "end": v(30.18, -135.94) * mm});
            skLineSegment(sketch, "E1582", {"start": v(30.18, -135.94) * mm, "end": v(29.51, -135.94) * mm});
            skLineSegment(sketch, "E1583", {"start": v(29.51, -135.94) * mm, "end": v(28.04, -135.9) * mm});
            skLineSegment(sketch, "E1584", {"start": v(28.04, -135.9) * mm, "end": v(26.58, -135.78) * mm});
            skLineSegment(sketch, "E1585", {"start": v(26.58, -135.78) * mm, "end": v(25.91, -135.7) * mm});
            skLineSegment(sketch, "E1586", {"start": v(25.91, -135.7) * mm, "end": v(25.55, -134.8) * mm});
            skLineSegment(sketch, "E1587", {"start": v(25.55, -134.8) * mm, "end": v(24.85, -132.78) * mm});
            skLineSegment(sketch, "E1588", {"start": v(24.85, -132.78) * mm, "end": v(24.28, -130.77) * mm});
            skLineSegment(sketch, "E1589", {"start": v(24.28, -130.77) * mm, "end": v(24.06, -129.84) * mm});
            skLineSegment(sketch, "E1590", {"start": v(24.06, -129.84) * mm, "end": v(23.46, -129.7) * mm});
            skLineSegment(sketch, "E1591", {"start": v(23.46, -129.7) * mm, "end": v(22.15, -129.35) * mm});
            skLineSegment(sketch, "E1592", {"start": v(22.15, -129.35) * mm, "end": v(20.86, -128.94) * mm});
            skLineSegment(sketch, "E1593", {"start": v(20.86, -128.94) * mm, "end": v(20.44, -128.79) * mm});
            skLineSegment(sketch, "E1594", {"start": v(20.44, -128.79) * mm, "end": v(20.16, -128.67) * mm});
            skLineSegment(sketch, "E1595", {"start": v(20.16, -128.67) * mm, "end": v(19.43, -129.3) * mm});
            skLineSegment(sketch, "E1596", {"start": v(19.43, -129.3) * mm, "end": v(18.65, -129.93) * mm});
            skLineSegment(sketch, "E1597", {"start": v(18.65, -129.93) * mm, "end": v(17.73, -130.62) * mm});
            skLineSegment(sketch, "E1598", {"start": v(17.73, -130.62) * mm, "end": v(15.06, -132.37) * mm});
            skLineSegment(sketch, "E1599", {"start": v(15.06, -132.37) * mm, "end": v(14.46, -132.07) * mm});
            skLineSegment(sketch, "E1600", {"start": v(14.46, -132.07) * mm, "end": v(13.19, -131.34) * mm});
            skLineSegment(sketch, "E1601", {"start": v(13.19, -131.34) * mm, "end": v(11.94, -130.55) * mm});
            skLineSegment(sketch, "E1602", {"start": v(11.94, -130.55) * mm, "end": v(11.54, -130.28) * mm});
            skLineSegment(sketch, "E1603", {"start": v(11.54, -130.28) * mm, "end": v(11.4, -130.18) * mm});
            skLineSegment(sketch, "E1604", {"start": v(11.4, -130.18) * mm, "end": v(11.5, -129.2) * mm});
            skLineSegment(sketch, "E1605", {"start": v(11.5, -129.2) * mm, "end": v(11.81, -127.1) * mm});
            skLineSegment(sketch, "E1606", {"start": v(11.81, -127.1) * mm, "end": v(12.24, -125.05) * mm});
            skLineSegment(sketch, "E1607", {"start": v(12.24, -125.05) * mm, "end": v(12.48, -124.13) * mm});
            skLineSegment(sketch, "E1608", {"start": v(12.48, -124.13) * mm, "end": v(12.01, -123.73) * mm});
            skLineSegment(sketch, "E1609", {"start": v(12.01, -123.73) * mm, "end": v(11.02, -122.8) * mm});
            skLineSegment(sketch, "E1610", {"start": v(11.02, -122.8) * mm, "end": v(10.07, -121.84) * mm});
            skLineSegment(sketch, "E1611", {"start": v(10.07, -121.84) * mm, "end": v(9.77, -121.5) * mm});
            skLineSegment(sketch, "E1612", {"start": v(9.77, -121.5) * mm, "end": v(9.57, -121.28) * mm});
            skLineSegment(sketch, "E1613", {"start": v(9.57, -121.28) * mm, "end": v(8.63, -121.5) * mm});
            skLineSegment(sketch, "E1614", {"start": v(8.63, -121.5) * mm, "end": v(6.51, -121.87) * mm});
            skLineSegment(sketch, "E1615", {"start": v(6.51, -121.87) * mm, "end": v(4.34, -122.12) * mm});
            skLineSegment(sketch, "E1616", {"start": v(4.34, -122.12) * mm, "end": v(3.34, -122.19) * mm});
            skLineSegment(sketch, "E1617", {"start": v(3.34, -122.19) * mm, "end": v(2.95, -121.64) * mm});
            skLineSegment(sketch, "E1618", {"start": v(2.95, -121.64) * mm, "end": v(2.16, -120.4) * mm});
            skLineSegment(sketch, "E1619", {"start": v(2.16, -120.4) * mm, "end": v(1.42, -119.13) * mm});
            skLineSegment(sketch, "E1620", {"start": v(1.42, -119.13) * mm, "end": v(1.19, -118.7) * mm});
            skLineSegment(sketch, "E1621", {"start": v(1.19, -118.7) * mm, "end": v(1.1, -118.54) * mm});
            skLineSegment(sketch, "E1622", {"start": v(1.1, -118.54) * mm, "end": v(1.65, -117.73) * mm});
            skLineSegment(sketch, "E1623", {"start": v(1.65, -117.73) * mm, "end": v(2.9, -116.01) * mm});
            skLineSegment(sketch, "E1624", {"start": v(2.9, -116.01) * mm, "end": v(4.23, -114.4) * mm});
            skLineSegment(sketch, "E1625", {"start": v(4.23, -114.4) * mm, "end": v(4.87, -113.7) * mm});
            skLineSegment(sketch, "E1626", {"start": v(4.87, -113.7) * mm, "end": v(4.64, -113.12) * mm});
            skLineSegment(sketch, "E1627", {"start": v(4.64, -113.12) * mm, "end": v(4.2, -111.84) * mm});
            skLineSegment(sketch, "E1628", {"start": v(4.2, -111.84) * mm, "end": v(3.8, -110.55) * mm});
            skLineSegment(sketch, "E1629", {"start": v(3.8, -110.55) * mm, "end": v(3.65, -109.95) * mm});
            skLineSegment(sketch, "E1630", {"start": v(3.65, -109.95) * mm, "end": v(3.62, -109.82) * mm});
            skLineSegment(sketch, "E1631", {"start": v(3.62, -109.82) * mm, "end": v(2.69, -109.57) * mm});
            skLineSegment(sketch, "E1632", {"start": v(2.69, -109.57) * mm, "end": v(1.72, -109.29) * mm});
            skLineSegment(sketch, "E1633", {"start": v(1.72, -109.29) * mm, "end": v(0.64, -108.92) * mm});
            skLineSegment(sketch, "E1634", {"start": v(0.64, -108.92) * mm, "end": v(-1.4, -108.12) * mm});
            skLineSegment(sketch, "E1635", {"start": v(-1.4, -108.12) * mm, "end": v(-2.32, -107.72) * mm});
            skLineSegment(sketch, "E1636", {"start": v(-2.32, -107.72) * mm, "end": v(-2.4, -107.05) * mm});
            skLineSegment(sketch, "E1637", {"start": v(-2.4, -107.05) * mm, "end": v(-2.53, -105.59) * mm});
            skLineSegment(sketch, "E1638", {"start": v(-2.53, -105.59) * mm, "end": v(-2.58, -104.12) * mm});
            skLineSegment(sketch, "E1639", {"start": v(-2.58, -104.12) * mm, "end": v(-2.6, -103.46) * mm});
            skLineSegment(sketch, "E1640", {"start": v(-2.6, -103.46) * mm, "end": v(0.17, -102.05) * mm});
            skLineSegment(sketch, "E1641", {"start": v(0.17, -102.05) * mm, "end": v(3, -100.9) * mm});
            skLineSegment(sketch, "E1642", {"start": v(3, -100.9) * mm, "end": v(3, -100.74) * mm});
            skLineSegment(sketch, "E1643", {"start": v(3, -100.74) * mm, "end": v(3.26, -98.96) * mm});
            skLineSegment(sketch, "E1644", {"start": v(3.26, -98.96) * mm, "end": v(3.51, -97.63) * mm});
            skLineSegment(sketch, "E1645", {"start": v(3.51, -97.63) * mm, "end": v(3.68, -96.9) * mm});
            skLineSegment(sketch, "E1646", {"start": v(3.68, -96.9) * mm, "end": v(2.97, -96.24) * mm});
            skLineSegment(sketch, "E1647", {"start": v(2.97, -96.24) * mm, "end": v(1.45, -94.72) * mm});
            skLineSegment(sketch, "E1648", {"start": v(1.45, -94.72) * mm, "end": v(0.02, -93.07) * mm});
            skLineSegment(sketch, "E1649", {"start": v(0.02, -93.07) * mm, "end": v(-0.6, -92.28) * mm});
            skLineSegment(sketch, "E1650", {"start": v(-0.6, -92.28) * mm, "end": v(-0.37, -91.66) * mm});
            skLineSegment(sketch, "E1651", {"start": v(-0.37, -91.66) * mm, "end": v(0.2, -90.3) * mm});
            skLineSegment(sketch, "E1652", {"start": v(0.2, -90.3) * mm, "end": v(0.83, -88.97) * mm});
            skLineSegment(sketch, "E1653", {"start": v(0.83, -88.97) * mm, "end": v(1.13, -88.37) * mm});
            skLineSegment(sketch, "E1654", {"start": v(1.13, -88.37) * mm, "end": v(2.1, -88.36) * mm});
            skLineSegment(sketch, "E1655", {"start": v(2.1, -88.36) * mm, "end": v(4.24, -88.42) * mm});
            skLineSegment(sketch, "E1656", {"start": v(4.24, -88.42) * mm, "end": v(6.33, -88.6) * mm});
            skLineSegment(sketch, "E1657", {"start": v(6.33, -88.6) * mm, "end": v(7.27, -88.73) * mm});
            skLineSegment(sketch, "E1658", {"start": v(7.27, -88.73) * mm, "end": v(7.36, -88.59) * mm});
            skLineSegment(sketch, "E1659", {"start": v(7.36, -88.59) * mm, "end": v(7.6, -88.22) * mm});
            skLineSegment(sketch, "E1660", {"start": v(7.6, -88.22) * mm, "end": v(8.4, -87.12) * mm});
            skLineSegment(sketch, "E1661", {"start": v(8.4, -87.12) * mm, "end": v(9.26, -86.06) * mm});
            skLineSegment(sketch, "E1662", {"start": v(9.26, -86.06) * mm, "end": v(9.75, -85.5) * mm});
            skLineSegment(sketch, "E1663", {"start": v(9.75, -85.5) * mm, "end": v(9.42, -84.59) * mm});
            skLineSegment(sketch, "E1664", {"start": v(9.42, -84.59) * mm, "end": v(8.79, -82.53) * mm});
            skLineSegment(sketch, "E1665", {"start": v(8.79, -82.53) * mm, "end": v(8.29, -80.4) * mm});
            skLineSegment(sketch, "E1666", {"start": v(8.29, -80.4) * mm, "end": v(8.1, -79.41) * mm});
            skLineSegment(sketch, "E1667", {"start": v(8.1, -79.41) * mm, "end": v(8.6, -78.97) * mm});
            skLineSegment(sketch, "E1668", {"start": v(8.6, -78.97) * mm, "end": v(9.73, -78.04) * mm});
            skLineSegment(sketch, "E1669", {"start": v(9.73, -78.04) * mm, "end": v(10.9, -77.15) * mm});
            skLineSegment(sketch, "E1670", {"start": v(10.9, -77.15) * mm, "end": v(11.45, -76.76) * mm});
            skLineSegment(sketch, "E1671", {"start": v(11.45, -76.76) * mm, "end": v(12.32, -77.2) * mm});
            skLineSegment(sketch, "E1672", {"start": v(12.32, -77.2) * mm, "end": v(14.17, -78.24) * mm});
            skLineSegment(sketch, "E1673", {"start": v(14.17, -78.24) * mm, "end": v(15.94, -79.38) * mm});
            skLineSegment(sketch, "E1674", {"start": v(15.94, -79.38) * mm, "end": v(16.72, -79.92) * mm});
            skLineSegment(sketch, "E1675", {"start": v(16.72, -79.92) * mm, "end": v(16.86, -79.83) * mm});
            skLineSegment(sketch, "E1676", {"start": v(16.86, -79.83) * mm, "end": v(17.26, -79.62) * mm});
            skLineSegment(sketch, "E1677", {"start": v(17.26, -79.62) * mm, "end": v(18.47, -79.02) * mm});
            skLineSegment(sketch, "E1678", {"start": v(18.47, -79.02) * mm, "end": v(19.71, -78.48) * mm});
            skLineSegment(sketch, "E1679", {"start": v(19.71, -78.48) * mm, "end": v(20.4, -78.2) * mm});
            skLineSegment(sketch, "E1680", {"start": v(20.4, -78.2) * mm, "end": v(20.54, -77.25) * mm});
            skLineSegment(sketch, "E1681", {"start": v(20.54, -77.25) * mm, "end": v(20.94, -75.13) * mm});
            skLineSegment(sketch, "E1682", {"start": v(20.94, -75.13) * mm, "end": v(21.78, -72.05) * mm});
            skLineSegment(sketch, "E1683", {"start": v(21.78, -72.05) * mm, "end": v(22.43, -71.9) * mm});
            skLineSegment(sketch, "E1684", {"start": v(22.43, -71.9) * mm, "end": v(23.87, -71.6) * mm});
            skLineSegment(sketch, "E1685", {"start": v(23.87, -71.6) * mm, "end": v(25.32, -71.35) * mm});
            skLineSegment(sketch, "E1686", {"start": v(25.32, -71.35) * mm, "end": v(25.98, -71.27) * mm});
            skLineSegment(sketch, "E1687", {"start": v(25.98, -71.27) * mm, "end": v(26.54, -72.06) * mm});
            skLineSegment(sketch, "E1688", {"start": v(26.54, -72.06) * mm, "end": v(27.7, -73.85) * mm});
            skLineSegment(sketch, "E1689", {"start": v(27.7, -73.85) * mm, "end": v(28.74, -75.68) * mm});
            skLineSegment(sketch, "E1690", {"start": v(28.74, -75.68) * mm, "end": v(29.17, -76.52) * mm});
            skLineSegment(sketch, "E1691", {"start": v(29.17, -76.52) * mm, "end": v(29.8, -76.5) * mm});
            skLineSegment(sketch, "E1692", {"start": v(29.8, -76.5) * mm, "end": v(31.15, -76.53) * mm});
            skLineSegment(sketch, "E1693", {"start": v(31.15, -76.53) * mm, "end": v(32.5, -76.63) * mm});
            skLineSegment(sketch, "E1694", {"start": v(32.5, -76.63) * mm, "end": v(33.24, -76.72) * mm});
            skLineSegment(sketch, "E1695", {"start": v(33.24, -76.72) * mm, "end": v(33.8, -75.93) * mm});
            skLineSegment(sketch, "E1696", {"start": v(33.8, -75.93) * mm, "end": v(35.14, -74.24) * mm});
            skLineSegment(sketch, "E1697", {"start": v(35.14, -74.24) * mm, "end": v(36.6, -72.62) * mm});
            skLineSegment(sketch, "E1698", {"start": v(36.6, -72.62) * mm, "end": v(37.3, -71.9) * mm});
            skLineSegment(sketch, "E1699", {"start": v(37.3, -71.9) * mm, "end": v(37.96, -72.05) * mm});
            skLineSegment(sketch, "E1700", {"start": v(37.96, -72.05) * mm, "end": v(39.37, -72.45) * mm});
            skLineSegment(sketch, "E1701", {"start": v(39.37, -72.45) * mm, "end": v(40.77, -72.92) * mm});
            skLineSegment(sketch, "E1702", {"start": v(40.77, -72.92) * mm, "end": v(41.23, -73.09) * mm});
            skLineSegment(sketch, "E1703", {"start": v(41.23, -73.09) * mm, "end": v(41.4, -73.15) * mm});
            skLineSegment(sketch, "E1704", {"start": v(41.4, -73.15) * mm, "end": v(41.53, -74.12) * mm});
            skLineSegment(sketch, "E1705", {"start": v(41.53, -74.12) * mm, "end": v(41.72, -76.24) * mm});
            skLineSegment(sketch, "E1706", {"start": v(41.72, -76.24) * mm, "end": v(41.8, -78.33) * mm});
            skLineSegment(sketch, "E1707", {"start": v(41.8, -78.33) * mm, "end": v(41.79, -79.28) * mm});
            skLineSegment(sketch, "E1708", {"start": v(41.79, -79.28) * mm, "end": v(42.34, -79.56) * mm});
            skLineSegment(sketch, "E1709", {"start": v(42.34, -79.56) * mm, "end": v(43.52, -80.22) * mm});
            skLineSegment(sketch, "E1710", {"start": v(43.52, -80.22) * mm, "end": v(44.67, -80.93) * mm});
            skLineSegment(sketch, "E1711", {"start": v(44.67, -80.93) * mm, "end": v(45.18, -81.28) * mm});
            skLineSegment(sketch, "E1712", {"start": v(45.18, -81.28) * mm, "end": v(45.3, -81.36) * mm});
            skLineSegment(sketch, "E1713", {"start": v(45.3, -81.36) * mm, "end": v(46.16, -80.92) * mm});
            skLineSegment(sketch, "E1714", {"start": v(46.16, -80.92) * mm, "end": v(47.07, -80.5) * mm});
            skLineSegment(sketch, "E1715", {"start": v(47.07, -80.5) * mm, "end": v(48.12, -80.05) * mm});
            skLineSegment(sketch, "E1716", {"start": v(48.12, -80.05) * mm, "end": v(51.13, -78.99) * mm});
            skLineSegment(sketch, "E1717", {"start": v(51.13, -78.99) * mm, "end": v(51.64, -79.43) * mm});
            skLineSegment(sketch, "E1718", {"start": v(51.64, -79.43) * mm, "end": v(52.7, -80.44) * mm});
            skLineSegment(sketch, "E1719", {"start": v(52.7, -80.44) * mm, "end": v(53.72, -81.5) * mm});
            skLineSegment(sketch, "E1720", {"start": v(53.72, -81.5) * mm, "end": v(54.05, -81.86) * mm});
            skLineSegment(sketch, "E1721", {"start": v(54.05, -81.86) * mm, "end": v(54.17, -82) * mm});
            skLineSegment(sketch, "E1722", {"start": v(54.17, -82) * mm, "end": v(53.83, -82.91) * mm});
            skLineSegment(sketch, "E1723", {"start": v(53.83, -82.91) * mm, "end": v(53.02, -84.88) * mm});
            skLineSegment(sketch, "E1724", {"start": v(53.02, -84.88) * mm, "end": v(52.12, -86.77) * mm});
            skLineSegment(sketch, "E1725", {"start": v(52.12, -86.77) * mm, "end": v(51.67, -87.6) * mm});
            skLineSegment(sketch, "E1726", {"start": v(51.67, -87.6) * mm, "end": v(52.03, -88.1) * mm});
            skLineSegment(sketch, "E1727", {"start": v(52.03, -88.1) * mm, "end": v(52.77, -89.24) * mm});
            skLineSegment(sketch, "E1728", {"start": v(52.77, -89.24) * mm, "end": v(53.46, -90.4) * mm});
            skLineSegment(sketch, "E1729", {"start": v(53.46, -90.4) * mm, "end": v(53.68, -90.8) * mm});
            skLineSegment(sketch, "E1730", {"start": v(53.68, -90.8) * mm, "end": v(53.81, -91.07) * mm});
            skLineSegment(sketch, "E1731", {"start": v(53.81, -91.07) * mm, "end": v(54.78, -91.08) * mm});
            skLineSegment(sketch, "E1732", {"start": v(54.78, -91.08) * mm, "end": v(56.93, -91.22) * mm});
            skLineSegment(sketch, "E1733", {"start": v(56.93, -91.22) * mm, "end": v(59.1, -91.5) * mm});
            skLineSegment(sketch, "E1734", {"start": v(59.1, -91.5) * mm, "end": v(60.09, -91.68) * mm});
            skLineSegment(sketch, "E1735", {"start": v(60.09, -91.68) * mm, "end": v(60.33, -92.3) * mm});
            skLineSegment(sketch, "E1736", {"start": v(60.33, -92.3) * mm, "end": v(60.8, -93.7) * mm});
            skLineSegment(sketch, "E1737", {"start": v(60.8, -93.7) * mm, "end": v(61.21, -95.1) * mm});
            skLineSegment(sketch, "E1738", {"start": v(61.21, -95.1) * mm, "end": v(61.34, -95.58) * mm});
            skLineSegment(sketch, "E1739", {"start": v(61.34, -95.58) * mm, "end": v(61.38, -95.76) * mm});
            skLineSegment(sketch, "E1740", {"start": v(61.38, -95.76) * mm, "end": v(60.65, -96.41) * mm});
            skLineSegment(sketch, "E1741", {"start": v(60.65, -96.41) * mm, "end": v(59.02, -97.78) * mm});
            skLineSegment(sketch, "E1742", {"start": v(59.02, -97.78) * mm, "end": v(57.34, -99.03) * mm});
            skLineSegment(sketch, "E1743", {"start": v(57.34, -99.03) * mm, "end": v(56.55, -99.56) * mm});
            skLineSegment(sketch, "E1744", {"start": v(56.55, -99.56) * mm, "end": v(56.7, -100.8) * mm});
            skLineSegment(sketch, "E1745", {"start": v(56.7, -100.8) * mm, "end": v(56.76, -101.52) * mm});
            skLineSegment(sketch, "E1746", {"start": v(56.76, -101.52) * mm, "end": v(56.83, -102.87) * mm});
            skLineSegment(sketch, "E1747", {"start": v(56.83, -102.87) * mm, "end": v(56.84, -103.49) * mm});
            skLineSegment(sketch, "E1748", {"start": v(56.84, -103.49) * mm, "end": v(56.84, -103.62) * mm});
            skLineSegment(sketch, "E1749", {"start": v(29.76, -102.57) * mm, "end": v(29.03, -102.88) * mm});
            skLineSegment(sketch, "E1750", {"start": v(29.03, -102.88) * mm, "end": v(28.73, -103.6) * mm});
            skLineSegment(sketch, "E1751", {"start": v(28.73, -103.6) * mm, "end": v(29.03, -104.33) * mm});
            skLineSegment(sketch, "E1752", {"start": v(29.03, -104.33) * mm, "end": v(29.76, -104.63) * mm});
            skLineSegment(sketch, "E1753", {"start": v(29.76, -104.63) * mm, "end": v(30.48, -104.33) * mm});
            skLineSegment(sketch, "E1754", {"start": v(30.48, -104.33) * mm, "end": v(30.78, -103.6) * mm});
            skLineSegment(sketch, "E1755", {"start": v(30.78, -103.6) * mm, "end": v(30.48, -102.88) * mm});
            skLineSegment(sketch, "E1756", {"start": v(30.48, -102.88) * mm, "end": v(29.76, -102.57) * mm});
            skLineSegment(sketch, "E1757", {"start": v(43.65, -41.27) * mm, "end": v(42.7, -41.1) * mm});
            skLineSegment(sketch, "E1758", {"start": v(42.7, -41.1) * mm, "end": v(40.58, -40.59) * mm});
            skLineSegment(sketch, "E1759", {"start": v(40.58, -40.59) * mm, "end": v(38.47, -39.86) * mm});
            skLineSegment(sketch, "E1760", {"start": v(38.47, -39.86) * mm, "end": v(37.77, -39.58) * mm});
            skLineSegment(sketch, "E1761", {"start": v(37.77, -39.58) * mm, "end": v(37.52, -39.46) * mm});
            skLineSegment(sketch, "E1762", {"start": v(37.52, -39.46) * mm, "end": v(37.39, -38.74) * mm});
            skLineSegment(sketch, "E1763", {"start": v(37.39, -38.74) * mm, "end": v(37.19, -37.15) * mm});
            skLineSegment(sketch, "E1764", {"start": v(37.19, -37.15) * mm, "end": v(37.1, -35.54) * mm});
            skLineSegment(sketch, "E1765", {"start": v(37.1, -35.54) * mm, "end": v(37.08, -34.81) * mm});
            skLineSegment(sketch, "E1766", {"start": v(37.08, -34.81) * mm, "end": v(37.94, -34.3) * mm});
            skLineSegment(sketch, "E1767", {"start": v(37.94, -34.3) * mm, "end": v(39.87, -33.32) * mm});
            skLineSegment(sketch, "E1768", {"start": v(39.87, -33.32) * mm, "end": v(41.83, -32.52) * mm});
            skLineSegment(sketch, "E1769", {"start": v(41.83, -32.52) * mm, "end": v(42.73, -32.21) * mm});
            skLineSegment(sketch, "E1770", {"start": v(42.73, -32.21) * mm, "end": v(42.83, -31.59) * mm});
            skLineSegment(sketch, "E1771", {"start": v(42.83, -31.59) * mm, "end": v(42.94, -30.95) * mm});
            skLineSegment(sketch, "E1772", {"start": v(42.94, -30.95) * mm, "end": v(43.1, -30.23) * mm});
            skLineSegment(sketch, "E1773", {"start": v(43.1, -30.23) * mm, "end": v(43.3, -29.52) * mm});
            skLineSegment(sketch, "E1774", {"start": v(43.3, -29.52) * mm, "end": v(43.5, -28.9) * mm});
            skLineSegment(sketch, "E1775", {"start": v(43.5, -28.9) * mm, "end": v(43.7, -28.3) * mm});
            skLineSegment(sketch, "E1776", {"start": v(43.7, -28.3) * mm, "end": v(43.74, -28.17) * mm});
            skLineSegment(sketch, "E1777", {"start": v(43.74, -28.17) * mm, "end": v(43.12, -27.43) * mm});
            skLineSegment(sketch, "E1778", {"start": v(43.12, -27.43) * mm, "end": v(41.83, -25.68) * mm});
            skLineSegment(sketch, "E1779", {"start": v(41.83, -25.68) * mm, "end": v(40.68, -23.77) * mm});
            skLineSegment(sketch, "E1780", {"start": v(40.68, -23.77) * mm, "end": v(40.2, -22.85) * mm});
            skLineSegment(sketch, "E1781", {"start": v(40.2, -22.85) * mm, "end": v(40.57, -22.22) * mm});
            skLineSegment(sketch, "E1782", {"start": v(40.57, -22.22) * mm, "end": v(41.44, -20.86) * mm});
            skLineSegment(sketch, "E1783", {"start": v(41.44, -20.86) * mm, "end": v(41.94, -20.16) * mm});
            skLineSegment(sketch, "E1784", {"start": v(41.94, -20.16) * mm, "end": v(42.4, -19.57) * mm});
            skLineSegment(sketch, "E1785", {"start": v(42.4, -19.57) * mm, "end": v(42.86, -19) * mm});
            skLineSegment(sketch, "E1786", {"start": v(42.86, -19) * mm, "end": v(43.85, -19.17) * mm});
            skLineSegment(sketch, "E1787", {"start": v(43.85, -19.17) * mm, "end": v(45.95, -19.66) * mm});
            skLineSegment(sketch, "E1788", {"start": v(45.95, -19.66) * mm, "end": v(47.97, -20.3) * mm});
            skLineSegment(sketch, "E1789", {"start": v(47.97, -20.3) * mm, "end": v(48.86, -20.65) * mm});
            skLineSegment(sketch, "E1790", {"start": v(48.86, -20.65) * mm, "end": v(49.33, -20.23) * mm});
            skLineSegment(sketch, "E1791", {"start": v(49.33, -20.23) * mm, "end": v(49.84, -19.82) * mm});
            skLineSegment(sketch, "E1792", {"start": v(49.84, -19.82) * mm, "end": v(50.43, -19.37) * mm});
            skLineSegment(sketch, "E1793", {"start": v(50.43, -19.37) * mm, "end": v(52.12, -18.27) * mm});
            skLineSegment(sketch, "E1794", {"start": v(52.12, -18.27) * mm, "end": v(52.24, -18.2) * mm});
            skLineSegment(sketch, "E1795", {"start": v(52.24, -18.2) * mm, "end": v(52.23, -17.23) * mm});
            skLineSegment(sketch, "E1796", {"start": v(52.23, -17.23) * mm, "end": v(52.37, -15.06) * mm});
            skLineSegment(sketch, "E1797", {"start": v(52.37, -15.06) * mm, "end": v(52.94, -11.85) * mm});
            skLineSegment(sketch, "E1798", {"start": v(52.94, -11.85) * mm, "end": v(53.62, -11.6) * mm});
            skLineSegment(sketch, "E1799", {"start": v(53.62, -11.6) * mm, "end": v(54.34, -11.36) * mm});
            skLineSegment(sketch, "E1800", {"start": v(54.34, -11.36) * mm, "end": v(55.16, -11.12) * mm});
            skLineSegment(sketch, "E1801", {"start": v(55.16, -11.12) * mm, "end": v(56.73, -10.74) * mm});
            skLineSegment(sketch, "E1802", {"start": v(56.73, -10.74) * mm, "end": v(57.45, -10.61) * mm});
            skLineSegment(sketch, "E1803", {"start": v(57.45, -10.61) * mm, "end": v(58.1, -11.37) * mm});
            skLineSegment(sketch, "E1804", {"start": v(58.1, -11.37) * mm, "end": v(59.4, -13.1) * mm});
            skLineSegment(sketch, "E1805", {"start": v(59.4, -13.1) * mm, "end": v(60.53, -14.9) * mm});
            skLineSegment(sketch, "E1806", {"start": v(60.53, -14.9) * mm, "end": v(60.86, -15.5) * mm});
            skLineSegment(sketch, "E1807", {"start": v(60.86, -15.5) * mm, "end": v(60.98, -15.73) * mm});
            skLineSegment(sketch, "E1808", {"start": v(60.98, -15.73) * mm, "end": v(61.62, -15.71) * mm});
            skLineSegment(sketch, "E1809", {"start": v(61.62, -15.71) * mm, "end": v(62.26, -15.73) * mm});
            skLineSegment(sketch, "E1810", {"start": v(62.26, -15.73) * mm, "end": v(63, -15.76) * mm});
            skLineSegment(sketch, "E1811", {"start": v(63, -15.76) * mm, "end": v(65, -16) * mm});
            skLineSegment(sketch, "E1812", {"start": v(65, -16) * mm, "end": v(65.14, -16.03) * mm});
            skLineSegment(sketch, "E1813", {"start": v(65.14, -16.03) * mm, "end": v(65.77, -15.27) * mm});
            skLineSegment(sketch, "E1814", {"start": v(65.77, -15.27) * mm, "end": v(67.27, -13.7) * mm});
            skLineSegment(sketch, "E1815", {"start": v(67.27, -13.7) * mm, "end": v(68.95, -12.23) * mm});
            skLineSegment(sketch, "E1816", {"start": v(68.95, -12.23) * mm, "end": v(69.77, -11.6) * mm});
            skLineSegment(sketch, "E1817", {"start": v(69.77, -11.6) * mm, "end": v(71.94, -12.48) * mm});
            skLineSegment(sketch, "E1818", {"start": v(71.94, -12.48) * mm, "end": v(73.38, -13.2) * mm});
            skLineSegment(sketch, "E1819", {"start": v(73.38, -13.2) * mm, "end": v(74.02, -13.56) * mm});
            skLineSegment(sketch, "E1820", {"start": v(74.02, -13.56) * mm, "end": v(74.03, -14.55) * mm});
            skLineSegment(sketch, "E1821", {"start": v(74.03, -14.55) * mm, "end": v(73.91, -16.71) * mm});
            skLineSegment(sketch, "E1822", {"start": v(73.91, -16.71) * mm, "end": v(73.63, -18.81) * mm});
            skLineSegment(sketch, "E1823", {"start": v(73.63, -18.81) * mm, "end": v(73.44, -19.75) * mm});
            skLineSegment(sketch, "E1824", {"start": v(73.44, -19.75) * mm, "end": v(73.93, -20.14) * mm});
            skLineSegment(sketch, "E1825", {"start": v(73.93, -20.14) * mm, "end": v(74.96, -21.07) * mm});
            skLineSegment(sketch, "E1826", {"start": v(74.96, -21.07) * mm, "end": v(75.49, -21.6) * mm});
            skLineSegment(sketch, "E1827", {"start": v(75.49, -21.6) * mm, "end": v(75.93, -22.07) * mm});
            skLineSegment(sketch, "E1828", {"start": v(75.93, -22.07) * mm, "end": v(76.43, -22.65) * mm});
            skLineSegment(sketch, "E1829", {"start": v(76.43, -22.65) * mm, "end": v(77.39, -22.48) * mm});
            skLineSegment(sketch, "E1830", {"start": v(77.39, -22.48) * mm, "end": v(78.4, -22.34) * mm});
            skLineSegment(sketch, "E1831", {"start": v(78.4, -22.34) * mm, "end": v(79.55, -22.24) * mm});
            skLineSegment(sketch, "E1832", {"start": v(79.55, -22.24) * mm, "end": v(81.78, -22.2) * mm});
            skLineSegment(sketch, "E1833", {"start": v(81.78, -22.2) * mm, "end": v(82.53, -22.22) * mm});
            skLineSegment(sketch, "E1834", {"start": v(82.53, -22.22) * mm, "end": v(82.81, -22.24) * mm});
            skLineSegment(sketch, "E1835", {"start": v(82.81, -22.24) * mm, "end": v(83.92, -24.3) * mm});
            skLineSegment(sketch, "E1836", {"start": v(83.92, -24.3) * mm, "end": v(84.56, -25.78) * mm});
            skLineSegment(sketch, "E1837", {"start": v(84.56, -25.78) * mm, "end": v(84.82, -26.46) * mm});
            skLineSegment(sketch, "E1838", {"start": v(84.82, -26.46) * mm, "end": v(84.18, -27.24) * mm});
            skLineSegment(sketch, "E1839", {"start": v(84.18, -27.24) * mm, "end": v(82.7, -28.82) * mm});
            skLineSegment(sketch, "E1840", {"start": v(82.7, -28.82) * mm, "end": v(81.14, -30.24) * mm});
            skLineSegment(sketch, "E1841", {"start": v(81.14, -30.24) * mm, "end": v(80.4, -30.84) * mm});
            skLineSegment(sketch, "E1842", {"start": v(80.4, -30.84) * mm, "end": v(80.44, -31) * mm});
            skLineSegment(sketch, "E1843", {"start": v(80.44, -31) * mm, "end": v(80.52, -31.46) * mm});
            skLineSegment(sketch, "E1844", {"start": v(80.52, -31.46) * mm, "end": v(80.71, -32.83) * mm});
            skLineSegment(sketch, "E1845", {"start": v(80.71, -32.83) * mm, "end": v(80.8, -34.22) * mm});
            skLineSegment(sketch, "E1846", {"start": v(80.8, -34.22) * mm, "end": v(80.82, -34.85) * mm});
            skLineSegment(sketch, "E1847", {"start": v(80.82, -34.85) * mm, "end": v(80.82, -34.98) * mm});
            skLineSegment(sketch, "E1848", {"start": v(80.82, -34.98) * mm, "end": v(81.66, -35.47) * mm});
            skLineSegment(sketch, "E1849", {"start": v(81.66, -35.47) * mm, "end": v(83.47, -36.68) * mm});
            skLineSegment(sketch, "E1850", {"start": v(83.47, -36.68) * mm, "end": v(85.21, -38.07) * mm});
            skLineSegment(sketch, "E1851", {"start": v(85.21, -38.07) * mm, "end": v(85.97, -38.77) * mm});
            skLineSegment(sketch, "E1852", {"start": v(85.97, -38.77) * mm, "end": v(85.5, -41.06) * mm});
            skLineSegment(sketch, "E1853", {"start": v(85.5, -41.06) * mm, "end": v(85.03, -42.6) * mm});
            skLineSegment(sketch, "E1854", {"start": v(85.03, -42.6) * mm, "end": v(84.8, -43.3) * mm});
            skLineSegment(sketch, "E1855", {"start": v(84.8, -43.3) * mm, "end": v(83.81, -43.48) * mm});
            skLineSegment(sketch, "E1856", {"start": v(83.81, -43.48) * mm, "end": v(81.66, -43.74) * mm});
            skLineSegment(sketch, "E1857", {"start": v(81.66, -43.74) * mm, "end": v(79.55, -43.82) * mm});
            skLineSegment(sketch, "E1858", {"start": v(79.55, -43.82) * mm, "end": v(78.6, -43.8) * mm});
            skLineSegment(sketch, "E1859", {"start": v(78.6, -43.8) * mm, "end": v(78.52, -43.96) * mm});
            skLineSegment(sketch, "E1860", {"start": v(78.52, -43.96) * mm, "end": v(78.3, -44.35) * mm});
            skLineSegment(sketch, "E1861", {"start": v(78.3, -44.35) * mm, "end": v(77.56, -45.54) * mm});
            skLineSegment(sketch, "E1862", {"start": v(77.56, -45.54) * mm, "end": v(76.74, -46.65) * mm});
            skLineSegment(sketch, "E1863", {"start": v(76.74, -46.65) * mm, "end": v(76.46, -47.02) * mm});
            skLineSegment(sketch, "E1864", {"start": v(76.46, -47.02) * mm, "end": v(76.25, -47.25) * mm});
            skLineSegment(sketch, "E1865", {"start": v(76.25, -47.25) * mm, "end": v(76.6, -48.16) * mm});
            skLineSegment(sketch, "E1866", {"start": v(76.6, -48.16) * mm, "end": v(77.2, -50.26) * mm});
            skLineSegment(sketch, "E1867", {"start": v(77.2, -50.26) * mm, "end": v(77.64, -52.45) * mm});
            skLineSegment(sketch, "E1868", {"start": v(77.64, -52.45) * mm, "end": v(77.77, -53.46) * mm});
            skLineSegment(sketch, "E1869", {"start": v(77.77, -53.46) * mm, "end": v(77.2, -53.94) * mm});
            skLineSegment(sketch, "E1870", {"start": v(77.2, -53.94) * mm, "end": v(75.92, -54.9) * mm});
            skLineSegment(sketch, "E1871", {"start": v(75.92, -54.9) * mm, "end": v(74.59, -55.8) * mm});
            skLineSegment(sketch, "E1872", {"start": v(74.59, -55.8) * mm, "end": v(73.96, -56.17) * mm});
            skLineSegment(sketch, "E1873", {"start": v(73.96, -56.17) * mm, "end": v(73.09, -55.68) * mm});
            skLineSegment(sketch, "E1874", {"start": v(73.09, -55.68) * mm, "end": v(71.27, -54.5) * mm});
            skLineSegment(sketch, "E1875", {"start": v(71.27, -54.5) * mm, "end": v(69.6, -53.21) * mm});
            skLineSegment(sketch, "E1876", {"start": v(69.6, -53.21) * mm, "end": v(69.07, -52.76) * mm});
            skLineSegment(sketch, "E1877", {"start": v(69.07, -52.76) * mm, "end": v(68.88, -52.58) * mm});
            skLineSegment(sketch, "E1878", {"start": v(68.88, -52.58) * mm, "end": v(68.3, -52.81) * mm});
            skLineSegment(sketch, "E1879", {"start": v(68.3, -52.81) * mm, "end": v(66.97, -53.24) * mm});
            skLineSegment(sketch, "E1880", {"start": v(66.97, -53.24) * mm, "end": v(65.63, -53.58) * mm});
            skLineSegment(sketch, "E1881", {"start": v(65.63, -53.58) * mm, "end": v(64.88, -53.72) * mm});
            skLineSegment(sketch, "E1882", {"start": v(64.88, -53.72) * mm, "end": v(64.79, -53.97) * mm});
            skLineSegment(sketch, "E1883", {"start": v(64.79, -53.97) * mm, "end": v(64.54, -54.63) * mm});
            skLineSegment(sketch, "E1884", {"start": v(64.54, -54.63) * mm, "end": v(63.67, -56.63) * mm});
            skLineSegment(sketch, "E1885", {"start": v(63.67, -56.63) * mm, "end": v(62.04, -59.45) * mm});
            skLineSegment(sketch, "E1886", {"start": v(62.04, -59.45) * mm, "end": v(61.3, -59.45) * mm});
            skLineSegment(sketch, "E1887", {"start": v(61.3, -59.45) * mm, "end": v(59.7, -59.37) * mm});
            skLineSegment(sketch, "E1888", {"start": v(59.7, -59.37) * mm, "end": v(58.1, -59.2) * mm});
            skLineSegment(sketch, "E1889", {"start": v(58.1, -59.2) * mm, "end": v(57.38, -59.07) * mm});
            skLineSegment(sketch, "E1890", {"start": v(57.38, -59.07) * mm, "end": v(57.03, -58.14) * mm});
            skLineSegment(sketch, "E1891", {"start": v(57.03, -58.14) * mm, "end": v(56.4, -56.07) * mm});
            skLineSegment(sketch, "E1892", {"start": v(56.4, -56.07) * mm, "end": v(55.94, -54) * mm});
            skLineSegment(sketch, "E1893", {"start": v(55.94, -54) * mm, "end": v(55.8, -53.06) * mm});
            skLineSegment(sketch, "E1894", {"start": v(55.8, -53.06) * mm, "end": v(55.2, -52.86) * mm});
            skLineSegment(sketch, "E1895", {"start": v(55.2, -52.86) * mm, "end": v(54.6, -52.63) * mm});
            skLineSegment(sketch, "E1896", {"start": v(54.6, -52.63) * mm, "end": v(53.91, -52.34) * mm});
            skLineSegment(sketch, "E1897", {"start": v(53.91, -52.34) * mm, "end": v(52.12, -51.42) * mm});
            skLineSegment(sketch, "E1898", {"start": v(52.12, -51.42) * mm, "end": v(52, -51.35) * mm});
            skLineSegment(sketch, "E1899", {"start": v(52, -51.35) * mm, "end": v(51.77, -51.5) * mm});
            skLineSegment(sketch, "E1900", {"start": v(51.77, -51.5) * mm, "end": v(51.16, -51.84) * mm});
            skLineSegment(sketch, "E1901", {"start": v(51.16, -51.84) * mm, "end": v(49.2, -52.8) * mm});
            skLineSegment(sketch, "E1902", {"start": v(49.2, -52.8) * mm, "end": v(47.13, -53.6) * mm});
            skLineSegment(sketch, "E1903", {"start": v(47.13, -53.6) * mm, "end": v(46.14, -53.92) * mm});
            skLineSegment(sketch, "E1904", {"start": v(46.14, -53.92) * mm, "end": v(45.98, -53.8) * mm});
            skLineSegment(sketch, "E1905", {"start": v(45.98, -53.8) * mm, "end": v(45.58, -53.45) * mm});
            skLineSegment(sketch, "E1906", {"start": v(45.58, -53.45) * mm, "end": v(44.4, -52.36) * mm});
            skLineSegment(sketch, "E1907", {"start": v(44.4, -52.36) * mm, "end": v(42.81, -50.64) * mm});
            skLineSegment(sketch, "E1908", {"start": v(42.81, -50.64) * mm, "end": v(43.15, -49.7) * mm});
            skLineSegment(sketch, "E1909", {"start": v(43.15, -49.7) * mm, "end": v(44, -47.7) * mm});
            skLineSegment(sketch, "E1910", {"start": v(44, -47.7) * mm, "end": v(45.47, -45.01) * mm});
            skLineSegment(sketch, "E1911", {"start": v(45.47, -45.01) * mm, "end": v(45.14, -44.47) * mm});
            skLineSegment(sketch, "E1912", {"start": v(45.14, -44.47) * mm, "end": v(44.82, -43.9) * mm});
            skLineSegment(sketch, "E1913", {"start": v(44.82, -43.9) * mm, "end": v(44.49, -43.25) * mm});
            skLineSegment(sketch, "E1914", {"start": v(44.49, -43.25) * mm, "end": v(43.7, -41.4) * mm});
            skLineSegment(sketch, "E1915", {"start": v(43.7, -41.4) * mm, "end": v(43.65, -41.27) * mm});
            skLineSegment(sketch, "E1916", {"start": v(61.53, -33.98) * mm, "end": v(60.79, -34.29) * mm});
            skLineSegment(sketch, "E1917", {"start": v(60.79, -34.29) * mm, "end": v(60.48, -35.03) * mm});
            skLineSegment(sketch, "E1918", {"start": v(60.48, -35.03) * mm, "end": v(60.79, -35.77) * mm});
            skLineSegment(sketch, "E1919", {"start": v(60.79, -35.77) * mm, "end": v(61.53, -36.08) * mm});
            skLineSegment(sketch, "E1920", {"start": v(61.53, -36.08) * mm, "end": v(62.27, -35.77) * mm});
            skLineSegment(sketch, "E1921", {"start": v(62.27, -35.77) * mm, "end": v(62.57, -35.03) * mm});
            skLineSegment(sketch, "E1922", {"start": v(62.57, -35.03) * mm, "end": v(62.27, -34.29) * mm});
            skLineSegment(sketch, "E1923", {"start": v(62.27, -34.29) * mm, "end": v(61.53, -33.98) * mm});
            skLineSegment(sketch, "E1924", {"start": v(52.53, 45.31) * mm, "end": v(53.36, 44.84) * mm});
            skLineSegment(sketch, "E1925", {"start": v(53.36, 44.84) * mm, "end": v(54.2, 44.28) * mm});
            skLineSegment(sketch, "E1926", {"start": v(54.2, 44.28) * mm, "end": v(55.11, 43.56) * mm});
            skLineSegment(sketch, "E1927", {"start": v(55.11, 43.56) * mm, "end": v(56, 42.73) * mm});
            skLineSegment(sketch, "E1928", {"start": v(56, 42.73) * mm, "end": v(56.7, 41.94) * mm});
            skLineSegment(sketch, "E1929", {"start": v(56.7, 41.94) * mm, "end": v(57.37, 41.1) * mm});
            skLineSegment(sketch, "E1930", {"start": v(57.37, 41.1) * mm, "end": v(57.31, 40.88) * mm});
            skLineSegment(sketch, "E1931", {"start": v(57.31, 40.88) * mm, "end": v(56.82, 39.54) * mm});
            skLineSegment(sketch, "E1932", {"start": v(56.82, 39.54) * mm, "end": v(56.4, 38.67) * mm});
            skLineSegment(sketch, "E1933", {"start": v(56.4, 38.67) * mm, "end": v(55.52, 37.1) * mm});
            skLineSegment(sketch, "E1934", {"start": v(55.52, 37.1) * mm, "end": v(55.19, 36.62) * mm});
            skLineSegment(sketch, "E1935", {"start": v(55.19, 36.62) * mm, "end": v(55.05, 36.44) * mm});
            skLineSegment(sketch, "E1936", {"start": v(55.05, 36.44) * mm, "end": v(54.03, 36.5) * mm});
            skLineSegment(sketch, "E1937", {"start": v(54.03, 36.5) * mm, "end": v(51.87, 36.87) * mm});
            skLineSegment(sketch, "E1938", {"start": v(51.87, 36.87) * mm, "end": v(49.85, 37.53) * mm});
            skLineSegment(sketch, "E1939", {"start": v(49.85, 37.53) * mm, "end": v(49, 37.91) * mm});
            skLineSegment(sketch, "E1940", {"start": v(49, 37.91) * mm, "end": v(48.88, 37.81) * mm});
            skLineSegment(sketch, "E1941", {"start": v(48.88, 37.81) * mm, "end": v(48.54, 37.56) * mm});
            skLineSegment(sketch, "E1942", {"start": v(48.54, 37.56) * mm, "end": v(47.47, 36.86) * mm});
            skLineSegment(sketch, "E1943", {"start": v(47.47, 36.86) * mm, "end": v(46.58, 36.43) * mm});
            skLineSegment(sketch, "E1944", {"start": v(46.58, 36.43) * mm, "end": v(45.65, 36.08) * mm});
            skLineSegment(sketch, "E1945", {"start": v(45.65, 36.08) * mm, "end": v(45.46, 35.16) * mm});
            skLineSegment(sketch, "E1946", {"start": v(45.46, 35.16) * mm, "end": v(44.78, 33.1) * mm});
            skLineSegment(sketch, "E1947", {"start": v(44.78, 33.1) * mm, "end": v(44.27, 32) * mm});
            skLineSegment(sketch, "E1948", {"start": v(44.27, 32) * mm, "end": v(43.73, 31.08) * mm});
            skLineSegment(sketch, "E1949", {"start": v(43.73, 31.08) * mm, "end": v(43.14, 30.2) * mm});
            skLineSegment(sketch, "E1950", {"start": v(43.14, 30.2) * mm, "end": v(42.91, 30.19) * mm});
            skLineSegment(sketch, "E1951", {"start": v(42.91, 30.19) * mm, "end": v(42.32, 30.2) * mm});
            skLineSegment(sketch, "E1952", {"start": v(42.32, 30.2) * mm, "end": v(40.54, 30.35) * mm});
            skLineSegment(sketch, "E1953", {"start": v(40.54, 30.35) * mm, "end": v(39.6, 30.5) * mm});
            skLineSegment(sketch, "E1954", {"start": v(39.6, 30.5) * mm, "end": v(38.2, 30.87) * mm});
            skLineSegment(sketch, "E1955", {"start": v(38.2, 30.87) * mm, "end": v(38, 30.94) * mm});
            skLineSegment(sketch, "E1956", {"start": v(38, 30.94) * mm, "end": v(37.74, 31.94) * mm});
            skLineSegment(sketch, "E1957", {"start": v(37.74, 31.94) * mm, "end": v(37.54, 32.95) * mm});
            skLineSegment(sketch, "E1958", {"start": v(37.54, 32.95) * mm, "end": v(37.42, 34.11) * mm});
            skLineSegment(sketch, "E1959", {"start": v(37.42, 34.11) * mm, "end": v(37.42, 36.23) * mm});
            skLineSegment(sketch, "E1960", {"start": v(37.42, 36.23) * mm, "end": v(37.53, 37.16) * mm});
            skLineSegment(sketch, "E1961", {"start": v(37.53, 37.16) * mm, "end": v(37.4, 37.25) * mm});
            skLineSegment(sketch, "E1962", {"start": v(37.4, 37.25) * mm, "end": v(37.05, 37.49) * mm});
            skLineSegment(sketch, "E1963", {"start": v(37.05, 37.49) * mm, "end": v(36.57, 37.84) * mm});
            skLineSegment(sketch, "E1964", {"start": v(36.57, 37.84) * mm, "end": v(35.8, 38.53) * mm});
            skLineSegment(sketch, "E1965", {"start": v(35.8, 38.53) * mm, "end": v(35.18, 39.22) * mm});
            skLineSegment(sketch, "E1966", {"start": v(35.18, 39.22) * mm, "end": v(34.76, 39.8) * mm});
            skLineSegment(sketch, "E1967", {"start": v(34.76, 39.8) * mm, "end": v(34.5, 39.75) * mm});
            skLineSegment(sketch, "E1968", {"start": v(34.5, 39.75) * mm, "end": v(33.8, 39.68) * mm});
            skLineSegment(sketch, "E1969", {"start": v(33.8, 39.68) * mm, "end": v(32.8, 39.64) * mm});
            skLineSegment(sketch, "E1970", {"start": v(32.8, 39.64) * mm, "end": v(31.63, 39.68) * mm});
            skLineSegment(sketch, "E1971", {"start": v(31.63, 39.68) * mm, "end": v(29.4, 40.05) * mm});
            skLineSegment(sketch, "E1972", {"start": v(29.4, 40.05) * mm, "end": v(28.37, 40.35) * mm});
            skLineSegment(sketch, "E1973", {"start": v(28.37, 40.35) * mm, "end": v(28.3, 40.56) * mm});
            skLineSegment(sketch, "E1974", {"start": v(28.3, 40.56) * mm, "end": v(28.11, 41.13) * mm});
            skLineSegment(sketch, "E1975", {"start": v(28.11, 41.13) * mm, "end": v(27.8, 42.4) * mm});
            skLineSegment(sketch, "E1976", {"start": v(27.8, 42.4) * mm, "end": v(27.57, 43.83) * mm});
            skLineSegment(sketch, "E1977", {"start": v(27.57, 43.83) * mm, "end": v(27.5, 45.25) * mm});
            skLineSegment(sketch, "E1978", {"start": v(27.5, 45.25) * mm, "end": v(27.49, 45.48) * mm});
            skLineSegment(sketch, "E1979", {"start": v(27.49, 45.48) * mm, "end": v(28.37, 46.03) * mm});
            skLineSegment(sketch, "E1980", {"start": v(28.37, 46.03) * mm, "end": v(29.27, 46.52) * mm});
            skLineSegment(sketch, "E1981", {"start": v(29.27, 46.52) * mm, "end": v(29.78, 46.77) * mm});
            skLineSegment(sketch, "E1982", {"start": v(29.78, 46.77) * mm, "end": v(30.33, 47) * mm});
            skLineSegment(sketch, "E1983", {"start": v(30.33, 47) * mm, "end": v(32.34, 47.66) * mm});
            skLineSegment(sketch, "E1984", {"start": v(32.34, 47.66) * mm, "end": v(33.27, 47.84) * mm});
            skLineSegment(sketch, "E1985", {"start": v(33.27, 47.84) * mm, "end": v(33.42, 48.4) * mm});
            skLineSegment(sketch, "E1986", {"start": v(33.42, 48.4) * mm, "end": v(33.74, 49.27) * mm});
            skLineSegment(sketch, "E1987", {"start": v(33.74, 49.27) * mm, "end": v(34.2, 50.2) * mm});
            skLineSegment(sketch, "E1988", {"start": v(34.2, 50.2) * mm, "end": v(34.63, 50.9) * mm});
            skLineSegment(sketch, "E1989", {"start": v(34.63, 50.9) * mm, "end": v(34.9, 51.28) * mm});
            skLineSegment(sketch, "E1990", {"start": v(34.9, 51.28) * mm, "end": v(34.5, 52.16) * mm});
            skLineSegment(sketch, "E1991", {"start": v(34.5, 52.16) * mm, "end": v(33.84, 54.23) * mm});
            skLineSegment(sketch, "E1992", {"start": v(33.84, 54.23) * mm, "end": v(33.5, 56.47) * mm});
            skLineSegment(sketch, "E1993", {"start": v(33.5, 56.47) * mm, "end": v(33.47, 57.24) * mm});
            skLineSegment(sketch, "E1994", {"start": v(33.47, 57.24) * mm, "end": v(33.47, 57.53) * mm});
            skLineSegment(sketch, "E1995", {"start": v(33.47, 57.53) * mm, "end": v(34.12, 58.02) * mm});
            skLineSegment(sketch, "E1996", {"start": v(34.12, 58.02) * mm, "end": v(34.83, 58.47) * mm});
            skLineSegment(sketch, "E1997", {"start": v(34.83, 58.47) * mm, "end": v(35.66, 58.94) * mm});
            skLineSegment(sketch, "E1998", {"start": v(35.66, 58.94) * mm, "end": v(37.3, 59.68) * mm});
            skLineSegment(sketch, "E1999", {"start": v(37.3, 59.68) * mm, "end": v(38.07, 59.96) * mm});
            skLineSegment(sketch, "E2000", {"start": v(38.07, 59.96) * mm, "end": v(38.3, 59.79) * mm});
            skLineSegment(sketch, "E2001", {"start": v(38.3, 59.79) * mm, "end": v(38.86, 59.3) * mm});
            skLineSegment(sketch, "E2002", {"start": v(38.86, 59.3) * mm, "end": v(40.4, 57.73) * mm});
            skLineSegment(sketch, "E2003", {"start": v(40.4, 57.73) * mm, "end": v(41.64, 56.02) * mm});
            skLineSegment(sketch, "E2004", {"start": v(41.64, 56.02) * mm, "end": v(42.1, 55.19) * mm});
            skLineSegment(sketch, "E2005", {"start": v(42.1, 55.19) * mm, "end": v(42.68, 55.22) * mm});
            skLineSegment(sketch, "E2006", {"start": v(42.68, 55.22) * mm, "end": v(43.28, 55.2) * mm});
            skLineSegment(sketch, "E2007", {"start": v(43.28, 55.2) * mm, "end": v(43.96, 55.14) * mm});
            skLineSegment(sketch, "E2008", {"start": v(43.96, 55.14) * mm, "end": v(44.64, 55.04) * mm});
            skLineSegment(sketch, "E2009", {"start": v(44.64, 55.04) * mm, "end": v(45.62, 54.8) * mm});
            skLineSegment(sketch, "E2010", {"start": v(45.62, 54.8) * mm, "end": v(45.77, 54.74) * mm});
            skLineSegment(sketch, "E2011", {"start": v(45.77, 54.74) * mm, "end": v(45.89, 54.7) * mm});
            skLineSegment(sketch, "E2012", {"start": v(45.89, 54.7) * mm, "end": v(46.6, 55.35) * mm});
            skLineSegment(sketch, "E2013", {"start": v(46.6, 55.35) * mm, "end": v(48.35, 56.62) * mm});
            skLineSegment(sketch, "E2014", {"start": v(48.35, 56.62) * mm, "end": v(50.39, 57.63) * mm});
            skLineSegment(sketch, "E2015", {"start": v(50.39, 57.63) * mm, "end": v(51.11, 57.91) * mm});
            skLineSegment(sketch, "E2016", {"start": v(51.11, 57.91) * mm, "end": v(51.4, 58) * mm});
            skLineSegment(sketch, "E2017", {"start": v(51.4, 58) * mm, "end": v(52.05, 57.51) * mm});
            skLineSegment(sketch, "E2018", {"start": v(52.05, 57.51) * mm, "end": v(53.4, 56.34) * mm});
            skLineSegment(sketch, "E2019", {"start": v(53.4, 56.34) * mm, "end": v(54.06, 55.65) * mm});
            skLineSegment(sketch, "E2020", {"start": v(54.06, 55.65) * mm, "end": v(54.61, 55.02) * mm});
            skLineSegment(sketch, "E2021", {"start": v(54.61, 55.02) * mm, "end": v(55.1, 54.37) * mm});
            skLineSegment(sketch, "E2022", {"start": v(55.1, 54.37) * mm, "end": v(55, 54.1) * mm});
            skLineSegment(sketch, "E2023", {"start": v(55, 54.1) * mm, "end": v(54.73, 53.42) * mm});
            skLineSegment(sketch, "E2024", {"start": v(54.73, 53.42) * mm, "end": v(53.72, 51.47) * mm});
            skLineSegment(sketch, "E2025", {"start": v(53.72, 51.47) * mm, "end": v(52.47, 49.76) * mm});
            skLineSegment(sketch, "E2026", {"start": v(52.47, 49.76) * mm, "end": v(52.01, 49.25) * mm});
            skLineSegment(sketch, "E2027", {"start": v(52.01, 49.25) * mm, "end": v(51.83, 49.06) * mm});
            skLineSegment(sketch, "E2028", {"start": v(51.83, 49.06) * mm, "end": v(52.03, 48.52) * mm});
            skLineSegment(sketch, "E2029", {"start": v(52.03, 48.52) * mm, "end": v(52.2, 47.95) * mm});
            skLineSegment(sketch, "E2030", {"start": v(52.2, 47.95) * mm, "end": v(52.35, 47.29) * mm});
            skLineSegment(sketch, "E2031", {"start": v(52.35, 47.29) * mm, "end": v(52.5, 46.02) * mm});
            skLineSegment(sketch, "E2032", {"start": v(52.5, 46.02) * mm, "end": v(52.54, 45.44) * mm});
            skLineSegment(sketch, "E2033", {"start": v(52.54, 45.44) * mm, "end": v(52.53, 45.31) * mm});
            skLineSegment(sketch, "E2034", {"start": v(42.43, 46.1) * mm, "end": v(41.7, 45.8) * mm});
            skLineSegment(sketch, "E2035", {"start": v(41.7, 45.8) * mm, "end": v(41.4, 45.07) * mm});
            skLineSegment(sketch, "E2036", {"start": v(41.4, 45.07) * mm, "end": v(41.7, 44.34) * mm});
            skLineSegment(sketch, "E2037", {"start": v(41.7, 44.34) * mm, "end": v(42.43, 44.04) * mm});
            skLineSegment(sketch, "E2038", {"start": v(42.43, 44.04) * mm, "end": v(43.16, 44.34) * mm});
            skLineSegment(sketch, "E2039", {"start": v(43.16, 44.34) * mm, "end": v(43.46, 45.07) * mm});
            skLineSegment(sketch, "E2040", {"start": v(43.46, 45.07) * mm, "end": v(43.16, 45.8) * mm});
            skLineSegment(sketch, "E2041", {"start": v(43.16, 45.8) * mm, "end": v(42.43, 46.1) * mm});
            skSolve(sketch);
        }
        {
            var Q0;
            Q0=makeQuery(id+"F2.imprint","IMPRINT",FACE,{"disambiguationData":[TD([[makeQuery(id+"F2.imprint","IMPRINT",EDGE,{"derivedFrom":sQuery(id+"F2.wireOp",EDGE,"E1001")}),-1.0]])]});
            extrude(context, id + "F3", {"entities" : qUnion([Q0]), "depth" : 4 * mm});
        }
        {
            var Q0;
            Q0=makeQuery(id+"F2.imprint","IMPRINT",FACE,{"disambiguationData":[TD([[makeQuery(id+"F2.imprint","IMPRINT",EDGE,{"derivedFrom":sQuery(id+"F2.wireOp",EDGE,"E1528")}),-1.0]])]});
            extrude(context, id + "F4", {"entities" : qUnion([Q0]), "depth" : 4 * mm});
        }
        {
            var Q0;
            Q0=makeQuery(id+"F2.imprint","IMPRINT",FACE,{"disambiguationData":[TD([[makeQuery(id+"F2.imprint","IMPRINT",EDGE,{"derivedFrom":sQuery(id+"F2.wireOp",EDGE,"E1757")}),-1.0]])]});
            extrude(context, id + "F5", {"entities" : qUnion([Q0]), "depth" : 4 * mm});
        }
        {
            var Q0;
            Q0=makeQuery(id+"F2.imprint","IMPRINT",FACE,{"disambiguationData":[TD([[makeQuery(id+"F2.imprint","IMPRINT",EDGE,{"derivedFrom":sQuery(id+"F2.wireOp",EDGE,"E1924")}),-1.0]])]});
            extrude(context, id + "F6", {"entities" : qUnion([Q0]), "depth" : 4 * mm});
        }
        {
            var Q0;
            Q0=makeQuery(id+"F2.imprint","IMPRINT",FACE,{"disambiguationData":[TD([[makeQuery(id+"F2.imprint","IMPRINT",EDGE,{"derivedFrom":sQuery(id+"F2.wireOp",EDGE,"E1278")}),-1.0]])]});
            extrude(context, id + "F7", {"entities" : qUnion([Q0]), "depth" : 4 * mm});
        }
        {
            var Q0;
            Q0=makeQuery(id+"F4.opExtrude","SWEPT_BODY",BODY,{"disambiguationData":[OSD([sQuery(id+"F2.wireOp",EDGE,"E1528"),sQuery(id+"F2.wireOp",EDGE,"E1529"),sQuery(id+"F2.wireOp",EDGE,"E1530"),sQuery(id+"F2.wireOp",EDGE,"E1531"),sQuery(id+"F2.wireOp",EDGE,"E1532"),sQuery(id+"F2.wireOp",EDGE,"E1533"),sQuery(id+"F2.wireOp",EDGE,"E1534"),sQuery(id+"F2.wireOp",EDGE,"E1535"),sQuery(id+"F2.wireOp",EDGE,"E1536"),sQuery(id+"F2.wireOp",EDGE,"E1537"),sQuery(id+"F2.wireOp",EDGE,"E1538"),sQuery(id+"F2.wireOp",EDGE,"E1539"),sQuery(id+"F2.wireOp",EDGE,"E1540"),sQuery(id+"F2.wireOp",EDGE,"E1541"),sQuery(id+"F2.wireOp",EDGE,"E1542"),sQuery(id+"F2.wireOp",EDGE,"E1543"),sQuery(id+"F2.wireOp",EDGE,"E1544"),sQuery(id+"F2.wireOp",EDGE,"E1545"),sQuery(id+"F2.wireOp",EDGE,"E1546"),sQuery(id+"F2.wireOp",EDGE,"E1547"),sQuery(id+"F2.wireOp",EDGE,"E1548"),sQuery(id+"F2.wireOp",EDGE,"E1549"),sQuery(id+"F2.wireOp",EDGE,"E1550"),sQuery(id+"F2.wireOp",EDGE,"E1551"),sQuery(id+"F2.wireOp",EDGE,"E1552"),sQuery(id+"F2.wireOp",EDGE,"E1553"),sQuery(id+"F2.wireOp",EDGE,"E1554"),sQuery(id+"F2.wireOp",EDGE,"E1555"),sQuery(id+"F2.wireOp",EDGE,"E1556"),sQuery(id+"F2.wireOp",EDGE,"E1557"),sQuery(id+"F2.wireOp",EDGE,"E1558"),sQuery(id+"F2.wireOp",EDGE,"E1559"),sQuery(id+"F2.wireOp",EDGE,"E1560"),sQuery(id+"F2.wireOp",EDGE,"E1561"),sQuery(id+"F2.wireOp",EDGE,"E1562"),sQuery(id+"F2.wireOp",EDGE,"E1563"),sQuery(id+"F2.wireOp",EDGE,"E1564"),sQuery(id+"F2.wireOp",EDGE,"E1565"),sQuery(id+"F2.wireOp",EDGE,"E1566"),sQuery(id+"F2.wireOp",EDGE,"E1567"),sQuery(id+"F2.wireOp",EDGE,"E1568"),sQuery(id+"F2.wireOp",EDGE,"E1569"),sQuery(id+"F2.wireOp",EDGE,"E1570"),sQuery(id+"F2.wireOp",EDGE,"E1571"),sQuery(id+"F2.wireOp",EDGE,"E1572"),sQuery(id+"F2.wireOp",EDGE,"E1573"),sQuery(id+"F2.wireOp",EDGE,"E1574"),sQuery(id+"F2.wireOp",EDGE,"E1575"),sQuery(id+"F2.wireOp",EDGE,"E1576"),sQuery(id+"F2.wireOp",EDGE,"E1577"),sQuery(id+"F2.wireOp",EDGE,"E1578"),sQuery(id+"F2.wireOp",EDGE,"E1579"),sQuery(id+"F2.wireOp",EDGE,"E1580"),sQuery(id+"F2.wireOp",EDGE,"E1581"),sQuery(id+"F2.wireOp",EDGE,"E1582"),sQuery(id+"F2.wireOp",EDGE,"E1583"),sQuery(id+"F2.wireOp",EDGE,"E1584"),sQuery(id+"F2.wireOp",EDGE,"E1585"),sQuery(id+"F2.wireOp",EDGE,"E1586"),sQuery(id+"F2.wireOp",EDGE,"E1587"),sQuery(id+"F2.wireOp",EDGE,"E1588"),sQuery(id+"F2.wireOp",EDGE,"E1589"),sQuery(id+"F2.wireOp",EDGE,"E1590"),sQuery(id+"F2.wireOp",EDGE,"E1591"),sQuery(id+"F2.wireOp",EDGE,"E1592"),sQuery(id+"F2.wireOp",EDGE,"E1593"),sQuery(id+"F2.wireOp",EDGE,"E1594"),sQuery(id+"F2.wireOp",EDGE,"E1595"),sQuery(id+"F2.wireOp",EDGE,"E1596"),sQuery(id+"F2.wireOp",EDGE,"E1597"),sQuery(id+"F2.wireOp",EDGE,"E1598"),sQuery(id+"F2.wireOp",EDGE,"E1599"),sQuery(id+"F2.wireOp",EDGE,"E1600"),sQuery(id+"F2.wireOp",EDGE,"E1601"),sQuery(id+"F2.wireOp",EDGE,"E1602"),sQuery(id+"F2.wireOp",EDGE,"E1603"),sQuery(id+"F2.wireOp",EDGE,"E1604"),sQuery(id+"F2.wireOp",EDGE,"E1605"),sQuery(id+"F2.wireOp",EDGE,"E1606"),sQuery(id+"F2.wireOp",EDGE,"E1607"),sQuery(id+"F2.wireOp",EDGE,"E1608"),sQuery(id+"F2.wireOp",EDGE,"E1609"),sQuery(id+"F2.wireOp",EDGE,"E1610"),sQuery(id+"F2.wireOp",EDGE,"E1611"),sQuery(id+"F2.wireOp",EDGE,"E1612"),sQuery(id+"F2.wireOp",EDGE,"E1613"),sQuery(id+"F2.wireOp",EDGE,"E1614"),sQuery(id+"F2.wireOp",EDGE,"E1615"),sQuery(id+"F2.wireOp",EDGE,"E1616"),sQuery(id+"F2.wireOp",EDGE,"E1617"),sQuery(id+"F2.wireOp",EDGE,"E1618"),sQuery(id+"F2.wireOp",EDGE,"E1619"),sQuery(id+"F2.wireOp",EDGE,"E1620"),sQuery(id+"F2.wireOp",EDGE,"E1621"),sQuery(id+"F2.wireOp",EDGE,"E1622"),sQuery(id+"F2.wireOp",EDGE,"E1623"),sQuery(id+"F2.wireOp",EDGE,"E1624"),sQuery(id+"F2.wireOp",EDGE,"E1625"),sQuery(id+"F2.wireOp",EDGE,"E1626"),sQuery(id+"F2.wireOp",EDGE,"E1627"),sQuery(id+"F2.wireOp",EDGE,"E1628"),sQuery(id+"F2.wireOp",EDGE,"E1629"),sQuery(id+"F2.wireOp",EDGE,"E1630"),sQuery(id+"F2.wireOp",EDGE,"E1631"),sQuery(id+"F2.wireOp",EDGE,"E1632"),sQuery(id+"F2.wireOp",EDGE,"E1633"),sQuery(id+"F2.wireOp",EDGE,"E1634"),sQuery(id+"F2.wireOp",EDGE,"E1635"),sQuery(id+"F2.wireOp",EDGE,"E1636"),sQuery(id+"F2.wireOp",EDGE,"E1637"),sQuery(id+"F2.wireOp",EDGE,"E1638"),sQuery(id+"F2.wireOp",EDGE,"E1639"),sQuery(id+"F2.wireOp",EDGE,"E1640"),sQuery(id+"F2.wireOp",EDGE,"E1641"),sQuery(id+"F2.wireOp",EDGE,"E1642"),sQuery(id+"F2.wireOp",EDGE,"E1643"),sQuery(id+"F2.wireOp",EDGE,"E1644"),sQuery(id+"F2.wireOp",EDGE,"E1645"),sQuery(id+"F2.wireOp",EDGE,"E1646"),sQuery(id+"F2.wireOp",EDGE,"E1647"),sQuery(id+"F2.wireOp",EDGE,"E1648"),sQuery(id+"F2.wireOp",EDGE,"E1649"),sQuery(id+"F2.wireOp",EDGE,"E1650"),sQuery(id+"F2.wireOp",EDGE,"E1651"),sQuery(id+"F2.wireOp",EDGE,"E1652"),sQuery(id+"F2.wireOp",EDGE,"E1653"),sQuery(id+"F2.wireOp",EDGE,"E1654"),sQuery(id+"F2.wireOp",EDGE,"E1655"),sQuery(id+"F2.wireOp",EDGE,"E1656"),sQuery(id+"F2.wireOp",EDGE,"E1657"),sQuery(id+"F2.wireOp",EDGE,"E1658"),sQuery(id+"F2.wireOp",EDGE,"E1659"),sQuery(id+"F2.wireOp",EDGE,"E1660"),sQuery(id+"F2.wireOp",EDGE,"E1661"),sQuery(id+"F2.wireOp",EDGE,"E1662"),sQuery(id+"F2.wireOp",EDGE,"E1663"),sQuery(id+"F2.wireOp",EDGE,"E1664"),sQuery(id+"F2.wireOp",EDGE,"E1665"),sQuery(id+"F2.wireOp",EDGE,"E1666"),sQuery(id+"F2.wireOp",EDGE,"E1667"),sQuery(id+"F2.wireOp",EDGE,"E1668"),sQuery(id+"F2.wireOp",EDGE,"E1669"),sQuery(id+"F2.wireOp",EDGE,"E1670"),sQuery(id+"F2.wireOp",EDGE,"E1671"),sQuery(id+"F2.wireOp",EDGE,"E1672"),sQuery(id+"F2.wireOp",EDGE,"E1673"),sQuery(id+"F2.wireOp",EDGE,"E1674"),sQuery(id+"F2.wireOp",EDGE,"E1675"),sQuery(id+"F2.wireOp",EDGE,"E1676"),sQuery(id+"F2.wireOp",EDGE,"E1677"),sQuery(id+"F2.wireOp",EDGE,"E1678"),sQuery(id+"F2.wireOp",EDGE,"E1679"),sQuery(id+"F2.wireOp",EDGE,"E1680"),sQuery(id+"F2.wireOp",EDGE,"E1681"),sQuery(id+"F2.wireOp",EDGE,"E1682"),sQuery(id+"F2.wireOp",EDGE,"E1683"),sQuery(id+"F2.wireOp",EDGE,"E1684"),sQuery(id+"F2.wireOp",EDGE,"E1685"),sQuery(id+"F2.wireOp",EDGE,"E1686"),sQuery(id+"F2.wireOp",EDGE,"E1687"),sQuery(id+"F2.wireOp",EDGE,"E1688"),sQuery(id+"F2.wireOp",EDGE,"E1689"),sQuery(id+"F2.wireOp",EDGE,"E1690"),sQuery(id+"F2.wireOp",EDGE,"E1691"),sQuery(id+"F2.wireOp",EDGE,"E1692"),sQuery(id+"F2.wireOp",EDGE,"E1693"),sQuery(id+"F2.wireOp",EDGE,"E1694"),sQuery(id+"F2.wireOp",EDGE,"E1695"),sQuery(id+"F2.wireOp",EDGE,"E1696"),sQuery(id+"F2.wireOp",EDGE,"E1697"),sQuery(id+"F2.wireOp",EDGE,"E1698"),sQuery(id+"F2.wireOp",EDGE,"E1699"),sQuery(id+"F2.wireOp",EDGE,"E1700"),sQuery(id+"F2.wireOp",EDGE,"E1701"),sQuery(id+"F2.wireOp",EDGE,"E1702"),sQuery(id+"F2.wireOp",EDGE,"E1703"),sQuery(id+"F2.wireOp",EDGE,"E1704"),sQuery(id+"F2.wireOp",EDGE,"E1705"),sQuery(id+"F2.wireOp",EDGE,"E1706"),sQuery(id+"F2.wireOp",EDGE,"E1707"),sQuery(id+"F2.wireOp",EDGE,"E1708"),sQuery(id+"F2.wireOp",EDGE,"E1709"),sQuery(id+"F2.wireOp",EDGE,"E1710"),sQuery(id+"F2.wireOp",EDGE,"E1711"),sQuery(id+"F2.wireOp",EDGE,"E1712"),sQuery(id+"F2.wireOp",EDGE,"E1713"),sQuery(id+"F2.wireOp",EDGE,"E1714"),sQuery(id+"F2.wireOp",EDGE,"E1715"),sQuery(id+"F2.wireOp",EDGE,"E1716"),sQuery(id+"F2.wireOp",EDGE,"E1717"),sQuery(id+"F2.wireOp",EDGE,"E1718"),sQuery(id+"F2.wireOp",EDGE,"E1719"),sQuery(id+"F2.wireOp",EDGE,"E1720"),sQuery(id+"F2.wireOp",EDGE,"E1721"),sQuery(id+"F2.wireOp",EDGE,"E1722"),sQuery(id+"F2.wireOp",EDGE,"E1723"),sQuery(id+"F2.wireOp",EDGE,"E1724"),sQuery(id+"F2.wireOp",EDGE,"E1725"),sQuery(id+"F2.wireOp",EDGE,"E1726"),sQuery(id+"F2.wireOp",EDGE,"E1727"),sQuery(id+"F2.wireOp",EDGE,"E1728"),sQuery(id+"F2.wireOp",EDGE,"E1729"),sQuery(id+"F2.wireOp",EDGE,"E1730"),sQuery(id+"F2.wireOp",EDGE,"E1731"),sQuery(id+"F2.wireOp",EDGE,"E1732"),sQuery(id+"F2.wireOp",EDGE,"E1733"),sQuery(id+"F2.wireOp",EDGE,"E1734"),sQuery(id+"F2.wireOp",EDGE,"E1735"),sQuery(id+"F2.wireOp",EDGE,"E1736"),sQuery(id+"F2.wireOp",EDGE,"E1737"),sQuery(id+"F2.wireOp",EDGE,"E1738"),sQuery(id+"F2.wireOp",EDGE,"E1739"),sQuery(id+"F2.wireOp",EDGE,"E1740"),sQuery(id+"F2.wireOp",EDGE,"E1741"),sQuery(id+"F2.wireOp",EDGE,"E1742"),sQuery(id+"F2.wireOp",EDGE,"E1743"),sQuery(id+"F2.wireOp",EDGE,"E1744"),sQuery(id+"F2.wireOp",EDGE,"E1745"),sQuery(id+"F2.wireOp",EDGE,"E1746"),sQuery(id+"F2.wireOp",EDGE,"E1747"),sQuery(id+"F2.wireOp",EDGE,"E1748"),sQuery(id+"F2.wireOp",EDGE,"E1749"),sQuery(id+"F2.wireOp",EDGE,"E1750"),sQuery(id+"F2.wireOp",EDGE,"E1751"),sQuery(id+"F2.wireOp",EDGE,"E1752"),sQuery(id+"F2.wireOp",EDGE,"E1753"),sQuery(id+"F2.wireOp",EDGE,"E1754"),sQuery(id+"F2.wireOp",EDGE,"E1755"),sQuery(id+"F2.wireOp",EDGE,"E1756")])]});
            var Q1;
            Q1=makeQuery(id+"F5.opExtrude","CAP_VERTEX",VERTEX,{"disambiguationData":[OSD([sQuery(id+"F2.wireOp",EDGE,"E1919"),sQuery(id+"F2.wireOp",EDGE,"E1920")])],"isStart":false});
            transform(context, id + "F8", {"entities" : qUnion([Q0]), "transformType" : TransformType.SCALE_UNIFORMLY, "scale" : .4, "scalePoint" : qUnion([Q1]), "makeCopy" : true});
        }
        {
            var Q0;
            Q0=makeQuery(id+"F6.opExtrude","SWEPT_BODY",BODY,{"disambiguationData":[OSD([sQuery(id+"F2.wireOp",EDGE,"E1924"),sQuery(id+"F2.wireOp",EDGE,"E1925"),sQuery(id+"F2.wireOp",EDGE,"E1926"),sQuery(id+"F2.wireOp",EDGE,"E1927"),sQuery(id+"F2.wireOp",EDGE,"E1928"),sQuery(id+"F2.wireOp",EDGE,"E1929"),sQuery(id+"F2.wireOp",EDGE,"E1930"),sQuery(id+"F2.wireOp",EDGE,"E1931"),sQuery(id+"F2.wireOp",EDGE,"E1932"),sQuery(id+"F2.wireOp",EDGE,"E1933"),sQuery(id+"F2.wireOp",EDGE,"E1934"),sQuery(id+"F2.wireOp",EDGE,"E1935"),sQuery(id+"F2.wireOp",EDGE,"E1936"),sQuery(id+"F2.wireOp",EDGE,"E1937"),sQuery(id+"F2.wireOp",EDGE,"E1938"),sQuery(id+"F2.wireOp",EDGE,"E1939"),sQuery(id+"F2.wireOp",EDGE,"E1940"),sQuery(id+"F2.wireOp",EDGE,"E1941"),sQuery(id+"F2.wireOp",EDGE,"E1942"),sQuery(id+"F2.wireOp",EDGE,"E1943"),sQuery(id+"F2.wireOp",EDGE,"E1944"),sQuery(id+"F2.wireOp",EDGE,"E1945"),sQuery(id+"F2.wireOp",EDGE,"E1946"),sQuery(id+"F2.wireOp",EDGE,"E1947"),sQuery(id+"F2.wireOp",EDGE,"E1948"),sQuery(id+"F2.wireOp",EDGE,"E1949"),sQuery(id+"F2.wireOp",EDGE,"E1950"),sQuery(id+"F2.wireOp",EDGE,"E1951"),sQuery(id+"F2.wireOp",EDGE,"E1952"),sQuery(id+"F2.wireOp",EDGE,"E1953"),sQuery(id+"F2.wireOp",EDGE,"E1954"),sQuery(id+"F2.wireOp",EDGE,"E1955"),sQuery(id+"F2.wireOp",EDGE,"E1956"),sQuery(id+"F2.wireOp",EDGE,"E1957"),sQuery(id+"F2.wireOp",EDGE,"E1958"),sQuery(id+"F2.wireOp",EDGE,"E1959"),sQuery(id+"F2.wireOp",EDGE,"E1960"),sQuery(id+"F2.wireOp",EDGE,"E1961"),sQuery(id+"F2.wireOp",EDGE,"E1962"),sQuery(id+"F2.wireOp",EDGE,"E1963"),sQuery(id+"F2.wireOp",EDGE,"E1964"),sQuery(id+"F2.wireOp",EDGE,"E1965"),sQuery(id+"F2.wireOp",EDGE,"E1966"),sQuery(id+"F2.wireOp",EDGE,"E1967"),sQuery(id+"F2.wireOp",EDGE,"E1968"),sQuery(id+"F2.wireOp",EDGE,"E1969"),sQuery(id+"F2.wireOp",EDGE,"E1970"),sQuery(id+"F2.wireOp",EDGE,"E1971"),sQuery(id+"F2.wireOp",EDGE,"E1972"),sQuery(id+"F2.wireOp",EDGE,"E1973"),sQuery(id+"F2.wireOp",EDGE,"E1974"),sQuery(id+"F2.wireOp",EDGE,"E1975"),sQuery(id+"F2.wireOp",EDGE,"E1976"),sQuery(id+"F2.wireOp",EDGE,"E1977"),sQuery(id+"F2.wireOp",EDGE,"E1978"),sQuery(id+"F2.wireOp",EDGE,"E1979"),sQuery(id+"F2.wireOp",EDGE,"E1980"),sQuery(id+"F2.wireOp",EDGE,"E1981"),sQuery(id+"F2.wireOp",EDGE,"E1982"),sQuery(id+"F2.wireOp",EDGE,"E1983"),sQuery(id+"F2.wireOp",EDGE,"E1984"),sQuery(id+"F2.wireOp",EDGE,"E1985"),sQuery(id+"F2.wireOp",EDGE,"E1986"),sQuery(id+"F2.wireOp",EDGE,"E1987"),sQuery(id+"F2.wireOp",EDGE,"E1988"),sQuery(id+"F2.wireOp",EDGE,"E1989"),sQuery(id+"F2.wireOp",EDGE,"E1990"),sQuery(id+"F2.wireOp",EDGE,"E1991"),sQuery(id+"F2.wireOp",EDGE,"E1992"),sQuery(id+"F2.wireOp",EDGE,"E1993"),sQuery(id+"F2.wireOp",EDGE,"E1994"),sQuery(id+"F2.wireOp",EDGE,"E1995"),sQuery(id+"F2.wireOp",EDGE,"E1996"),sQuery(id+"F2.wireOp",EDGE,"E1997"),sQuery(id+"F2.wireOp",EDGE,"E1998"),sQuery(id+"F2.wireOp",EDGE,"E1999"),sQuery(id+"F2.wireOp",EDGE,"E2000"),sQuery(id+"F2.wireOp",EDGE,"E2001"),sQuery(id+"F2.wireOp",EDGE,"E2002"),sQuery(id+"F2.wireOp",EDGE,"E2003"),sQuery(id+"F2.wireOp",EDGE,"E2004"),sQuery(id+"F2.wireOp",EDGE,"E2005"),sQuery(id+"F2.wireOp",EDGE,"E2006"),sQuery(id+"F2.wireOp",EDGE,"E2007"),sQuery(id+"F2.wireOp",EDGE,"E2008"),sQuery(id+"F2.wireOp",EDGE,"E2009"),sQuery(id+"F2.wireOp",EDGE,"E2010"),sQuery(id+"F2.wireOp",EDGE,"E2011"),sQuery(id+"F2.wireOp",EDGE,"E2012"),sQuery(id+"F2.wireOp",EDGE,"E2013"),sQuery(id+"F2.wireOp",EDGE,"E2014"),sQuery(id+"F2.wireOp",EDGE,"E2015"),sQuery(id+"F2.wireOp",EDGE,"E2016"),sQuery(id+"F2.wireOp",EDGE,"E2017"),sQuery(id+"F2.wireOp",EDGE,"E2018"),sQuery(id+"F2.wireOp",EDGE,"E2019"),sQuery(id+"F2.wireOp",EDGE,"E2020"),sQuery(id+"F2.wireOp",EDGE,"E2021"),sQuery(id+"F2.wireOp",EDGE,"E2022"),sQuery(id+"F2.wireOp",EDGE,"E2023"),sQuery(id+"F2.wireOp",EDGE,"E2024"),sQuery(id+"F2.wireOp",EDGE,"E2025"),sQuery(id+"F2.wireOp",EDGE,"E2026"),sQuery(id+"F2.wireOp",EDGE,"E2027"),sQuery(id+"F2.wireOp",EDGE,"E2028"),sQuery(id+"F2.wireOp",EDGE,"E2029"),sQuery(id+"F2.wireOp",EDGE,"E2030"),sQuery(id+"F2.wireOp",EDGE,"E2031"),sQuery(id+"F2.wireOp",EDGE,"E2032"),sQuery(id+"F2.wireOp",EDGE,"E2033"),sQuery(id+"F2.wireOp",EDGE,"E2034"),sQuery(id+"F2.wireOp",EDGE,"E2035"),sQuery(id+"F2.wireOp",EDGE,"E2036"),sQuery(id+"F2.wireOp",EDGE,"E2037"),sQuery(id+"F2.wireOp",EDGE,"E2038"),sQuery(id+"F2.wireOp",EDGE,"E2039"),sQuery(id+"F2.wireOp",EDGE,"E2040"),sQuery(id+"F2.wireOp",EDGE,"E2041")])]});
            var Q1;
            Q1=makeQuery(id+"F5.opExtrude","CAP_VERTEX",VERTEX,{"disambiguationData":[OSD([sQuery(id+"F2.wireOp",EDGE,"E1921"),sQuery(id+"F2.wireOp",EDGE,"E1922")])],"isStart":false});
            transform(context, id + "F9", {"entities" : qUnion([Q0]), "transformType" : TransformType.SCALE_UNIFORMLY, "scale" : .4, "scalePoint" : qUnion([Q1]), "makeCopy" : true});
        }
    });
